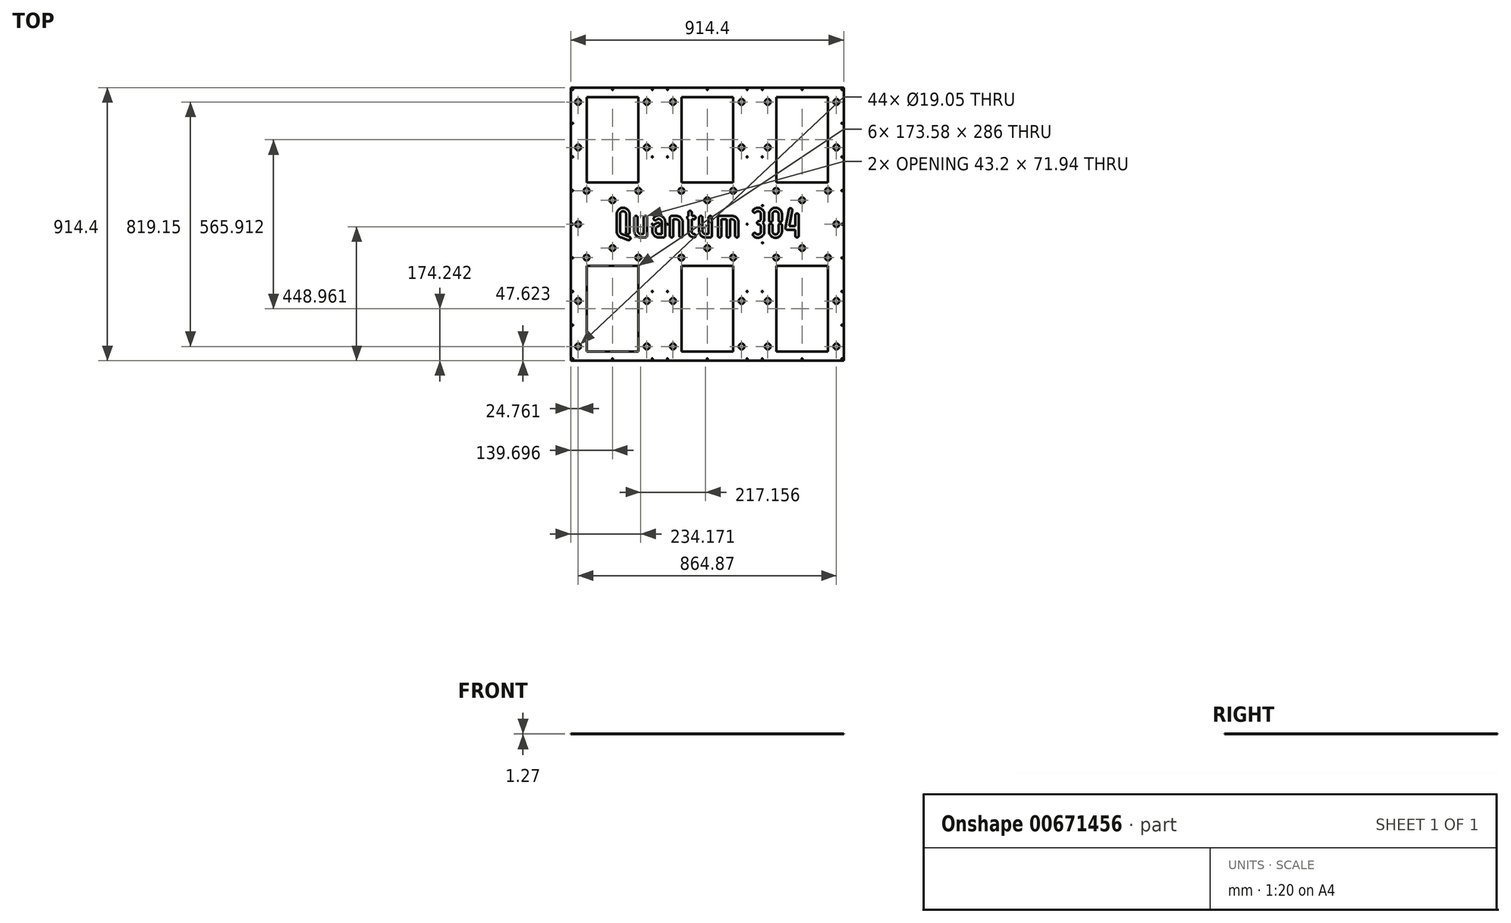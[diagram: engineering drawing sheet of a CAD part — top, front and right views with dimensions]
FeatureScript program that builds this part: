
annotation { "Feature Type Name" : "Feature", "Feature Type Description" : "" }
export const myFeature = defineFeature(function(context is Context, id is Id, definition is map)
    precondition{}
    {
        {
            var Q0;
            Q0=qCreatedBy(makeId("Top.planeOp"),FACE);
            var sketch = newSketch(context, id + "F0", { "sketchPlane" : qUnion([Q0])});
            skLineSegment(sketch, "E0.bottom", {"start": v(-471.91, 518.2) * mm, "end": v(442.49, 518.2) * mm});
            skLineSegment(sketch, "E0.top", {"start": v(-471.91, -396.2) * mm, "end": v(442.49, -396.2) * mm});
            skLineSegment(sketch, "E0.left", {"start": v(-471.91, 518.2) * mm, "end": v(-471.91, -396.2) * mm});
            skLineSegment(sketch, "E0.right", {"start": v(442.49, 518.2) * mm, "end": v(442.49, -396.2) * mm});
            skLineSegment(sketch, "E1", {"start": v(-14.71, 518.2) * mm, "end": v(-14.71, -396.2) * mm, "construction": true});
            skLineSegment(sketch, "E2", {"start": v(-471.91, 61) * mm, "end": v(442.49, 61) * mm, "construction": true});
            skLineSegment(sketch, "E3.0", {"start": v(-459.21, 505.5) * mm, "end": v(-459.21, -383.5) * mm, "construction": true});
            skLineSegment(sketch, "E4.0", {"start": v(-471.91, 505.5) * mm, "end": v(442.49, 505.5) * mm, "construction": true});
            skLineSegment(sketch, "E5.0", {"start": v(429.79, 505.5) * mm, "end": v(429.79, -383.5) * mm, "construction": true});
            skLineSegment(sketch, "E6.0", {"start": v(-471.91, -383.5) * mm, "end": v(442.49, -383.5) * mm, "construction": true});
            skLineSegment(sketch, "E7.0", {"start": v(-192.51, 505.5) * mm, "end": v(-192.51, -383.5) * mm, "construction": true});
            skLineSegment(sketch, "E8.0", {"start": v(-205.21, 505.5) * mm, "end": v(-205.21, -383.5) * mm, "construction": true});
            skLineSegment(sketch, "E9.0", {"start": v(-154.41, 505.5) * mm, "end": v(-154.41, -383.5) * mm, "construction": true});
            skLineSegment(sketch, "E10.0", {"start": v(124.99, 505.5) * mm, "end": v(124.99, -383.5) * mm, "construction": true});
            skLineSegment(sketch, "E11.0", {"start": v(163.09, 505.5) * mm, "end": v(163.09, -383.5) * mm, "construction": true});
            skLineSegment(sketch, "E12.0", {"start": v(175.79, 505.5) * mm, "end": v(175.79, -383.5) * mm, "construction": true});
            skLineSegment(sketch, "E13.0", {"start": v(-141.71, 505.5) * mm, "end": v(-141.71, -383.5) * mm, "construction": true});
            skLineSegment(sketch, "E14.0", {"start": v(112.29, 505.5) * mm, "end": v(112.29, -383.5) * mm, "construction": true});
            skLineSegment(sketch, "E15.0", {"start": v(-332.21, 505.5) * mm, "end": v(-332.21, -383.5) * mm, "construction": true});
            skLineSegment(sketch, "E16.0", {"start": v(302.79, 505.5) * mm, "end": v(302.79, -383.5) * mm, "construction": true});
            skPoint(sketch, "E17.middle", {"position": v(-332.21, 61) * mm});
            skCircle(sketch, "E18", {"center": v(-332.21, 61) * mm, "radius": 68 * mm, "construction": true});
            skCircle(sketch, "E19", {"center": v(-384.71, 113.5) * mm, "radius": 1.65 * mm, "construction": true});
            skCircle(sketch, "E20.MirrorC", {"center": v(-279.71, 113.5) * mm, "radius": 1.65 * mm, "construction": true});
            skCircle(sketch, "E21.MirrorC", {"center": v(-384.71, 8.5) * mm, "radius": 1.65 * mm, "construction": true});
            skCircle(sketch, "E22.MirrorC", {"center": v(-279.71, 8.5) * mm, "radius": 1.65 * mm, "construction": true});
            skCircle(sketch, "E23.MirrorC", {"center": v(250.29, 113.5) * mm, "radius": 1.65 * mm, "construction": true});
            skCircle(sketch, "E24.MirrorC", {"center": v(355.29, 113.5) * mm, "radius": 1.65 * mm, "construction": true});
            skCircle(sketch, "E25.MirrorC", {"center": v(355.29, 8.5) * mm, "radius": 1.65 * mm, "construction": true});
            skCircle(sketch, "E26.MirrorC", {"center": v(250.29, 8.5) * mm, "radius": 1.65 * mm, "construction": true});
            skCircle(sketch, "E27.MirrorC", {"center": v(302.79, 61) * mm, "radius": 68 * mm, "construction": true});
            skCircle(sketch, "E28.MirrorC", {"center": v(-14.71, 61) * mm, "radius": 68 * mm, "construction": true});
            skCircle(sketch, "E29.MirrorC", {"center": v(-67.21, 113.5) * mm, "radius": 1.65 * mm, "construction": true});
            skCircle(sketch, "E30.MirrorC", {"center": v(37.79, 113.5) * mm, "radius": 1.65 * mm, "construction": true});
            skCircle(sketch, "E31.MirrorC", {"center": v(37.79, 8.5) * mm, "radius": 1.65 * mm, "construction": true});
            skCircle(sketch, "E32.MirrorC", {"center": v(-67.21, 8.5) * mm, "radius": 1.65 * mm, "construction": true});
            skLineSegment(sketch, "E33.bottom", {"start": v(-435.08, 499.15) * mm, "end": v(-229.34, 499.15) * mm, "construction": true});
            skLineSegment(sketch, "E33.top", {"start": v(-435.08, 188.76) * mm, "end": v(-229.34, 188.76) * mm, "construction": true});
            skLineSegment(sketch, "E33.left", {"start": v(-435.08, 499.15) * mm, "end": v(-435.08, 188.76) * mm, "construction": true});
            skLineSegment(sketch, "E33.right", {"start": v(-229.34, 499.15) * mm, "end": v(-229.34, 188.76) * mm, "construction": true});
            skLineSegment(sketch, "E34.MirrorCS", {"start": v(-117.58, 499.15) * mm, "end": v(-117.58, 188.76) * mm, "construction": true});
            skLineSegment(sketch, "E35.MirrorCS", {"start": v(88.16, 499.15) * mm, "end": v(88.16, 188.76) * mm, "construction": true});
            skLineSegment(sketch, "E36.MirrorCS", {"start": v(88.16, 499.15) * mm, "end": v(-117.58, 499.15) * mm, "construction": true});
            skLineSegment(sketch, "E37.MirrorCS", {"start": v(88.16, 188.76) * mm, "end": v(-117.58, 188.76) * mm, "construction": true});
            skLineSegment(sketch, "E38.MirrorCS", {"start": v(199.92, 499.15) * mm, "end": v(199.92, 188.76) * mm, "construction": true});
            skLineSegment(sketch, "E39.MirrorCS", {"start": v(405.66, 499.15) * mm, "end": v(405.66, 188.76) * mm, "construction": true});
            skLineSegment(sketch, "E40.MirrorCS", {"start": v(405.66, 499.15) * mm, "end": v(199.92, 499.15) * mm, "construction": true});
            skLineSegment(sketch, "E41.MirrorCS", {"start": v(405.66, 188.76) * mm, "end": v(199.92, 188.76) * mm, "construction": true});
            skLineSegment(sketch, "E42.MirrorCS", {"start": v(-435.08, -66.76) * mm, "end": v(-229.34, -66.76) * mm, "construction": true});
            skLineSegment(sketch, "E43.MirrorCS", {"start": v(-435.08, -377.15) * mm, "end": v(-435.08, -66.76) * mm, "construction": true});
            skLineSegment(sketch, "E44.MirrorCS", {"start": v(-229.34, -377.15) * mm, "end": v(-229.34, -66.76) * mm, "construction": true});
            skLineSegment(sketch, "E45.MirrorCS", {"start": v(-117.58, -377.15) * mm, "end": v(-117.58, -66.76) * mm, "construction": true});
            skLineSegment(sketch, "E46.MirrorCS", {"start": v(88.16, -66.76) * mm, "end": v(-117.58, -66.76) * mm, "construction": true});
            skLineSegment(sketch, "E47.MirrorCS", {"start": v(88.16, -377.15) * mm, "end": v(88.16, -66.76) * mm, "construction": true});
            skLineSegment(sketch, "E48.MirrorCS", {"start": v(199.92, -377.15) * mm, "end": v(199.92, -66.76) * mm, "construction": true});
            skLineSegment(sketch, "E49.MirrorCS", {"start": v(405.66, -66.76) * mm, "end": v(199.92, -66.76) * mm, "construction": true});
            skLineSegment(sketch, "E50.MirrorCS", {"start": v(405.66, -377.15) * mm, "end": v(405.66, -66.76) * mm, "construction": true});
            skLineSegment(sketch, "E51.MirrorCS", {"start": v(405.66, -377.15) * mm, "end": v(199.92, -377.15) * mm, "construction": true});
            skLineSegment(sketch, "E52.MirrorCS", {"start": v(88.16, -377.15) * mm, "end": v(-117.58, -377.15) * mm, "construction": true});
            skLineSegment(sketch, "E53.MirrorCS", {"start": v(-435.08, -377.15) * mm, "end": v(-229.34, -377.15) * mm, "construction": true});
            skLineSegment(sketch, "E54.bottom", {"start": v(-419, 486.96) * mm, "end": v(-245.42, 486.96) * mm});
            skLineSegment(sketch, "E54.top", {"start": v(-419, 200.95) * mm, "end": v(-245.42, 200.95) * mm});
            skLineSegment(sketch, "E54.left", {"start": v(-419, 486.96) * mm, "end": v(-419, 200.95) * mm});
            skLineSegment(sketch, "E54.right", {"start": v(-245.42, 486.96) * mm, "end": v(-245.42, 200.95) * mm});
            skLineSegment(sketch, "E55.MirrorCS", {"start": v(-101.5, 486.96) * mm, "end": v(-101.5, 200.95) * mm});
            skLineSegment(sketch, "E56.MirrorCS", {"start": v(72.08, 486.96) * mm, "end": v(-101.5, 486.96) * mm});
            skLineSegment(sketch, "E57.MirrorCS", {"start": v(72.08, 486.96) * mm, "end": v(72.08, 200.95) * mm});
            skLineSegment(sketch, "E58.MirrorCS", {"start": v(72.08, 200.95) * mm, "end": v(-101.5, 200.95) * mm});
            skLineSegment(sketch, "E59.MirrorCS", {"start": v(216, 486.96) * mm, "end": v(216, 200.95) * mm});
            skLineSegment(sketch, "E60.MirrorCS", {"start": v(389.58, 486.96) * mm, "end": v(216, 486.96) * mm});
            skLineSegment(sketch, "E61.MirrorCS", {"start": v(389.58, 200.95) * mm, "end": v(216, 200.95) * mm});
            skLineSegment(sketch, "E62.MirrorCS", {"start": v(389.58, 486.96) * mm, "end": v(389.58, 200.95) * mm});
            skLineSegment(sketch, "E63.MirrorCS", {"start": v(-419, -78.96) * mm, "end": v(-245.42, -78.96) * mm});
            skLineSegment(sketch, "E64.MirrorCS", {"start": v(-245.42, -364.96) * mm, "end": v(-245.42, -78.96) * mm});
            skLineSegment(sketch, "E65.MirrorCS", {"start": v(-419, -364.96) * mm, "end": v(-419, -78.96) * mm});
            skLineSegment(sketch, "E66.MirrorCS", {"start": v(-419, -364.96) * mm, "end": v(-245.42, -364.96) * mm});
            skLineSegment(sketch, "E67.MirrorCS", {"start": v(72.08, -364.96) * mm, "end": v(-101.5, -364.96) * mm});
            skLineSegment(sketch, "E68.MirrorCS", {"start": v(-101.5, -364.96) * mm, "end": v(-101.5, -78.96) * mm});
            skLineSegment(sketch, "E69.MirrorCS", {"start": v(72.08, -78.96) * mm, "end": v(-101.5, -78.96) * mm});
            skLineSegment(sketch, "E70.MirrorCS", {"start": v(72.08, -364.96) * mm, "end": v(72.08, -78.96) * mm});
            skLineSegment(sketch, "E71.MirrorCS", {"start": v(216, -364.96) * mm, "end": v(216, -78.96) * mm});
            skLineSegment(sketch, "E72.MirrorCS", {"start": v(389.58, -364.96) * mm, "end": v(216, -364.96) * mm});
            skLineSegment(sketch, "E73.MirrorCS", {"start": v(389.58, -364.96) * mm, "end": v(389.58, -78.96) * mm});
            skLineSegment(sketch, "E74.MirrorCS", {"start": v(389.58, -78.96) * mm, "end": v(216, -78.96) * mm});
            skCircle(sketch, "E75", {"center": v(-332.21, 141.14) * mm, "radius": 9.53 * mm});
            skCircle(sketch, "E76", {"center": v(-245.42, 172.89) * mm, "radius": 9.53 * mm});
            skCircle(sketch, "E77", {"center": v(-419, 172.89) * mm, "radius": 9.53 * mm});
            skCircle(sketch, "E78.MirrorC", {"center": v(216, 172.89) * mm, "radius": 9.53 * mm});
            skCircle(sketch, "E79.MirrorC", {"center": v(302.79, 141.14) * mm, "radius": 9.53 * mm});
            skCircle(sketch, "E80.MirrorC", {"center": v(389.58, 172.89) * mm, "radius": 9.53 * mm});
            skCircle(sketch, "E81.MirrorC", {"center": v(-245.42, -50.89) * mm, "radius": 9.53 * mm});
            skCircle(sketch, "E82.MirrorC", {"center": v(-332.21, -19.14) * mm, "radius": 9.53 * mm});
            skCircle(sketch, "E83.MirrorC", {"center": v(-419, -50.89) * mm, "radius": 9.53 * mm});
            skCircle(sketch, "E84.MirrorC", {"center": v(216, -50.89) * mm, "radius": 9.53 * mm});
            skCircle(sketch, "E85.MirrorC", {"center": v(302.79, -19.14) * mm, "radius": 9.53 * mm});
            skCircle(sketch, "E86.MirrorC", {"center": v(389.58, -50.89) * mm, "radius": 9.53 * mm});
            skCircle(sketch, "E87", {"center": v(-447.15, -196.18) * mm, "radius": 9.53 * mm});
            skCircle(sketch, "E88", {"center": v(-447.15, -348.58) * mm, "radius": 9.53 * mm});
            skCircle(sketch, "E89.MirrorC", {"center": v(-217.28, -196.18) * mm, "radius": 9.53 * mm});
            skCircle(sketch, "E90.MirrorC", {"center": v(-217.28, -348.58) * mm, "radius": 9.53 * mm});
            skCircle(sketch, "E91.MirrorC", {"center": v(187.85, -196.18) * mm, "radius": 9.53 * mm});
            skCircle(sketch, "E92.MirrorC", {"center": v(187.85, -348.58) * mm, "radius": 9.53 * mm});
            skCircle(sketch, "E93.MirrorC", {"center": v(417.72, -196.18) * mm, "radius": 9.53 * mm});
            skCircle(sketch, "E94.MirrorC", {"center": v(417.72, -348.58) * mm, "radius": 9.53 * mm});
            skCircle(sketch, "E95.MirrorC", {"center": v(-447.15, 318.17) * mm, "radius": 9.53 * mm});
            skCircle(sketch, "E96.MirrorC", {"center": v(-447.15, 470.57) * mm, "radius": 9.53 * mm});
            skCircle(sketch, "E97.MirrorC", {"center": v(-217.28, 318.17) * mm, "radius": 9.53 * mm});
            skCircle(sketch, "E98.MirrorC", {"center": v(-217.28, 470.57) * mm, "radius": 9.53 * mm});
            skCircle(sketch, "E99.MirrorC", {"center": v(187.85, 470.57) * mm, "radius": 9.53 * mm});
            skCircle(sketch, "E100.MirrorC", {"center": v(187.85, 318.17) * mm, "radius": 9.53 * mm});
            skCircle(sketch, "E101.MirrorC", {"center": v(417.72, 318.17) * mm, "radius": 9.53 * mm});
            skCircle(sketch, "E102.MirrorC", {"center": v(417.72, 470.57) * mm, "radius": 9.53 * mm});
            skCircle(sketch, "E103.MirrorC", {"center": v(-129.65, 470.57) * mm, "radius": 9.53 * mm});
            skCircle(sketch, "E104.MirrorC", {"center": v(100.22, 470.57) * mm, "radius": 9.53 * mm});
            skCircle(sketch, "E105.MirrorC", {"center": v(100.22, 318.17) * mm, "radius": 9.53 * mm});
            skCircle(sketch, "E106.MirrorC", {"center": v(-129.65, 318.17) * mm, "radius": 9.53 * mm});
            skCircle(sketch, "E107.MirrorC", {"center": v(-101.5, 172.89) * mm, "radius": 9.53 * mm});
            skCircle(sketch, "E108.MirrorC", {"center": v(-14.71, 141.14) * mm, "radius": 9.53 * mm});
            skCircle(sketch, "E109.MirrorC", {"center": v(72.08, 172.89) * mm, "radius": 9.53 * mm});
            skCircle(sketch, "E110.MirrorC", {"center": v(72.08, -50.89) * mm, "radius": 9.53 * mm});
            skCircle(sketch, "E111.MirrorC", {"center": v(-14.71, -19.14) * mm, "radius": 9.53 * mm});
            skCircle(sketch, "E112.MirrorC", {"center": v(-101.5, -50.89) * mm, "radius": 9.53 * mm});
            skCircle(sketch, "E113.MirrorC", {"center": v(-129.65, -196.18) * mm, "radius": 9.53 * mm});
            skCircle(sketch, "E114.MirrorC", {"center": v(-129.65, -348.58) * mm, "radius": 9.53 * mm});
            skCircle(sketch, "E115.MirrorC", {"center": v(100.22, -348.58) * mm, "radius": 9.53 * mm});
            skCircle(sketch, "E116.MirrorC", {"center": v(100.22, -196.18) * mm, "radius": 9.53 * mm});
            skCircle(sketch, "E117", {"center": v(-447.15, 61) * mm, "radius": 9.53 * mm});
            skCircle(sketch, "E118", {"center": v(417.72, 61) * mm, "radius": 9.53 * mm});
            skCircle(sketch, "E119", {"center": v(436.14, 511.85) * mm, "radius": 1.59 * mm});
            skCircle(sketch, "E120", {"center": v(302.79, 511.85) * mm, "radius": 1.59 * mm});
            skLineSegment(sketch, "E121", {"start": v(169.44, 505.5) * mm, "end": v(169.44, 518.2) * mm, "construction": true});
            skCircle(sketch, "E122", {"center": v(169.44, 511.85) * mm, "radius": 1.59 * mm});
            skCircle(sketch, "E123", {"center": v(436.14, 61) * mm, "radius": 1.59 * mm});
            skCircle(sketch, "E124", {"center": v(436.14, 399.14) * mm, "radius": 1.59 * mm});
            skCircle(sketch, "E125", {"center": v(436.14, 286.42) * mm, "radius": 1.59 * mm});
            skCircle(sketch, "E126", {"center": v(436.14, 173.71) * mm, "radius": 1.59 * mm});
            skCircle(sketch, "E127.MirrorC", {"center": v(169.44, 286.42) * mm, "radius": 1.59 * mm});
            skCircle(sketch, "E128.MirrorC", {"center": v(169.44, -164.43) * mm, "radius": 1.59 * mm});
            skCircle(sketch, "E129.MirrorC", {"center": v(169.44, -389.85) * mm, "radius": 1.59 * mm});
            skCircle(sketch, "E130.MirrorC", {"center": v(302.79, -389.85) * mm, "radius": 1.59 * mm});
            skCircle(sketch, "E131.MirrorC", {"center": v(436.14, -389.85) * mm, "radius": 1.59 * mm});
            skCircle(sketch, "E132.MirrorC", {"center": v(436.14, -277.14) * mm, "radius": 1.59 * mm});
            skCircle(sketch, "E133.MirrorC", {"center": v(436.14, -164.43) * mm, "radius": 1.59 * mm});
            skCircle(sketch, "E134.MirrorC", {"center": v(436.14, -51.71) * mm, "radius": 1.59 * mm});
            skCircle(sketch, "E135.MirrorC", {"center": v(-198.86, 61) * mm, "radius": 1.59 * mm});
            skCircle(sketch, "E136.MirrorC", {"center": v(-198.86, 286.42) * mm, "radius": 1.59 * mm});
            skCircle(sketch, "E137.MirrorC", {"center": v(-198.86, 511.85) * mm, "radius": 1.59 * mm});
            skCircle(sketch, "E138.MirrorC", {"center": v(-332.21, 511.85) * mm, "radius": 1.59 * mm});
            skCircle(sketch, "E139.MirrorC", {"center": v(-465.56, 511.85) * mm, "radius": 1.59 * mm});
            skCircle(sketch, "E140.MirrorC", {"center": v(-465.56, 399.14) * mm, "radius": 1.59 * mm});
            skCircle(sketch, "E141.MirrorC", {"center": v(-465.56, 286.42) * mm, "radius": 1.59 * mm});
            skCircle(sketch, "E142.MirrorC", {"center": v(-465.56, 173.71) * mm, "radius": 1.59 * mm});
            skCircle(sketch, "E143.MirrorC", {"center": v(-465.56, 61) * mm, "radius": 1.59 * mm});
            skCircle(sketch, "E144.MirrorC", {"center": v(-465.56, -51.71) * mm, "radius": 1.59 * mm});
            skCircle(sketch, "E145.MirrorC", {"center": v(-465.56, -164.43) * mm, "radius": 1.59 * mm});
            skCircle(sketch, "E146.MirrorC", {"center": v(-465.56, -277.14) * mm, "radius": 1.59 * mm});
            skCircle(sketch, "E147.MirrorC", {"center": v(-465.56, -389.85) * mm, "radius": 1.59 * mm});
            skCircle(sketch, "E148.MirrorC", {"center": v(-332.21, -389.85) * mm, "radius": 1.59 * mm});
            skCircle(sketch, "E149.MirrorC", {"center": v(-198.86, -389.85) * mm, "radius": 1.59 * mm});
            skCircle(sketch, "E150.MirrorC", {"center": v(-198.86, -164.43) * mm, "radius": 1.59 * mm});
            skCircle(sketch, "E151.MirrorC", {"center": v(118.64, 61) * mm, "radius": 1.59 * mm});
            skCircle(sketch, "E152.MirrorC", {"center": v(118.64, 286.42) * mm, "radius": 1.59 * mm});
            skCircle(sketch, "E153.MirrorC", {"center": v(118.64, 511.85) * mm, "radius": 1.59 * mm});
            skCircle(sketch, "E154.MirrorC", {"center": v(-14.71, 511.85) * mm, "radius": 1.59 * mm});
            skCircle(sketch, "E155.MirrorC", {"center": v(-148.06, 511.85) * mm, "radius": 1.59 * mm});
            skCircle(sketch, "E156.MirrorC", {"center": v(-148.06, 286.42) * mm, "radius": 1.59 * mm});
            skCircle(sketch, "E157.MirrorC", {"center": v(-148.06, 61) * mm, "radius": 1.59 * mm});
            skCircle(sketch, "E158.MirrorC", {"center": v(-148.06, -164.43) * mm, "radius": 1.59 * mm});
            skCircle(sketch, "E159.MirrorC", {"center": v(-148.06, -389.85) * mm, "radius": 1.59 * mm});
            skCircle(sketch, "E160.MirrorC", {"center": v(-14.71, -389.85) * mm, "radius": 1.59 * mm});
            skCircle(sketch, "E161.MirrorC", {"center": v(118.64, -389.85) * mm, "radius": 1.59 * mm});
            skCircle(sketch, "E162.MirrorC", {"center": v(118.64, -164.43) * mm, "radius": 1.59 * mm});
            skCircle(sketch, "E163", {"center": v(169.44, 365.8) * mm, "radius": 3.15 * mm, "construction": true});
            skCircle(sketch, "E164.MirrorC", {"center": v(-198.86, 365.8) * mm, "radius": 3.15 * mm, "construction": true});
            skCircle(sketch, "E165.MirrorC", {"center": v(-198.86, -243.8) * mm, "radius": 3.15 * mm, "construction": true});
            skCircle(sketch, "E166.MirrorC", {"center": v(169.44, -243.8) * mm, "radius": 3.15 * mm, "construction": true});
            skLineSegment(sketch, "E167", {"start": v(-318.16, 96.62) * mm, "end": v(-317.86, 98.76) * mm});
            skLineSegment(sketch, "E168", {"start": v(-317.86, 98.76) * mm, "end": v(-317.35, 100.75) * mm});
            skLineSegment(sketch, "E169", {"start": v(-317.35, 100.75) * mm, "end": v(-316.69, 102.74) * mm});
            skLineSegment(sketch, "E170", {"start": v(-316.69, 102.74) * mm, "end": v(-315.73, 104.58) * mm});
            skLineSegment(sketch, "E171", {"start": v(-315.73, 104.58) * mm, "end": v(-314.7, 106.35) * mm});
            skLineSegment(sketch, "E172", {"start": v(-314.7, 106.35) * mm, "end": v(-313.37, 108.05) * mm});
            skLineSegment(sketch, "E173", {"start": v(-313.37, 108.05) * mm, "end": v(-311.9, 109.67) * mm});
            skLineSegment(sketch, "E174", {"start": v(-311.9, 109.67) * mm, "end": v(-310.27, 111.14) * mm});
            skLineSegment(sketch, "E175", {"start": v(-310.27, 111.14) * mm, "end": v(-308.58, 112.47) * mm});
            skLineSegment(sketch, "E176", {"start": v(-308.58, 112.47) * mm, "end": v(-306.8, 113.5) * mm});
            skLineSegment(sketch, "E177", {"start": v(-306.8, 113.5) * mm, "end": v(-304.97, 114.46) * mm});
            skLineSegment(sketch, "E178", {"start": v(-304.97, 114.46) * mm, "end": v(-302.97, 115.12) * mm});
            skLineSegment(sketch, "E179", {"start": v(-302.97, 115.12) * mm, "end": v(-300.98, 115.64) * mm});
            skLineSegment(sketch, "E180", {"start": v(-300.98, 115.64) * mm, "end": v(-298.85, 115.93) * mm});
            skLineSegment(sketch, "E181", {"start": v(-298.85, 115.93) * mm, "end": v(-296.64, 116) * mm});
            skLineSegment(sketch, "E182", {"start": v(-296.64, 116) * mm, "end": v(-294.5, 115.93) * mm});
            skLineSegment(sketch, "E183", {"start": v(-294.5, 115.93) * mm, "end": v(-292.36, 115.64) * mm});
            skLineSegment(sketch, "E184", {"start": v(-292.36, 115.64) * mm, "end": v(-290.37, 115.12) * mm});
            skLineSegment(sketch, "E185", {"start": v(-290.37, 115.12) * mm, "end": v(-288.38, 114.46) * mm});
            skLineSegment(sketch, "E186", {"start": v(-288.38, 114.46) * mm, "end": v(-286.54, 113.5) * mm});
            skLineSegment(sketch, "E187", {"start": v(-286.54, 113.5) * mm, "end": v(-284.77, 112.47) * mm});
            skLineSegment(sketch, "E188", {"start": v(-284.77, 112.47) * mm, "end": v(-283.07, 111.14) * mm});
            skLineSegment(sketch, "E189", {"start": v(-283.07, 111.14) * mm, "end": v(-281.45, 109.67) * mm});
            skLineSegment(sketch, "E190", {"start": v(-281.45, 109.67) * mm, "end": v(-279.98, 108.05) * mm});
            skLineSegment(sketch, "E191", {"start": v(-279.98, 108.05) * mm, "end": v(-278.65, 106.35) * mm});
            skLineSegment(sketch, "E192", {"start": v(-278.65, 106.35) * mm, "end": v(-277.62, 104.58) * mm});
            skLineSegment(sketch, "E193", {"start": v(-277.62, 104.58) * mm, "end": v(-276.66, 102.74) * mm});
            skLineSegment(sketch, "E194", {"start": v(-276.66, 102.74) * mm, "end": v(-276, 100.75) * mm});
            skLineSegment(sketch, "E195", {"start": v(-276, 100.75) * mm, "end": v(-275.48, 98.76) * mm});
            skLineSegment(sketch, "E196", {"start": v(-275.48, 98.76) * mm, "end": v(-275.19, 96.62) * mm});
            skLineSegment(sketch, "E197", {"start": v(-275.19, 96.62) * mm, "end": v(-275.11, 94.48) * mm});
            skLineSegment(sketch, "E198", {"start": v(-275.11, 94.48) * mm, "end": v(-275.11, 36.99) * mm});
            skLineSegment(sketch, "E199", {"start": v(-275.11, 36.99) * mm, "end": v(-275.11, 36.32) * mm});
            skLineSegment(sketch, "E200", {"start": v(-275.11, 36.32) * mm, "end": v(-275.11, 35.66) * mm});
            skLineSegment(sketch, "E201", {"start": v(-275.11, 35.66) * mm, "end": v(-275.19, 35) * mm});
            skLineSegment(sketch, "E202", {"start": v(-275.19, 35) * mm, "end": v(-275.26, 34.33) * mm});
            skLineSegment(sketch, "E203", {"start": v(-275.26, 34.33) * mm, "end": v(-275.33, 33.74) * mm});
            skLineSegment(sketch, "E204", {"start": v(-275.33, 33.74) * mm, "end": v(-275.4, 33.08) * mm});
            skLineSegment(sketch, "E205", {"start": v(-275.4, 33.08) * mm, "end": v(-275.48, 32.5) * mm});
            skLineSegment(sketch, "E206", {"start": v(-275.48, 32.5) * mm, "end": v(-275.63, 31.83) * mm});
            skLineSegment(sketch, "E207", {"start": v(-275.63, 31.83) * mm, "end": v(-275.7, 31.46) * mm});
            skLineSegment(sketch, "E208", {"start": v(-275.7, 31.46) * mm, "end": v(-275.85, 31.02) * mm});
            skLineSegment(sketch, "E209", {"start": v(-275.85, 31.02) * mm, "end": v(-276, 30.65) * mm});
            skLineSegment(sketch, "E210", {"start": v(-276, 30.65) * mm, "end": v(-276.14, 30.28) * mm});
            skLineSegment(sketch, "E211", {"start": v(-276.14, 30.28) * mm, "end": v(-276.36, 29.98) * mm});
            skLineSegment(sketch, "E212", {"start": v(-276.36, 29.98) * mm, "end": v(-276.59, 29.62) * mm});
            skLineSegment(sketch, "E213", {"start": v(-276.59, 29.62) * mm, "end": v(-276.88, 29.32) * mm});
            skLineSegment(sketch, "E214", {"start": v(-276.88, 29.32) * mm, "end": v(-277.18, 28.95) * mm});
            skLineSegment(sketch, "E215", {"start": v(-277.18, 28.95) * mm, "end": v(-277.62, 28.58) * mm});
            skLineSegment(sketch, "E216", {"start": v(-277.62, 28.58) * mm, "end": v(-278.13, 28.21) * mm});
            skLineSegment(sketch, "E217", {"start": v(-278.13, 28.21) * mm, "end": v(-278.58, 27.92) * mm});
            skLineSegment(sketch, "E218", {"start": v(-278.58, 27.92) * mm, "end": v(-279.1, 27.7) * mm});
            skLineSegment(sketch, "E219", {"start": v(-279.1, 27.7) * mm, "end": v(-279.6, 27.48) * mm});
            skLineSegment(sketch, "E220", {"start": v(-279.6, 27.48) * mm, "end": v(-280.12, 27.33) * mm});
            skLineSegment(sketch, "E221", {"start": v(-280.12, 27.33) * mm, "end": v(-280.71, 27.26) * mm});
            skLineSegment(sketch, "E222", {"start": v(-280.71, 27.26) * mm, "end": v(-281.3, 27.26) * mm});
            skLineSegment(sketch, "E223", {"start": v(-281.3, 27.26) * mm, "end": v(-281.9, 27.26) * mm});
            skLineSegment(sketch, "E224", {"start": v(-281.9, 27.26) * mm, "end": v(-282.4, 27.33) * mm});
            skLineSegment(sketch, "E225", {"start": v(-282.4, 27.33) * mm, "end": v(-283, 27.48) * mm});
            skLineSegment(sketch, "E226", {"start": v(-283, 27.48) * mm, "end": v(-283.51, 27.7) * mm});
            skLineSegment(sketch, "E227", {"start": v(-283.51, 27.7) * mm, "end": v(-283.96, 27.92) * mm});
            skLineSegment(sketch, "E228", {"start": v(-283.96, 27.92) * mm, "end": v(-284.47, 28.21) * mm});
            skLineSegment(sketch, "E229", {"start": v(-284.47, 28.21) * mm, "end": v(-284.92, 28.5) * mm});
            skLineSegment(sketch, "E230", {"start": v(-284.92, 28.5) * mm, "end": v(-285.36, 28.95) * mm});
            skLineSegment(sketch, "E231", {"start": v(-285.36, 28.95) * mm, "end": v(-285.73, 29.4) * mm});
            skLineSegment(sketch, "E232", {"start": v(-285.73, 29.4) * mm, "end": v(-286.1, 29.84) * mm});
            skLineSegment(sketch, "E233", {"start": v(-286.1, 29.84) * mm, "end": v(-286.39, 30.28) * mm});
            skLineSegment(sketch, "E234", {"start": v(-286.39, 30.28) * mm, "end": v(-286.61, 30.8) * mm});
            skLineSegment(sketch, "E235", {"start": v(-286.61, 30.8) * mm, "end": v(-286.83, 31.31) * mm});
            skLineSegment(sketch, "E236", {"start": v(-286.83, 31.31) * mm, "end": v(-286.9, 31.83) * mm});
            skLineSegment(sketch, "E237", {"start": v(-286.9, 31.83) * mm, "end": v(-286.98, 32.42) * mm});
            skLineSegment(sketch, "E238", {"start": v(-286.98, 32.42) * mm, "end": v(-287.05, 33) * mm});
            skLineSegment(sketch, "E239", {"start": v(-287.05, 33) * mm, "end": v(-287.05, 33.15) * mm});
            skLineSegment(sketch, "E240", {"start": v(-287.05, 33.15) * mm, "end": v(-287.05, 33.3) * mm});
            skLineSegment(sketch, "E241", {"start": v(-287.05, 33.3) * mm, "end": v(-287.05, 33.45) * mm});
            skLineSegment(sketch, "E242", {"start": v(-287.05, 33.45) * mm, "end": v(-287.05, 33.6) * mm});
            skLineSegment(sketch, "E243", {"start": v(-287.05, 33.6) * mm, "end": v(-286.98, 33.74) * mm});
            skLineSegment(sketch, "E244", {"start": v(-286.98, 33.74) * mm, "end": v(-286.98, 33.96) * mm});
            skLineSegment(sketch, "E245", {"start": v(-286.98, 33.96) * mm, "end": v(-286.98, 34.11) * mm});
            skLineSegment(sketch, "E246", {"start": v(-286.98, 34.11) * mm, "end": v(-286.98, 34.26) * mm});
            skLineSegment(sketch, "E247", {"start": v(-286.98, 34.26) * mm, "end": v(-286.9, 34.63) * mm});
            skLineSegment(sketch, "E248", {"start": v(-286.9, 34.63) * mm, "end": v(-286.83, 34.92) * mm});
            skLineSegment(sketch, "E249", {"start": v(-286.83, 34.92) * mm, "end": v(-286.76, 35.3) * mm});
            skLineSegment(sketch, "E250", {"start": v(-286.76, 35.3) * mm, "end": v(-286.68, 35.59) * mm});
            skLineSegment(sketch, "E251", {"start": v(-286.68, 35.59) * mm, "end": v(-286.68, 35.95) * mm});
            skLineSegment(sketch, "E252", {"start": v(-286.68, 35.95) * mm, "end": v(-286.61, 36.25) * mm});
            skLineSegment(sketch, "E253", {"start": v(-286.61, 36.25) * mm, "end": v(-286.61, 36.62) * mm});
            skLineSegment(sketch, "E254", {"start": v(-286.61, 36.62) * mm, "end": v(-286.61, 36.99) * mm});
            skLineSegment(sketch, "E255", {"start": v(-286.61, 36.99) * mm, "end": v(-286.61, 94.48) * mm});
            skLineSegment(sketch, "E256", {"start": v(-286.61, 94.48) * mm, "end": v(-286.68, 95.44) * mm});
            skLineSegment(sketch, "E257", {"start": v(-286.68, 95.44) * mm, "end": v(-286.76, 96.47) * mm});
            skLineSegment(sketch, "E258", {"start": v(-286.76, 96.47) * mm, "end": v(-287.05, 97.43) * mm});
            skLineSegment(sketch, "E259", {"start": v(-287.05, 97.43) * mm, "end": v(-287.35, 98.32) * mm});
            skLineSegment(sketch, "E260", {"start": v(-287.35, 98.32) * mm, "end": v(-287.8, 99.2) * mm});
            skLineSegment(sketch, "E261", {"start": v(-287.8, 99.2) * mm, "end": v(-288.23, 100.01) * mm});
            skLineSegment(sketch, "E262", {"start": v(-288.23, 100.01) * mm, "end": v(-288.9, 100.82) * mm});
            skLineSegment(sketch, "E263", {"start": v(-288.9, 100.82) * mm, "end": v(-289.56, 101.56) * mm});
            skLineSegment(sketch, "E264", {"start": v(-289.56, 101.56) * mm, "end": v(-290.3, 102.22) * mm});
            skLineSegment(sketch, "E265", {"start": v(-290.3, 102.22) * mm, "end": v(-291.1, 102.89) * mm});
            skLineSegment(sketch, "E266", {"start": v(-291.1, 102.89) * mm, "end": v(-291.92, 103.33) * mm});
            skLineSegment(sketch, "E267", {"start": v(-291.92, 103.33) * mm, "end": v(-292.8, 103.77) * mm});
            skLineSegment(sketch, "E268", {"start": v(-292.8, 103.77) * mm, "end": v(-293.69, 104.06) * mm});
            skLineSegment(sketch, "E269", {"start": v(-293.69, 104.06) * mm, "end": v(-294.65, 104.36) * mm});
            skLineSegment(sketch, "E270", {"start": v(-294.65, 104.36) * mm, "end": v(-295.68, 104.43) * mm});
            skLineSegment(sketch, "E271", {"start": v(-295.68, 104.43) * mm, "end": v(-296.64, 104.5) * mm});
            skLineSegment(sketch, "E272", {"start": v(-296.64, 104.5) * mm, "end": v(-297.67, 104.43) * mm});
            skLineSegment(sketch, "E273", {"start": v(-297.67, 104.43) * mm, "end": v(-298.7, 104.36) * mm});
            skLineSegment(sketch, "E274", {"start": v(-298.7, 104.36) * mm, "end": v(-299.66, 104.06) * mm});
            skLineSegment(sketch, "E275", {"start": v(-299.66, 104.06) * mm, "end": v(-300.54, 103.77) * mm});
            skLineSegment(sketch, "E276", {"start": v(-300.54, 103.77) * mm, "end": v(-301.43, 103.33) * mm});
            skLineSegment(sketch, "E277", {"start": v(-301.43, 103.33) * mm, "end": v(-302.24, 102.89) * mm});
            skLineSegment(sketch, "E278", {"start": v(-302.24, 102.89) * mm, "end": v(-303.05, 102.22) * mm});
            skLineSegment(sketch, "E279", {"start": v(-303.05, 102.22) * mm, "end": v(-303.79, 101.56) * mm});
            skLineSegment(sketch, "E280", {"start": v(-303.79, 101.56) * mm, "end": v(-304.45, 100.82) * mm});
            skLineSegment(sketch, "E281", {"start": v(-304.45, 100.82) * mm, "end": v(-305.11, 100.01) * mm});
            skLineSegment(sketch, "E282", {"start": v(-305.11, 100.01) * mm, "end": v(-305.55, 99.2) * mm});
            skLineSegment(sketch, "E283", {"start": v(-305.55, 99.2) * mm, "end": v(-306, 98.32) * mm});
            skLineSegment(sketch, "E284", {"start": v(-306, 98.32) * mm, "end": v(-306.3, 97.43) * mm});
            skLineSegment(sketch, "E285", {"start": v(-306.3, 97.43) * mm, "end": v(-306.59, 96.47) * mm});
            skLineSegment(sketch, "E286", {"start": v(-306.59, 96.47) * mm, "end": v(-306.66, 95.44) * mm});
            skLineSegment(sketch, "E287", {"start": v(-306.66, 95.44) * mm, "end": v(-306.73, 94.48) * mm});
            skLineSegment(sketch, "E288", {"start": v(-306.73, 94.48) * mm, "end": v(-306.73, 36.99) * mm});
            skLineSegment(sketch, "E289", {"start": v(-306.73, 36.99) * mm, "end": v(-306.66, 35.95) * mm});
            skLineSegment(sketch, "E290", {"start": v(-306.66, 35.95) * mm, "end": v(-306.59, 35) * mm});
            skLineSegment(sketch, "E291", {"start": v(-306.59, 35) * mm, "end": v(-306.37, 34.11) * mm});
            skLineSegment(sketch, "E292", {"start": v(-306.37, 34.11) * mm, "end": v(-306.07, 33.23) * mm});
            skLineSegment(sketch, "E293", {"start": v(-306.07, 33.23) * mm, "end": v(-305.63, 32.42) * mm});
            skLineSegment(sketch, "E294", {"start": v(-305.63, 32.42) * mm, "end": v(-305.19, 31.68) * mm});
            skLineSegment(sketch, "E295", {"start": v(-305.19, 31.68) * mm, "end": v(-304.6, 30.94) * mm});
            skLineSegment(sketch, "E296", {"start": v(-304.6, 30.94) * mm, "end": v(-303.93, 30.28) * mm});
            skLineSegment(sketch, "E297", {"start": v(-303.93, 30.28) * mm, "end": v(-303.27, 29.69) * mm});
            skLineSegment(sketch, "E298", {"start": v(-303.27, 29.69) * mm, "end": v(-302.53, 29.1) * mm});
            skLineSegment(sketch, "E299", {"start": v(-302.53, 29.1) * mm, "end": v(-301.8, 28.58) * mm});
            skLineSegment(sketch, "E300", {"start": v(-301.8, 28.58) * mm, "end": v(-300.98, 28.14) * mm});
            skLineSegment(sketch, "E301", {"start": v(-300.98, 28.14) * mm, "end": v(-300.25, 27.77) * mm});
            skLineSegment(sketch, "E302", {"start": v(-300.25, 27.77) * mm, "end": v(-299.36, 27.4) * mm});
            skLineSegment(sketch, "E303", {"start": v(-299.36, 27.4) * mm, "end": v(-298.55, 27.1) * mm});
            skLineSegment(sketch, "E304", {"start": v(-298.55, 27.1) * mm, "end": v(-297.67, 26.81) * mm});
            skLineSegment(sketch, "E305", {"start": v(-297.67, 26.81) * mm, "end": v(-275.63, 19.15) * mm});
            skLineSegment(sketch, "E306", {"start": v(-275.63, 19.15) * mm, "end": v(-275.04, 18.93) * mm});
            skLineSegment(sketch, "E307", {"start": v(-275.04, 18.93) * mm, "end": v(-274.52, 18.63) * mm});
            skLineSegment(sketch, "E308", {"start": v(-274.52, 18.63) * mm, "end": v(-274.08, 18.34) * mm});
            skLineSegment(sketch, "E309", {"start": v(-274.08, 18.34) * mm, "end": v(-273.64, 17.97) * mm});
            skLineSegment(sketch, "E310", {"start": v(-273.64, 17.97) * mm, "end": v(-273.2, 17.6) * mm});
            skLineSegment(sketch, "E311", {"start": v(-273.2, 17.6) * mm, "end": v(-272.83, 17.16) * mm});
            skLineSegment(sketch, "E312", {"start": v(-272.83, 17.16) * mm, "end": v(-272.53, 16.72) * mm});
            skLineSegment(sketch, "E313", {"start": v(-272.53, 16.72) * mm, "end": v(-272.24, 16.2) * mm});
            skLineSegment(sketch, "E314", {"start": v(-272.24, 16.2) * mm, "end": v(-272.09, 15.83) * mm});
            skLineSegment(sketch, "E315", {"start": v(-272.09, 15.83) * mm, "end": v(-272.02, 15.54) * mm});
            skLineSegment(sketch, "E316", {"start": v(-272.02, 15.54) * mm, "end": v(-271.87, 15.24) * mm});
            skLineSegment(sketch, "E317", {"start": v(-271.87, 15.24) * mm, "end": v(-271.8, 14.87) * mm});
            skLineSegment(sketch, "E318", {"start": v(-271.8, 14.87) * mm, "end": v(-271.72, 14.58) * mm});
            skLineSegment(sketch, "E319", {"start": v(-271.72, 14.58) * mm, "end": v(-271.72, 14.28) * mm});
            skLineSegment(sketch, "E320", {"start": v(-271.72, 14.28) * mm, "end": v(-271.65, 13.99) * mm});
            skLineSegment(sketch, "E321", {"start": v(-271.65, 13.99) * mm, "end": v(-271.65, 13.7) * mm});
            skLineSegment(sketch, "E322", {"start": v(-271.65, 13.7) * mm, "end": v(-271.65, 13.47) * mm});
            skLineSegment(sketch, "E323", {"start": v(-271.65, 13.47) * mm, "end": v(-271.65, 13.25) * mm});
            skLineSegment(sketch, "E324", {"start": v(-271.65, 13.25) * mm, "end": v(-271.72, 13.03) * mm});
            skLineSegment(sketch, "E325", {"start": v(-271.72, 13.03) * mm, "end": v(-271.72, 12.8) * mm});
            skLineSegment(sketch, "E326", {"start": v(-271.72, 12.8) * mm, "end": v(-271.8, 12.59) * mm});
            skLineSegment(sketch, "E327", {"start": v(-271.8, 12.59) * mm, "end": v(-271.8, 12.37) * mm});
            skLineSegment(sketch, "E328", {"start": v(-271.8, 12.37) * mm, "end": v(-271.87, 12.07) * mm});
            skLineSegment(sketch, "E329", {"start": v(-271.87, 12.07) * mm, "end": v(-271.94, 11.85) * mm});
            skLineSegment(sketch, "E330", {"start": v(-271.94, 11.85) * mm, "end": v(-272.16, 11.33) * mm});
            skLineSegment(sketch, "E331", {"start": v(-272.16, 11.33) * mm, "end": v(-272.46, 10.82) * mm});
            skLineSegment(sketch, "E332", {"start": v(-272.46, 10.82) * mm, "end": v(-272.75, 10.3) * mm});
            skLineSegment(sketch, "E333", {"start": v(-272.75, 10.3) * mm, "end": v(-273.05, 9.86) * mm});
            skLineSegment(sketch, "E334", {"start": v(-273.05, 9.86) * mm, "end": v(-273.49, 9.5) * mm});
            skLineSegment(sketch, "E335", {"start": v(-273.49, 9.5) * mm, "end": v(-273.93, 9.12) * mm});
            skLineSegment(sketch, "E336", {"start": v(-273.93, 9.12) * mm, "end": v(-274.37, 8.75) * mm});
            skLineSegment(sketch, "E337", {"start": v(-274.37, 8.75) * mm, "end": v(-274.9, 8.46) * mm});
            skLineSegment(sketch, "E338", {"start": v(-274.9, 8.46) * mm, "end": v(-275.19, 8.39) * mm});
            skLineSegment(sketch, "E339", {"start": v(-275.19, 8.39) * mm, "end": v(-275.55, 8.24) * mm});
            skLineSegment(sketch, "E340", {"start": v(-275.55, 8.24) * mm, "end": v(-275.85, 8.17) * mm});
            skLineSegment(sketch, "E341", {"start": v(-275.85, 8.17) * mm, "end": v(-276.14, 8.1) * mm});
            skLineSegment(sketch, "E342", {"start": v(-276.14, 8.1) * mm, "end": v(-276.51, 8.02) * mm});
            skLineSegment(sketch, "E343", {"start": v(-276.51, 8.02) * mm, "end": v(-276.8, 7.94) * mm});
            skLineSegment(sketch, "E344", {"start": v(-276.8, 7.94) * mm, "end": v(-277.1, 7.94) * mm});
            skLineSegment(sketch, "E345", {"start": v(-277.1, 7.94) * mm, "end": v(-277.4, 7.94) * mm});
            skLineSegment(sketch, "E346", {"start": v(-277.4, 7.94) * mm, "end": v(-277.62, 7.94) * mm});
            skLineSegment(sketch, "E347", {"start": v(-277.62, 7.94) * mm, "end": v(-277.91, 7.94) * mm});
            skLineSegment(sketch, "E348", {"start": v(-277.91, 7.94) * mm, "end": v(-278.13, 7.94) * mm});
            skLineSegment(sketch, "E349", {"start": v(-278.13, 7.94) * mm, "end": v(-278.35, 8.02) * mm});
            skLineSegment(sketch, "E350", {"start": v(-278.35, 8.02) * mm, "end": v(-278.58, 8.02) * mm});
            skLineSegment(sketch, "E351", {"start": v(-278.58, 8.02) * mm, "end": v(-278.8, 8.1) * mm});
            skLineSegment(sketch, "E352", {"start": v(-278.8, 8.1) * mm, "end": v(-279.02, 8.17) * mm});
            skLineSegment(sketch, "E353", {"start": v(-279.02, 8.17) * mm, "end": v(-279.31, 8.24) * mm});
            skLineSegment(sketch, "E354", {"start": v(-279.31, 8.24) * mm, "end": v(-302.39, 16.13) * mm});
            skLineSegment(sketch, "E355", {"start": v(-302.39, 16.13) * mm, "end": v(-303.86, 16.64) * mm});
            skLineSegment(sketch, "E356", {"start": v(-303.86, 16.64) * mm, "end": v(-305.19, 17.23) * mm});
            skLineSegment(sketch, "E357", {"start": v(-305.19, 17.23) * mm, "end": v(-306.51, 17.9) * mm});
            skLineSegment(sketch, "E358", {"start": v(-306.51, 17.9) * mm, "end": v(-307.7, 18.56) * mm});
            skLineSegment(sketch, "E359", {"start": v(-307.7, 18.56) * mm, "end": v(-308.87, 19.3) * mm});
            skLineSegment(sketch, "E360", {"start": v(-308.87, 19.3) * mm, "end": v(-309.98, 20.03) * mm});
            skLineSegment(sketch, "E361", {"start": v(-309.98, 20.03) * mm, "end": v(-310.94, 20.84) * mm});
            skLineSegment(sketch, "E362", {"start": v(-310.94, 20.84) * mm, "end": v(-311.9, 21.73) * mm});
            skLineSegment(sketch, "E363", {"start": v(-311.9, 21.73) * mm, "end": v(-313.37, 23.35) * mm});
            skLineSegment(sketch, "E364", {"start": v(-313.37, 23.35) * mm, "end": v(-314.7, 25.05) * mm});
            skLineSegment(sketch, "E365", {"start": v(-314.7, 25.05) * mm, "end": v(-315.73, 26.81) * mm});
            skLineSegment(sketch, "E366", {"start": v(-315.73, 26.81) * mm, "end": v(-316.69, 28.66) * mm});
            skLineSegment(sketch, "E367", {"start": v(-316.69, 28.66) * mm, "end": v(-317.35, 30.65) * mm});
            skLineSegment(sketch, "E368", {"start": v(-317.35, 30.65) * mm, "end": v(-317.86, 32.64) * mm});
            skLineSegment(sketch, "E369", {"start": v(-317.86, 32.64) * mm, "end": v(-318.16, 34.78) * mm});
            skLineSegment(sketch, "E370", {"start": v(-318.16, 34.78) * mm, "end": v(-318.23, 36.99) * mm});
            skLineSegment(sketch, "E371", {"start": v(-318.23, 36.99) * mm, "end": v(-318.23, 94.48) * mm});
            skLineSegment(sketch, "E372", {"start": v(-318.23, 94.48) * mm, "end": v(-318.16, 96.62) * mm});
            skLineSegment(sketch, "E373", {"start": v(-259.19, 36.18) * mm, "end": v(-259.34, 38.39) * mm});
            skLineSegment(sketch, "E374", {"start": v(-259.34, 38.39) * mm, "end": v(-259.34, 82.98) * mm});
            skLineSegment(sketch, "E375", {"start": v(-259.34, 82.98) * mm, "end": v(-259.26, 83.5) * mm});
            skLineSegment(sketch, "E376", {"start": v(-259.26, 83.5) * mm, "end": v(-259.19, 84.09) * mm});
            skLineSegment(sketch, "E377", {"start": v(-259.19, 84.09) * mm, "end": v(-259.04, 84.6) * mm});
            skLineSegment(sketch, "E378", {"start": v(-259.04, 84.6) * mm, "end": v(-258.9, 85.12) * mm});
            skLineSegment(sketch, "E379", {"start": v(-258.9, 85.12) * mm, "end": v(-258.67, 85.64) * mm});
            skLineSegment(sketch, "E380", {"start": v(-258.67, 85.64) * mm, "end": v(-258.38, 86.15) * mm});
            skLineSegment(sketch, "E381", {"start": v(-258.38, 86.15) * mm, "end": v(-258.01, 86.6) * mm});
            skLineSegment(sketch, "E382", {"start": v(-258.01, 86.6) * mm, "end": v(-257.64, 87.04) * mm});
            skLineSegment(sketch, "E383", {"start": v(-257.64, 87.04) * mm, "end": v(-257.2, 87.4) * mm});
            skLineSegment(sketch, "E384", {"start": v(-257.2, 87.4) * mm, "end": v(-256.76, 87.77) * mm});
            skLineSegment(sketch, "E385", {"start": v(-256.76, 87.77) * mm, "end": v(-256.24, 88.07) * mm});
            skLineSegment(sketch, "E386", {"start": v(-256.24, 88.07) * mm, "end": v(-255.73, 88.3) * mm});
            skLineSegment(sketch, "E387", {"start": v(-255.73, 88.3) * mm, "end": v(-255.2, 88.44) * mm});
            skLineSegment(sketch, "E388", {"start": v(-255.2, 88.44) * mm, "end": v(-254.7, 88.59) * mm});
            skLineSegment(sketch, "E389", {"start": v(-254.7, 88.59) * mm, "end": v(-254.1, 88.66) * mm});
            skLineSegment(sketch, "E390", {"start": v(-254.1, 88.66) * mm, "end": v(-253.59, 88.73) * mm});
            skLineSegment(sketch, "E391", {"start": v(-253.59, 88.73) * mm, "end": v(-253, 88.66) * mm});
            skLineSegment(sketch, "E392", {"start": v(-253, 88.66) * mm, "end": v(-252.4, 88.59) * mm});
            skLineSegment(sketch, "E393", {"start": v(-252.4, 88.59) * mm, "end": v(-251.9, 88.44) * mm});
            skLineSegment(sketch, "E394", {"start": v(-251.9, 88.44) * mm, "end": v(-251.38, 88.3) * mm});
            skLineSegment(sketch, "E395", {"start": v(-251.38, 88.3) * mm, "end": v(-250.86, 88.07) * mm});
            skLineSegment(sketch, "E396", {"start": v(-250.86, 88.07) * mm, "end": v(-250.34, 87.77) * mm});
            skLineSegment(sketch, "E397", {"start": v(-250.34, 87.77) * mm, "end": v(-249.9, 87.4) * mm});
            skLineSegment(sketch, "E398", {"start": v(-249.9, 87.4) * mm, "end": v(-249.46, 87.04) * mm});
            skLineSegment(sketch, "E399", {"start": v(-249.46, 87.04) * mm, "end": v(-249.1, 86.6) * mm});
            skLineSegment(sketch, "E400", {"start": v(-249.1, 86.6) * mm, "end": v(-248.72, 86.15) * mm});
            skLineSegment(sketch, "E401", {"start": v(-248.72, 86.15) * mm, "end": v(-248.43, 85.64) * mm});
            skLineSegment(sketch, "E402", {"start": v(-248.43, 85.64) * mm, "end": v(-248.2, 85.12) * mm});
            skLineSegment(sketch, "E403", {"start": v(-248.2, 85.12) * mm, "end": v(-248.06, 84.6) * mm});
            skLineSegment(sketch, "E404", {"start": v(-248.06, 84.6) * mm, "end": v(-247.91, 84.09) * mm});
            skLineSegment(sketch, "E405", {"start": v(-247.91, 84.09) * mm, "end": v(-247.84, 83.5) * mm});
            skLineSegment(sketch, "E406", {"start": v(-247.84, 83.5) * mm, "end": v(-247.84, 82.98) * mm});
            skLineSegment(sketch, "E407", {"start": v(-247.84, 82.98) * mm, "end": v(-247.84, 38.39) * mm});
            skLineSegment(sketch, "E408", {"start": v(-247.84, 38.39) * mm, "end": v(-247.76, 37.36) * mm});
            skLineSegment(sketch, "E409", {"start": v(-247.76, 37.36) * mm, "end": v(-247.62, 36.4) * mm});
            skLineSegment(sketch, "E410", {"start": v(-247.62, 36.4) * mm, "end": v(-247.4, 35.44) * mm});
            skLineSegment(sketch, "E411", {"start": v(-247.4, 35.44) * mm, "end": v(-247.1, 34.55) * mm});
            skLineSegment(sketch, "E412", {"start": v(-247.1, 34.55) * mm, "end": v(-246.66, 33.67) * mm});
            skLineSegment(sketch, "E413", {"start": v(-246.66, 33.67) * mm, "end": v(-246.14, 32.86) * mm});
            skLineSegment(sketch, "E414", {"start": v(-246.14, 32.86) * mm, "end": v(-245.55, 32.05) * mm});
            skLineSegment(sketch, "E415", {"start": v(-245.55, 32.05) * mm, "end": v(-244.89, 31.24) * mm});
            skLineSegment(sketch, "E416", {"start": v(-244.89, 31.24) * mm, "end": v(-244.08, 30.57) * mm});
            skLineSegment(sketch, "E417", {"start": v(-244.08, 30.57) * mm, "end": v(-243.27, 29.98) * mm});
            skLineSegment(sketch, "E418", {"start": v(-243.27, 29.98) * mm, "end": v(-242.46, 29.47) * mm});
            skLineSegment(sketch, "E419", {"start": v(-242.46, 29.47) * mm, "end": v(-241.57, 29.03) * mm});
            skLineSegment(sketch, "E420", {"start": v(-241.57, 29.03) * mm, "end": v(-240.69, 28.73) * mm});
            skLineSegment(sketch, "E421", {"start": v(-240.69, 28.73) * mm, "end": v(-239.73, 28.5) * mm});
            skLineSegment(sketch, "E422", {"start": v(-239.73, 28.5) * mm, "end": v(-238.77, 28.36) * mm});
            skLineSegment(sketch, "E423", {"start": v(-238.77, 28.36) * mm, "end": v(-237.74, 28.29) * mm});
            skLineSegment(sketch, "E424", {"start": v(-237.74, 28.29) * mm, "end": v(-227.64, 28.29) * mm});
            skLineSegment(sketch, "E425", {"start": v(-227.64, 28.29) * mm, "end": v(-227.64, 82.98) * mm});
            skLineSegment(sketch, "E426", {"start": v(-227.64, 82.98) * mm, "end": v(-227.64, 83.5) * mm});
            skLineSegment(sketch, "E427", {"start": v(-227.64, 83.5) * mm, "end": v(-227.57, 84.09) * mm});
            skLineSegment(sketch, "E428", {"start": v(-227.57, 84.09) * mm, "end": v(-227.42, 84.6) * mm});
            skLineSegment(sketch, "E429", {"start": v(-227.42, 84.6) * mm, "end": v(-227.27, 85.12) * mm});
            skLineSegment(sketch, "E430", {"start": v(-227.27, 85.12) * mm, "end": v(-227.05, 85.64) * mm});
            skLineSegment(sketch, "E431", {"start": v(-227.05, 85.64) * mm, "end": v(-226.76, 86.15) * mm});
            skLineSegment(sketch, "E432", {"start": v(-226.76, 86.15) * mm, "end": v(-226.39, 86.6) * mm});
            skLineSegment(sketch, "E433", {"start": v(-226.39, 86.6) * mm, "end": v(-226.02, 87.04) * mm});
            skLineSegment(sketch, "E434", {"start": v(-226.02, 87.04) * mm, "end": v(-225.58, 87.4) * mm});
            skLineSegment(sketch, "E435", {"start": v(-225.58, 87.4) * mm, "end": v(-225.13, 87.77) * mm});
            skLineSegment(sketch, "E436", {"start": v(-225.13, 87.77) * mm, "end": v(-224.62, 88.07) * mm});
            skLineSegment(sketch, "E437", {"start": v(-224.62, 88.07) * mm, "end": v(-224.1, 88.3) * mm});
            skLineSegment(sketch, "E438", {"start": v(-224.1, 88.3) * mm, "end": v(-223.59, 88.44) * mm});
            skLineSegment(sketch, "E439", {"start": v(-223.59, 88.44) * mm, "end": v(-223.07, 88.59) * mm});
            skLineSegment(sketch, "E440", {"start": v(-223.07, 88.59) * mm, "end": v(-222.48, 88.66) * mm});
            skLineSegment(sketch, "E441", {"start": v(-222.48, 88.66) * mm, "end": v(-221.9, 88.73) * mm});
            skLineSegment(sketch, "E442", {"start": v(-221.9, 88.73) * mm, "end": v(-221.38, 88.66) * mm});
            skLineSegment(sketch, "E443", {"start": v(-221.38, 88.66) * mm, "end": v(-220.79, 88.59) * mm});
            skLineSegment(sketch, "E444", {"start": v(-220.79, 88.59) * mm, "end": v(-220.27, 88.44) * mm});
            skLineSegment(sketch, "E445", {"start": v(-220.27, 88.44) * mm, "end": v(-219.75, 88.3) * mm});
            skLineSegment(sketch, "E446", {"start": v(-219.75, 88.3) * mm, "end": v(-219.24, 88.07) * mm});
            skLineSegment(sketch, "E447", {"start": v(-219.24, 88.07) * mm, "end": v(-218.72, 87.77) * mm});
            skLineSegment(sketch, "E448", {"start": v(-218.72, 87.77) * mm, "end": v(-218.28, 87.4) * mm});
            skLineSegment(sketch, "E449", {"start": v(-218.28, 87.4) * mm, "end": v(-217.84, 87.04) * mm});
            skLineSegment(sketch, "E450", {"start": v(-217.84, 87.04) * mm, "end": v(-217.47, 86.6) * mm});
            skLineSegment(sketch, "E451", {"start": v(-217.47, 86.6) * mm, "end": v(-217.1, 86.15) * mm});
            skLineSegment(sketch, "E452", {"start": v(-217.1, 86.15) * mm, "end": v(-216.8, 85.64) * mm});
            skLineSegment(sketch, "E453", {"start": v(-216.8, 85.64) * mm, "end": v(-216.58, 85.12) * mm});
            skLineSegment(sketch, "E454", {"start": v(-216.58, 85.12) * mm, "end": v(-216.44, 84.6) * mm});
            skLineSegment(sketch, "E455", {"start": v(-216.44, 84.6) * mm, "end": v(-216.29, 84.09) * mm});
            skLineSegment(sketch, "E456", {"start": v(-216.29, 84.09) * mm, "end": v(-216.22, 83.5) * mm});
            skLineSegment(sketch, "E457", {"start": v(-216.22, 83.5) * mm, "end": v(-216.14, 82.98) * mm});
            skLineSegment(sketch, "E458", {"start": v(-216.14, 82.98) * mm, "end": v(-216.14, 22.54) * mm});
            skLineSegment(sketch, "E459", {"start": v(-216.14, 22.54) * mm, "end": v(-216.22, 22.02) * mm});
            skLineSegment(sketch, "E460", {"start": v(-216.22, 22.02) * mm, "end": v(-216.29, 21.43) * mm});
            skLineSegment(sketch, "E461", {"start": v(-216.29, 21.43) * mm, "end": v(-216.44, 20.92) * mm});
            skLineSegment(sketch, "E462", {"start": v(-216.44, 20.92) * mm, "end": v(-216.58, 20.4) * mm});
            skLineSegment(sketch, "E463", {"start": v(-216.58, 20.4) * mm, "end": v(-216.8, 19.89) * mm});
            skLineSegment(sketch, "E464", {"start": v(-216.8, 19.89) * mm, "end": v(-217.1, 19.37) * mm});
            skLineSegment(sketch, "E465", {"start": v(-217.1, 19.37) * mm, "end": v(-217.47, 18.93) * mm});
            skLineSegment(sketch, "E466", {"start": v(-217.47, 18.93) * mm, "end": v(-217.84, 18.48) * mm});
            skLineSegment(sketch, "E467", {"start": v(-217.84, 18.48) * mm, "end": v(-218.28, 18.12) * mm});
            skLineSegment(sketch, "E468", {"start": v(-218.28, 18.12) * mm, "end": v(-218.72, 17.75) * mm});
            skLineSegment(sketch, "E469", {"start": v(-218.72, 17.75) * mm, "end": v(-219.24, 17.45) * mm});
            skLineSegment(sketch, "E470", {"start": v(-219.24, 17.45) * mm, "end": v(-219.75, 17.23) * mm});
            skLineSegment(sketch, "E471", {"start": v(-219.75, 17.23) * mm, "end": v(-220.27, 17.08) * mm});
            skLineSegment(sketch, "E472", {"start": v(-220.27, 17.08) * mm, "end": v(-220.79, 16.94) * mm});
            skLineSegment(sketch, "E473", {"start": v(-220.79, 16.94) * mm, "end": v(-221.38, 16.86) * mm});
            skLineSegment(sketch, "E474", {"start": v(-221.38, 16.86) * mm, "end": v(-221.9, 16.79) * mm});
            skLineSegment(sketch, "E475", {"start": v(-221.9, 16.79) * mm, "end": v(-237.74, 16.79) * mm});
            skLineSegment(sketch, "E476", {"start": v(-237.74, 16.79) * mm, "end": v(-239.95, 16.94) * mm});
            skLineSegment(sketch, "E477", {"start": v(-239.95, 16.94) * mm, "end": v(-242.01, 17.23) * mm});
            skLineSegment(sketch, "E478", {"start": v(-242.01, 17.23) * mm, "end": v(-244.08, 17.75) * mm});
            skLineSegment(sketch, "E479", {"start": v(-244.08, 17.75) * mm, "end": v(-246, 18.41) * mm});
            skLineSegment(sketch, "E480", {"start": v(-246, 18.41) * mm, "end": v(-247.84, 19.3) * mm});
            skLineSegment(sketch, "E481", {"start": v(-247.84, 19.3) * mm, "end": v(-249.68, 20.4) * mm});
            skLineSegment(sketch, "E482", {"start": v(-249.68, 20.4) * mm, "end": v(-251.38, 21.65) * mm});
            skLineSegment(sketch, "E483", {"start": v(-251.38, 21.65) * mm, "end": v(-253, 23.13) * mm});
            skLineSegment(sketch, "E484", {"start": v(-253, 23.13) * mm, "end": v(-254.47, 24.75) * mm});
            skLineSegment(sketch, "E485", {"start": v(-254.47, 24.75) * mm, "end": v(-255.73, 26.45) * mm});
            skLineSegment(sketch, "E486", {"start": v(-255.73, 26.45) * mm, "end": v(-256.83, 28.29) * mm});
            skLineSegment(sketch, "E487", {"start": v(-256.83, 28.29) * mm, "end": v(-257.72, 30.13) * mm});
            skLineSegment(sketch, "E488", {"start": v(-257.72, 30.13) * mm, "end": v(-258.38, 32.05) * mm});
            skLineSegment(sketch, "E489", {"start": v(-258.38, 32.05) * mm, "end": v(-258.9, 34.11) * mm});
            skLineSegment(sketch, "E490", {"start": v(-258.9, 34.11) * mm, "end": v(-259.19, 36.18) * mm});
            skLineSegment(sketch, "E491", {"start": v(-198.82, 46.42) * mm, "end": v(-198.52, 48.49) * mm});
            skLineSegment(sketch, "E492", {"start": v(-198.52, 48.49) * mm, "end": v(-198, 50.55) * mm});
            skLineSegment(sketch, "E493", {"start": v(-198, 50.55) * mm, "end": v(-197.35, 52.47) * mm});
            skLineSegment(sketch, "E494", {"start": v(-197.35, 52.47) * mm, "end": v(-196.39, 54.3) * mm});
            skLineSegment(sketch, "E495", {"start": v(-196.39, 54.3) * mm, "end": v(-195.35, 56.15) * mm});
            skLineSegment(sketch, "E496", {"start": v(-195.35, 56.15) * mm, "end": v(-194.03, 57.85) * mm});
            skLineSegment(sketch, "E497", {"start": v(-194.03, 57.85) * mm, "end": v(-192.55, 59.47) * mm});
            skLineSegment(sketch, "E498", {"start": v(-192.55, 59.47) * mm, "end": v(-191.15, 60.8) * mm});
            skLineSegment(sketch, "E499", {"start": v(-191.15, 60.8) * mm, "end": v(-189.6, 61.9) * mm});
            skLineSegment(sketch, "E500", {"start": v(-189.6, 61.9) * mm, "end": v(-188.06, 62.93) * mm});
            skLineSegment(sketch, "E501", {"start": v(-188.06, 62.93) * mm, "end": v(-186.44, 63.82) * mm});
            skLineSegment(sketch, "E502", {"start": v(-186.44, 63.82) * mm, "end": v(-184.74, 64.48) * mm});
            skLineSegment(sketch, "E503", {"start": v(-184.74, 64.48) * mm, "end": v(-182.97, 65.07) * mm});
            skLineSegment(sketch, "E504", {"start": v(-182.97, 65.07) * mm, "end": v(-181.13, 65.44) * mm});
            skLineSegment(sketch, "E505", {"start": v(-181.13, 65.44) * mm, "end": v(-179.29, 65.73) * mm});
            skLineSegment(sketch, "E506", {"start": v(-179.29, 65.73) * mm, "end": v(-178.55, 65.66) * mm});
            skLineSegment(sketch, "E507", {"start": v(-178.55, 65.66) * mm, "end": v(-177.89, 65.59) * mm});
            skLineSegment(sketch, "E508", {"start": v(-177.89, 65.59) * mm, "end": v(-177.3, 65.44) * mm});
            skLineSegment(sketch, "E509", {"start": v(-177.3, 65.44) * mm, "end": v(-176.7, 65.3) * mm});
            skLineSegment(sketch, "E510", {"start": v(-176.7, 65.3) * mm, "end": v(-176.12, 65) * mm});
            skLineSegment(sketch, "E511", {"start": v(-176.12, 65) * mm, "end": v(-175.6, 64.7) * mm});
            skLineSegment(sketch, "E512", {"start": v(-175.6, 64.7) * mm, "end": v(-175.16, 64.4) * mm});
            skLineSegment(sketch, "E513", {"start": v(-175.16, 64.4) * mm, "end": v(-174.72, 63.97) * mm});
            skLineSegment(sketch, "E514", {"start": v(-174.72, 63.97) * mm, "end": v(-174.35, 63.52) * mm});
            skLineSegment(sketch, "E515", {"start": v(-174.35, 63.52) * mm, "end": v(-173.98, 63.08) * mm});
            skLineSegment(sketch, "E516", {"start": v(-173.98, 63.08) * mm, "end": v(-173.68, 62.56) * mm});
            skLineSegment(sketch, "E517", {"start": v(-173.68, 62.56) * mm, "end": v(-173.46, 62.12) * mm});
            skLineSegment(sketch, "E518", {"start": v(-173.46, 62.12) * mm, "end": v(-173.24, 61.6) * mm});
            skLineSegment(sketch, "E519", {"start": v(-173.24, 61.6) * mm, "end": v(-173.1, 61.1) * mm});
            skLineSegment(sketch, "E520", {"start": v(-173.1, 61.1) * mm, "end": v(-173.02, 60.5) * mm});
            skLineSegment(sketch, "E521", {"start": v(-173.02, 60.5) * mm, "end": v(-173.02, 59.98) * mm});
            skLineSegment(sketch, "E522", {"start": v(-173.02, 59.98) * mm, "end": v(-173.02, 59.4) * mm});
            skLineSegment(sketch, "E523", {"start": v(-173.02, 59.4) * mm, "end": v(-173.1, 58.8) * mm});
            skLineSegment(sketch, "E524", {"start": v(-173.1, 58.8) * mm, "end": v(-173.24, 58.29) * mm});
            skLineSegment(sketch, "E525", {"start": v(-173.24, 58.29) * mm, "end": v(-173.46, 57.77) * mm});
            skLineSegment(sketch, "E526", {"start": v(-173.46, 57.77) * mm, "end": v(-173.68, 57.26) * mm});
            skLineSegment(sketch, "E527", {"start": v(-173.68, 57.26) * mm, "end": v(-173.98, 56.82) * mm});
            skLineSegment(sketch, "E528", {"start": v(-173.98, 56.82) * mm, "end": v(-174.27, 56.37) * mm});
            skLineSegment(sketch, "E529", {"start": v(-174.27, 56.37) * mm, "end": v(-174.64, 55.93) * mm});
            skLineSegment(sketch, "E530", {"start": v(-174.64, 55.93) * mm, "end": v(-175.08, 55.56) * mm});
            skLineSegment(sketch, "E531", {"start": v(-175.08, 55.56) * mm, "end": v(-175.45, 55.27) * mm});
            skLineSegment(sketch, "E532", {"start": v(-175.45, 55.27) * mm, "end": v(-175.9, 54.97) * mm});
            skLineSegment(sketch, "E533", {"start": v(-175.9, 54.97) * mm, "end": v(-176.34, 54.75) * mm});
            skLineSegment(sketch, "E534", {"start": v(-176.34, 54.75) * mm, "end": v(-176.78, 54.53) * mm});
            skLineSegment(sketch, "E535", {"start": v(-176.78, 54.53) * mm, "end": v(-177.22, 54.38) * mm});
            skLineSegment(sketch, "E536", {"start": v(-177.22, 54.38) * mm, "end": v(-177.66, 54.3) * mm});
            skLineSegment(sketch, "E537", {"start": v(-177.66, 54.3) * mm, "end": v(-178.18, 54.24) * mm});
            skLineSegment(sketch, "E538", {"start": v(-178.18, 54.24) * mm, "end": v(-179.06, 54.09) * mm});
            skLineSegment(sketch, "E539", {"start": v(-179.06, 54.09) * mm, "end": v(-179.95, 53.94) * mm});
            skLineSegment(sketch, "E540", {"start": v(-179.95, 53.94) * mm, "end": v(-180.76, 53.72) * mm});
            skLineSegment(sketch, "E541", {"start": v(-180.76, 53.72) * mm, "end": v(-181.57, 53.35) * mm});
            skLineSegment(sketch, "E542", {"start": v(-181.57, 53.35) * mm, "end": v(-182.3, 52.98) * mm});
            skLineSegment(sketch, "E543", {"start": v(-182.3, 52.98) * mm, "end": v(-183.05, 52.47) * mm});
            skLineSegment(sketch, "E544", {"start": v(-183.05, 52.47) * mm, "end": v(-183.78, 51.95) * mm});
            skLineSegment(sketch, "E545", {"start": v(-183.78, 51.95) * mm, "end": v(-184.45, 51.29) * mm});
            skLineSegment(sketch, "E546", {"start": v(-184.45, 51.29) * mm, "end": v(-185.1, 50.55) * mm});
            skLineSegment(sketch, "E547", {"start": v(-185.1, 50.55) * mm, "end": v(-185.77, 49.74) * mm});
            skLineSegment(sketch, "E548", {"start": v(-185.77, 49.74) * mm, "end": v(-186.21, 48.93) * mm});
            skLineSegment(sketch, "E549", {"start": v(-186.21, 48.93) * mm, "end": v(-186.66, 48.04) * mm});
            skLineSegment(sketch, "E550", {"start": v(-186.66, 48.04) * mm, "end": v(-186.95, 47.16) * mm});
            skLineSegment(sketch, "E551", {"start": v(-186.95, 47.16) * mm, "end": v(-187.25, 46.2) * mm});
            skLineSegment(sketch, "E552", {"start": v(-187.25, 46.2) * mm, "end": v(-187.32, 45.24) * mm});
            skLineSegment(sketch, "E553", {"start": v(-187.32, 45.24) * mm, "end": v(-187.4, 44.21) * mm});
            skLineSegment(sketch, "E554", {"start": v(-187.4, 44.21) * mm, "end": v(-187.4, 38.39) * mm});
            skLineSegment(sketch, "E555", {"start": v(-187.4, 38.39) * mm, "end": v(-187.32, 37.36) * mm});
            skLineSegment(sketch, "E556", {"start": v(-187.32, 37.36) * mm, "end": v(-187.25, 36.4) * mm});
            skLineSegment(sketch, "E557", {"start": v(-187.25, 36.4) * mm, "end": v(-186.95, 35.44) * mm});
            skLineSegment(sketch, "E558", {"start": v(-186.95, 35.44) * mm, "end": v(-186.66, 34.55) * mm});
            skLineSegment(sketch, "E559", {"start": v(-186.66, 34.55) * mm, "end": v(-186.21, 33.67) * mm});
            skLineSegment(sketch, "E560", {"start": v(-186.21, 33.67) * mm, "end": v(-185.77, 32.86) * mm});
            skLineSegment(sketch, "E561", {"start": v(-185.77, 32.86) * mm, "end": v(-185.1, 32.05) * mm});
            skLineSegment(sketch, "E562", {"start": v(-185.1, 32.05) * mm, "end": v(-184.45, 31.24) * mm});
            skLineSegment(sketch, "E563", {"start": v(-184.45, 31.24) * mm, "end": v(-183.7, 30.57) * mm});
            skLineSegment(sketch, "E564", {"start": v(-183.7, 30.57) * mm, "end": v(-182.9, 29.98) * mm});
            skLineSegment(sketch, "E565", {"start": v(-182.9, 29.98) * mm, "end": v(-182.09, 29.47) * mm});
            skLineSegment(sketch, "E566", {"start": v(-182.09, 29.47) * mm, "end": v(-181.2, 29.03) * mm});
            skLineSegment(sketch, "E567", {"start": v(-181.2, 29.03) * mm, "end": v(-180.32, 28.73) * mm});
            skLineSegment(sketch, "E568", {"start": v(-180.32, 28.73) * mm, "end": v(-179.36, 28.5) * mm});
            skLineSegment(sketch, "E569", {"start": v(-179.36, 28.5) * mm, "end": v(-178.33, 28.36) * mm});
            skLineSegment(sketch, "E570", {"start": v(-178.33, 28.36) * mm, "end": v(-177.3, 28.29) * mm});
            skLineSegment(sketch, "E571", {"start": v(-177.3, 28.29) * mm, "end": v(-167.27, 28.29) * mm});
            skLineSegment(sketch, "E572", {"start": v(-167.27, 28.29) * mm, "end": v(-167.27, 68.54) * mm});
            skLineSegment(sketch, "E573", {"start": v(-167.27, 68.54) * mm, "end": v(-167.34, 69.5) * mm});
            skLineSegment(sketch, "E574", {"start": v(-167.34, 69.5) * mm, "end": v(-167.5, 70.53) * mm});
            skLineSegment(sketch, "E575", {"start": v(-167.5, 70.53) * mm, "end": v(-167.71, 71.48) * mm});
            skLineSegment(sketch, "E576", {"start": v(-167.71, 71.48) * mm, "end": v(-168.08, 72.37) * mm});
            skLineSegment(sketch, "E577", {"start": v(-168.08, 72.37) * mm, "end": v(-168.45, 73.25) * mm});
            skLineSegment(sketch, "E578", {"start": v(-168.45, 73.25) * mm, "end": v(-168.97, 74.06) * mm});
            skLineSegment(sketch, "E579", {"start": v(-168.97, 74.06) * mm, "end": v(-169.56, 74.87) * mm});
            skLineSegment(sketch, "E580", {"start": v(-169.56, 74.87) * mm, "end": v(-170.22, 75.61) * mm});
            skLineSegment(sketch, "E581", {"start": v(-170.22, 75.61) * mm, "end": v(-171.03, 76.28) * mm});
            skLineSegment(sketch, "E582", {"start": v(-171.03, 76.28) * mm, "end": v(-171.77, 76.94) * mm});
            skLineSegment(sketch, "E583", {"start": v(-171.77, 76.94) * mm, "end": v(-172.65, 77.38) * mm});
            skLineSegment(sketch, "E584", {"start": v(-172.65, 77.38) * mm, "end": v(-173.46, 77.82) * mm});
            skLineSegment(sketch, "E585", {"start": v(-173.46, 77.82) * mm, "end": v(-174.42, 78.12) * mm});
            skLineSegment(sketch, "E586", {"start": v(-174.42, 78.12) * mm, "end": v(-175.38, 78.41) * mm});
            skLineSegment(sketch, "E587", {"start": v(-175.38, 78.41) * mm, "end": v(-176.34, 78.49) * mm});
            skLineSegment(sketch, "E588", {"start": v(-176.34, 78.49) * mm, "end": v(-177.37, 78.56) * mm});
            skLineSegment(sketch, "E589", {"start": v(-177.37, 78.56) * mm, "end": v(-178.4, 78.49) * mm});
            skLineSegment(sketch, "E590", {"start": v(-178.4, 78.49) * mm, "end": v(-179.43, 78.34) * mm});
            skLineSegment(sketch, "E591", {"start": v(-179.43, 78.34) * mm, "end": v(-180.4, 78.12) * mm});
            skLineSegment(sketch, "E592", {"start": v(-180.4, 78.12) * mm, "end": v(-181.28, 77.82) * mm});
            skLineSegment(sketch, "E593", {"start": v(-181.28, 77.82) * mm, "end": v(-182.16, 77.38) * mm});
            skLineSegment(sketch, "E594", {"start": v(-182.16, 77.38) * mm, "end": v(-183.05, 76.86) * mm});
            skLineSegment(sketch, "E595", {"start": v(-183.05, 76.86) * mm, "end": v(-183.86, 76.28) * mm});
            skLineSegment(sketch, "E596", {"start": v(-183.86, 76.28) * mm, "end": v(-184.67, 75.54) * mm});
            skLineSegment(sketch, "E597", {"start": v(-184.67, 75.54) * mm, "end": v(-185.04, 75.17) * mm});
            skLineSegment(sketch, "E598", {"start": v(-185.04, 75.17) * mm, "end": v(-185.48, 74.8) * mm});
            skLineSegment(sketch, "E599", {"start": v(-185.48, 74.8) * mm, "end": v(-186, 74.5) * mm});
            skLineSegment(sketch, "E600", {"start": v(-186, 74.5) * mm, "end": v(-186.44, 74.28) * mm});
            skLineSegment(sketch, "E601", {"start": v(-186.44, 74.28) * mm, "end": v(-186.95, 74.06) * mm});
            skLineSegment(sketch, "E602", {"start": v(-186.95, 74.06) * mm, "end": v(-187.54, 73.92) * mm});
            skLineSegment(sketch, "E603", {"start": v(-187.54, 73.92) * mm, "end": v(-188.06, 73.84) * mm});
            skLineSegment(sketch, "E604", {"start": v(-188.06, 73.84) * mm, "end": v(-188.72, 73.84) * mm});
            skLineSegment(sketch, "E605", {"start": v(-188.72, 73.84) * mm, "end": v(-189.24, 73.84) * mm});
            skLineSegment(sketch, "E606", {"start": v(-189.24, 73.84) * mm, "end": v(-189.83, 73.92) * mm});
            skLineSegment(sketch, "E607", {"start": v(-189.83, 73.92) * mm, "end": v(-190.34, 74.06) * mm});
            skLineSegment(sketch, "E608", {"start": v(-190.34, 74.06) * mm, "end": v(-190.86, 74.21) * mm});
            skLineSegment(sketch, "E609", {"start": v(-190.86, 74.21) * mm, "end": v(-191.37, 74.5) * mm});
            skLineSegment(sketch, "E610", {"start": v(-191.37, 74.5) * mm, "end": v(-191.9, 74.8) * mm});
            skLineSegment(sketch, "E611", {"start": v(-191.9, 74.8) * mm, "end": v(-192.33, 75.1) * mm});
            skLineSegment(sketch, "E612", {"start": v(-192.33, 75.1) * mm, "end": v(-192.78, 75.54) * mm});
            skLineSegment(sketch, "E613", {"start": v(-192.78, 75.54) * mm, "end": v(-193.14, 75.9) * mm});
            skLineSegment(sketch, "E614", {"start": v(-193.14, 75.9) * mm, "end": v(-193.51, 76.42) * mm});
            skLineSegment(sketch, "E615", {"start": v(-193.51, 76.42) * mm, "end": v(-193.8, 76.86) * mm});
            skLineSegment(sketch, "E616", {"start": v(-193.8, 76.86) * mm, "end": v(-194.03, 77.38) * mm});
            skLineSegment(sketch, "E617", {"start": v(-194.03, 77.38) * mm, "end": v(-194.18, 77.9) * mm});
            skLineSegment(sketch, "E618", {"start": v(-194.18, 77.9) * mm, "end": v(-194.32, 78.41) * mm});
            skLineSegment(sketch, "E619", {"start": v(-194.32, 78.41) * mm, "end": v(-194.4, 79) * mm});
            skLineSegment(sketch, "E620", {"start": v(-194.4, 79) * mm, "end": v(-194.47, 79.6) * mm});
            skLineSegment(sketch, "E621", {"start": v(-194.47, 79.6) * mm, "end": v(-194.4, 80.1) * mm});
            skLineSegment(sketch, "E622", {"start": v(-194.4, 80.1) * mm, "end": v(-194.32, 80.7) * mm});
            skLineSegment(sketch, "E623", {"start": v(-194.32, 80.7) * mm, "end": v(-194.18, 81.21) * mm});
            skLineSegment(sketch, "E624", {"start": v(-194.18, 81.21) * mm, "end": v(-194.03, 81.73) * mm});
            skLineSegment(sketch, "E625", {"start": v(-194.03, 81.73) * mm, "end": v(-193.8, 82.25) * mm});
            skLineSegment(sketch, "E626", {"start": v(-193.8, 82.25) * mm, "end": v(-193.51, 82.69) * mm});
            skLineSegment(sketch, "E627", {"start": v(-193.51, 82.69) * mm, "end": v(-193.14, 83.13) * mm});
            skLineSegment(sketch, "E628", {"start": v(-193.14, 83.13) * mm, "end": v(-192.78, 83.57) * mm});
            skLineSegment(sketch, "E629", {"start": v(-192.78, 83.57) * mm, "end": v(-191.15, 85.12) * mm});
            skLineSegment(sketch, "E630", {"start": v(-191.15, 85.12) * mm, "end": v(-189.38, 86.45) * mm});
            skLineSegment(sketch, "E631", {"start": v(-189.38, 86.45) * mm, "end": v(-187.62, 87.55) * mm});
            skLineSegment(sketch, "E632", {"start": v(-187.62, 87.55) * mm, "end": v(-185.7, 88.51) * mm});
            skLineSegment(sketch, "E633", {"start": v(-185.7, 88.51) * mm, "end": v(-183.7, 89.25) * mm});
            skLineSegment(sketch, "E634", {"start": v(-183.7, 89.25) * mm, "end": v(-181.72, 89.7) * mm});
            skLineSegment(sketch, "E635", {"start": v(-181.72, 89.7) * mm, "end": v(-179.58, 90.06) * mm});
            skLineSegment(sketch, "E636", {"start": v(-179.58, 90.06) * mm, "end": v(-177.37, 90.13) * mm});
            skLineSegment(sketch, "E637", {"start": v(-177.37, 90.13) * mm, "end": v(-175.23, 90.06) * mm});
            skLineSegment(sketch, "E638", {"start": v(-175.23, 90.06) * mm, "end": v(-173.1, 89.76) * mm});
            skLineSegment(sketch, "E639", {"start": v(-173.1, 89.76) * mm, "end": v(-171.1, 89.25) * mm});
            skLineSegment(sketch, "E640", {"start": v(-171.1, 89.25) * mm, "end": v(-169.11, 88.59) * mm});
            skLineSegment(sketch, "E641", {"start": v(-169.11, 88.59) * mm, "end": v(-167.27, 87.63) * mm});
            skLineSegment(sketch, "E642", {"start": v(-167.27, 87.63) * mm, "end": v(-165.5, 86.6) * mm});
            skLineSegment(sketch, "E643", {"start": v(-165.5, 86.6) * mm, "end": v(-163.8, 85.27) * mm});
            skLineSegment(sketch, "E644", {"start": v(-163.8, 85.27) * mm, "end": v(-162.18, 83.8) * mm});
            skLineSegment(sketch, "E645", {"start": v(-162.18, 83.8) * mm, "end": v(-160.71, 82.17) * mm});
            skLineSegment(sketch, "E646", {"start": v(-160.71, 82.17) * mm, "end": v(-159.38, 80.48) * mm});
            skLineSegment(sketch, "E647", {"start": v(-159.38, 80.48) * mm, "end": v(-158.28, 78.7) * mm});
            skLineSegment(sketch, "E648", {"start": v(-158.28, 78.7) * mm, "end": v(-157.4, 76.8) * mm});
            skLineSegment(sketch, "E649", {"start": v(-157.4, 76.8) * mm, "end": v(-156.73, 74.87) * mm});
            skLineSegment(sketch, "E650", {"start": v(-156.73, 74.87) * mm, "end": v(-156.21, 72.81) * mm});
            skLineSegment(sketch, "E651", {"start": v(-156.21, 72.81) * mm, "end": v(-155.92, 70.67) * mm});
            skLineSegment(sketch, "E652", {"start": v(-155.92, 70.67) * mm, "end": v(-155.77, 68.54) * mm});
            skLineSegment(sketch, "E653", {"start": v(-155.77, 68.54) * mm, "end": v(-155.77, 22.54) * mm});
            skLineSegment(sketch, "E654", {"start": v(-155.77, 22.54) * mm, "end": v(-155.77, 22.02) * mm});
            skLineSegment(sketch, "E655", {"start": v(-155.77, 22.02) * mm, "end": v(-155.85, 21.43) * mm});
            skLineSegment(sketch, "E656", {"start": v(-155.85, 21.43) * mm, "end": v(-156, 20.92) * mm});
            skLineSegment(sketch, "E657", {"start": v(-156, 20.92) * mm, "end": v(-156.21, 20.4) * mm});
            skLineSegment(sketch, "E658", {"start": v(-156.21, 20.4) * mm, "end": v(-156.43, 19.89) * mm});
            skLineSegment(sketch, "E659", {"start": v(-156.43, 19.89) * mm, "end": v(-156.73, 19.37) * mm});
            skLineSegment(sketch, "E660", {"start": v(-156.73, 19.37) * mm, "end": v(-157.1, 18.93) * mm});
            skLineSegment(sketch, "E661", {"start": v(-157.1, 18.93) * mm, "end": v(-157.47, 18.48) * mm});
            skLineSegment(sketch, "E662", {"start": v(-157.47, 18.48) * mm, "end": v(-157.9, 18.12) * mm});
            skLineSegment(sketch, "E663", {"start": v(-157.9, 18.12) * mm, "end": v(-158.35, 17.75) * mm});
            skLineSegment(sketch, "E664", {"start": v(-158.35, 17.75) * mm, "end": v(-158.8, 17.45) * mm});
            skLineSegment(sketch, "E665", {"start": v(-158.8, 17.45) * mm, "end": v(-159.3, 17.23) * mm});
            skLineSegment(sketch, "E666", {"start": v(-159.3, 17.23) * mm, "end": v(-159.83, 17.08) * mm});
            skLineSegment(sketch, "E667", {"start": v(-159.83, 17.08) * mm, "end": v(-160.34, 16.94) * mm});
            skLineSegment(sketch, "E668", {"start": v(-160.34, 16.94) * mm, "end": v(-160.93, 16.86) * mm});
            skLineSegment(sketch, "E669", {"start": v(-160.93, 16.86) * mm, "end": v(-161.52, 16.79) * mm});
            skLineSegment(sketch, "E670", {"start": v(-161.52, 16.79) * mm, "end": v(-177.3, 16.79) * mm});
            skLineSegment(sketch, "E671", {"start": v(-177.3, 16.79) * mm, "end": v(-179.5, 16.94) * mm});
            skLineSegment(sketch, "E672", {"start": v(-179.5, 16.94) * mm, "end": v(-181.64, 17.23) * mm});
            skLineSegment(sketch, "E673", {"start": v(-181.64, 17.23) * mm, "end": v(-183.63, 17.75) * mm});
            skLineSegment(sketch, "E674", {"start": v(-183.63, 17.75) * mm, "end": v(-185.62, 18.41) * mm});
            skLineSegment(sketch, "E675", {"start": v(-185.62, 18.41) * mm, "end": v(-187.47, 19.3) * mm});
            skLineSegment(sketch, "E676", {"start": v(-187.47, 19.3) * mm, "end": v(-189.24, 20.4) * mm});
            skLineSegment(sketch, "E677", {"start": v(-189.24, 20.4) * mm, "end": v(-190.93, 21.65) * mm});
            skLineSegment(sketch, "E678", {"start": v(-190.93, 21.65) * mm, "end": v(-192.55, 23.13) * mm});
            skLineSegment(sketch, "E679", {"start": v(-192.55, 23.13) * mm, "end": v(-194.03, 24.75) * mm});
            skLineSegment(sketch, "E680", {"start": v(-194.03, 24.75) * mm, "end": v(-195.35, 26.45) * mm});
            skLineSegment(sketch, "E681", {"start": v(-195.35, 26.45) * mm, "end": v(-196.39, 28.29) * mm});
            skLineSegment(sketch, "E682", {"start": v(-196.39, 28.29) * mm, "end": v(-197.35, 30.13) * mm});
            skLineSegment(sketch, "E683", {"start": v(-197.35, 30.13) * mm, "end": v(-198, 32.05) * mm});
            skLineSegment(sketch, "E684", {"start": v(-198, 32.05) * mm, "end": v(-198.52, 34.11) * mm});
            skLineSegment(sketch, "E685", {"start": v(-198.52, 34.11) * mm, "end": v(-198.82, 36.18) * mm});
            skLineSegment(sketch, "E686", {"start": v(-198.82, 36.18) * mm, "end": v(-198.9, 38.39) * mm});
            skLineSegment(sketch, "E687", {"start": v(-198.9, 38.39) * mm, "end": v(-198.9, 44.21) * mm});
            skLineSegment(sketch, "E688", {"start": v(-198.9, 44.21) * mm, "end": v(-198.82, 46.42) * mm});
            skLineSegment(sketch, "E689", {"start": v(-139.85, 21.43) * mm, "end": v(-139.92, 22.02) * mm});
            skLineSegment(sketch, "E690", {"start": v(-139.92, 22.02) * mm, "end": v(-139.92, 22.54) * mm});
            skLineSegment(sketch, "E691", {"start": v(-139.92, 22.54) * mm, "end": v(-139.92, 82.98) * mm});
            skLineSegment(sketch, "E692", {"start": v(-139.92, 82.98) * mm, "end": v(-139.92, 83.5) * mm});
            skLineSegment(sketch, "E693", {"start": v(-139.92, 83.5) * mm, "end": v(-139.85, 84.09) * mm});
            skLineSegment(sketch, "E694", {"start": v(-139.85, 84.09) * mm, "end": v(-139.7, 84.6) * mm});
            skLineSegment(sketch, "E695", {"start": v(-139.7, 84.6) * mm, "end": v(-139.48, 85.12) * mm});
            skLineSegment(sketch, "E696", {"start": v(-139.48, 85.12) * mm, "end": v(-139.26, 85.64) * mm});
            skLineSegment(sketch, "E697", {"start": v(-139.26, 85.64) * mm, "end": v(-138.97, 86.15) * mm});
            skLineSegment(sketch, "E698", {"start": v(-138.97, 86.15) * mm, "end": v(-138.6, 86.6) * mm});
            skLineSegment(sketch, "E699", {"start": v(-138.6, 86.6) * mm, "end": v(-138.23, 87.04) * mm});
            skLineSegment(sketch, "E700", {"start": v(-138.23, 87.04) * mm, "end": v(-137.79, 87.4) * mm});
            skLineSegment(sketch, "E701", {"start": v(-137.79, 87.4) * mm, "end": v(-137.34, 87.77) * mm});
            skLineSegment(sketch, "E702", {"start": v(-137.34, 87.77) * mm, "end": v(-136.9, 88.07) * mm});
            skLineSegment(sketch, "E703", {"start": v(-136.9, 88.07) * mm, "end": v(-136.39, 88.3) * mm});
            skLineSegment(sketch, "E704", {"start": v(-136.39, 88.3) * mm, "end": v(-135.87, 88.44) * mm});
            skLineSegment(sketch, "E705", {"start": v(-135.87, 88.44) * mm, "end": v(-135.35, 88.59) * mm});
            skLineSegment(sketch, "E706", {"start": v(-135.35, 88.59) * mm, "end": v(-134.76, 88.66) * mm});
            skLineSegment(sketch, "E707", {"start": v(-134.76, 88.66) * mm, "end": v(-134.17, 88.73) * mm});
            skLineSegment(sketch, "E708", {"start": v(-134.17, 88.73) * mm, "end": v(-118.4, 88.73) * mm});
            skLineSegment(sketch, "E709", {"start": v(-118.4, 88.73) * mm, "end": v(-116.19, 88.59) * mm});
            skLineSegment(sketch, "E710", {"start": v(-116.19, 88.59) * mm, "end": v(-114.05, 88.3) * mm});
            skLineSegment(sketch, "E711", {"start": v(-114.05, 88.3) * mm, "end": v(-112.06, 87.77) * mm});
            skLineSegment(sketch, "E712", {"start": v(-112.06, 87.77) * mm, "end": v(-110.07, 87.11) * mm});
            skLineSegment(sketch, "E713", {"start": v(-110.07, 87.11) * mm, "end": v(-108.23, 86.23) * mm});
            skLineSegment(sketch, "E714", {"start": v(-108.23, 86.23) * mm, "end": v(-106.46, 85.12) * mm});
            skLineSegment(sketch, "E715", {"start": v(-106.46, 85.12) * mm, "end": v(-104.76, 83.87) * mm});
            skLineSegment(sketch, "E716", {"start": v(-104.76, 83.87) * mm, "end": v(-103.14, 82.4) * mm});
            skLineSegment(sketch, "E717", {"start": v(-103.14, 82.4) * mm, "end": v(-101.67, 80.77) * mm});
            skLineSegment(sketch, "E718", {"start": v(-101.67, 80.77) * mm, "end": v(-100.34, 79.08) * mm});
            skLineSegment(sketch, "E719", {"start": v(-100.34, 79.08) * mm, "end": v(-99.3, 77.23) * mm});
            skLineSegment(sketch, "E720", {"start": v(-99.3, 77.23) * mm, "end": v(-98.35, 75.4) * mm});
            skLineSegment(sketch, "E721", {"start": v(-98.35, 75.4) * mm, "end": v(-97.69, 73.47) * mm});
            skLineSegment(sketch, "E722", {"start": v(-97.69, 73.47) * mm, "end": v(-97.17, 71.41) * mm});
            skLineSegment(sketch, "E723", {"start": v(-97.17, 71.41) * mm, "end": v(-96.88, 69.35) * mm});
            skLineSegment(sketch, "E724", {"start": v(-96.88, 69.35) * mm, "end": v(-96.8, 67.13) * mm});
            skLineSegment(sketch, "E725", {"start": v(-96.8, 67.13) * mm, "end": v(-96.8, 22.54) * mm});
            skLineSegment(sketch, "E726", {"start": v(-96.8, 22.54) * mm, "end": v(-96.8, 22.02) * mm});
            skLineSegment(sketch, "E727", {"start": v(-96.8, 22.02) * mm, "end": v(-96.88, 21.43) * mm});
            skLineSegment(sketch, "E728", {"start": v(-96.88, 21.43) * mm, "end": v(-97.02, 20.92) * mm});
            skLineSegment(sketch, "E729", {"start": v(-97.02, 20.92) * mm, "end": v(-97.24, 20.4) * mm});
            skLineSegment(sketch, "E730", {"start": v(-97.24, 20.4) * mm, "end": v(-97.47, 19.89) * mm});
            skLineSegment(sketch, "E731", {"start": v(-97.47, 19.89) * mm, "end": v(-97.76, 19.37) * mm});
            skLineSegment(sketch, "E732", {"start": v(-97.76, 19.37) * mm, "end": v(-98.13, 18.93) * mm});
            skLineSegment(sketch, "E733", {"start": v(-98.13, 18.93) * mm, "end": v(-98.5, 18.48) * mm});
            skLineSegment(sketch, "E734", {"start": v(-98.5, 18.48) * mm, "end": v(-98.94, 18.12) * mm});
            skLineSegment(sketch, "E735", {"start": v(-98.94, 18.12) * mm, "end": v(-99.38, 17.75) * mm});
            skLineSegment(sketch, "E736", {"start": v(-99.38, 17.75) * mm, "end": v(-99.82, 17.45) * mm});
            skLineSegment(sketch, "E737", {"start": v(-99.82, 17.45) * mm, "end": v(-100.34, 17.23) * mm});
            skLineSegment(sketch, "E738", {"start": v(-100.34, 17.23) * mm, "end": v(-100.86, 17.08) * mm});
            skLineSegment(sketch, "E739", {"start": v(-100.86, 17.08) * mm, "end": v(-101.37, 16.94) * mm});
            skLineSegment(sketch, "E740", {"start": v(-101.37, 16.94) * mm, "end": v(-101.96, 16.86) * mm});
            skLineSegment(sketch, "E741", {"start": v(-101.96, 16.86) * mm, "end": v(-102.55, 16.79) * mm});
            skLineSegment(sketch, "E742", {"start": v(-102.55, 16.79) * mm, "end": v(-103.14, 16.86) * mm});
            skLineSegment(sketch, "E743", {"start": v(-103.14, 16.86) * mm, "end": v(-103.73, 16.94) * mm});
            skLineSegment(sketch, "E744", {"start": v(-103.73, 16.94) * mm, "end": v(-104.25, 17.08) * mm});
            skLineSegment(sketch, "E745", {"start": v(-104.25, 17.08) * mm, "end": v(-104.76, 17.23) * mm});
            skLineSegment(sketch, "E746", {"start": v(-104.76, 17.23) * mm, "end": v(-105.28, 17.45) * mm});
            skLineSegment(sketch, "E747", {"start": v(-105.28, 17.45) * mm, "end": v(-105.72, 17.75) * mm});
            skLineSegment(sketch, "E748", {"start": v(-105.72, 17.75) * mm, "end": v(-106.16, 18.12) * mm});
            skLineSegment(sketch, "E749", {"start": v(-106.16, 18.12) * mm, "end": v(-106.6, 18.48) * mm});
            skLineSegment(sketch, "E750", {"start": v(-106.6, 18.48) * mm, "end": v(-106.97, 18.93) * mm});
            skLineSegment(sketch, "E751", {"start": v(-106.97, 18.93) * mm, "end": v(-107.34, 19.37) * mm});
            skLineSegment(sketch, "E752", {"start": v(-107.34, 19.37) * mm, "end": v(-107.64, 19.89) * mm});
            skLineSegment(sketch, "E753", {"start": v(-107.64, 19.89) * mm, "end": v(-107.86, 20.4) * mm});
            skLineSegment(sketch, "E754", {"start": v(-107.86, 20.4) * mm, "end": v(-108.08, 20.92) * mm});
            skLineSegment(sketch, "E755", {"start": v(-108.08, 20.92) * mm, "end": v(-108.23, 21.43) * mm});
            skLineSegment(sketch, "E756", {"start": v(-108.23, 21.43) * mm, "end": v(-108.3, 22.02) * mm});
            skLineSegment(sketch, "E757", {"start": v(-108.3, 22.02) * mm, "end": v(-108.3, 22.54) * mm});
            skLineSegment(sketch, "E758", {"start": v(-108.3, 22.54) * mm, "end": v(-108.3, 67.13) * mm});
            skLineSegment(sketch, "E759", {"start": v(-108.3, 67.13) * mm, "end": v(-108.37, 68.17) * mm});
            skLineSegment(sketch, "E760", {"start": v(-108.37, 68.17) * mm, "end": v(-108.45, 69.13) * mm});
            skLineSegment(sketch, "E761", {"start": v(-108.45, 69.13) * mm, "end": v(-108.74, 70.08) * mm});
            skLineSegment(sketch, "E762", {"start": v(-108.74, 70.08) * mm, "end": v(-109.04, 70.97) * mm});
            skLineSegment(sketch, "E763", {"start": v(-109.04, 70.97) * mm, "end": v(-109.48, 71.85) * mm});
            skLineSegment(sketch, "E764", {"start": v(-109.48, 71.85) * mm, "end": v(-109.92, 72.66) * mm});
            skLineSegment(sketch, "E765", {"start": v(-109.92, 72.66) * mm, "end": v(-110.59, 73.47) * mm});
            skLineSegment(sketch, "E766", {"start": v(-110.59, 73.47) * mm, "end": v(-111.25, 74.28) * mm});
            skLineSegment(sketch, "E767", {"start": v(-111.25, 74.28) * mm, "end": v(-111.99, 74.95) * mm});
            skLineSegment(sketch, "E768", {"start": v(-111.99, 74.95) * mm, "end": v(-112.8, 75.54) * mm});
            skLineSegment(sketch, "E769", {"start": v(-112.8, 75.54) * mm, "end": v(-113.6, 76.05) * mm});
            skLineSegment(sketch, "E770", {"start": v(-113.6, 76.05) * mm, "end": v(-114.5, 76.5) * mm});
            skLineSegment(sketch, "E771", {"start": v(-114.5, 76.5) * mm, "end": v(-115.38, 76.8) * mm});
            skLineSegment(sketch, "E772", {"start": v(-115.38, 76.8) * mm, "end": v(-116.34, 77.01) * mm});
            skLineSegment(sketch, "E773", {"start": v(-116.34, 77.01) * mm, "end": v(-117.37, 77.16) * mm});
            skLineSegment(sketch, "E774", {"start": v(-117.37, 77.16) * mm, "end": v(-118.4, 77.23) * mm});
            skLineSegment(sketch, "E775", {"start": v(-118.4, 77.23) * mm, "end": v(-128.42, 77.23) * mm});
            skLineSegment(sketch, "E776", {"start": v(-128.42, 77.23) * mm, "end": v(-128.42, 22.54) * mm});
            skLineSegment(sketch, "E777", {"start": v(-128.42, 22.54) * mm, "end": v(-128.42, 22.02) * mm});
            skLineSegment(sketch, "E778", {"start": v(-128.42, 22.02) * mm, "end": v(-128.5, 21.43) * mm});
            skLineSegment(sketch, "E779", {"start": v(-128.5, 21.43) * mm, "end": v(-128.65, 20.92) * mm});
            skLineSegment(sketch, "E780", {"start": v(-128.65, 20.92) * mm, "end": v(-128.87, 20.4) * mm});
            skLineSegment(sketch, "E781", {"start": v(-128.87, 20.4) * mm, "end": v(-129.09, 19.89) * mm});
            skLineSegment(sketch, "E782", {"start": v(-129.09, 19.89) * mm, "end": v(-129.38, 19.37) * mm});
            skLineSegment(sketch, "E783", {"start": v(-129.38, 19.37) * mm, "end": v(-129.75, 18.93) * mm});
            skLineSegment(sketch, "E784", {"start": v(-129.75, 18.93) * mm, "end": v(-130.12, 18.48) * mm});
            skLineSegment(sketch, "E785", {"start": v(-130.12, 18.48) * mm, "end": v(-130.56, 18.12) * mm});
            skLineSegment(sketch, "E786", {"start": v(-130.56, 18.12) * mm, "end": v(-131, 17.75) * mm});
            skLineSegment(sketch, "E787", {"start": v(-131, 17.75) * mm, "end": v(-131.45, 17.45) * mm});
            skLineSegment(sketch, "E788", {"start": v(-131.45, 17.45) * mm, "end": v(-131.96, 17.23) * mm});
            skLineSegment(sketch, "E789", {"start": v(-131.96, 17.23) * mm, "end": v(-132.48, 17.08) * mm});
            skLineSegment(sketch, "E790", {"start": v(-132.48, 17.08) * mm, "end": v(-133, 16.94) * mm});
            skLineSegment(sketch, "E791", {"start": v(-133, 16.94) * mm, "end": v(-133.58, 16.86) * mm});
            skLineSegment(sketch, "E792", {"start": v(-133.58, 16.86) * mm, "end": v(-134.17, 16.79) * mm});
            skLineSegment(sketch, "E793", {"start": v(-134.17, 16.79) * mm, "end": v(-134.76, 16.86) * mm});
            skLineSegment(sketch, "E794", {"start": v(-134.76, 16.86) * mm, "end": v(-135.35, 16.94) * mm});
            skLineSegment(sketch, "E795", {"start": v(-135.35, 16.94) * mm, "end": v(-135.87, 17.08) * mm});
            skLineSegment(sketch, "E796", {"start": v(-135.87, 17.08) * mm, "end": v(-136.39, 17.23) * mm});
            skLineSegment(sketch, "E797", {"start": v(-136.39, 17.23) * mm, "end": v(-136.9, 17.45) * mm});
            skLineSegment(sketch, "E798", {"start": v(-136.9, 17.45) * mm, "end": v(-137.34, 17.75) * mm});
            skLineSegment(sketch, "E799", {"start": v(-137.34, 17.75) * mm, "end": v(-137.79, 18.12) * mm});
            skLineSegment(sketch, "E800", {"start": v(-137.79, 18.12) * mm, "end": v(-138.23, 18.48) * mm});
            skLineSegment(sketch, "E801", {"start": v(-138.23, 18.48) * mm, "end": v(-138.6, 18.93) * mm});
            skLineSegment(sketch, "E802", {"start": v(-138.6, 18.93) * mm, "end": v(-138.97, 19.37) * mm});
            skLineSegment(sketch, "E803", {"start": v(-138.97, 19.37) * mm, "end": v(-139.26, 19.89) * mm});
            skLineSegment(sketch, "E804", {"start": v(-139.26, 19.89) * mm, "end": v(-139.48, 20.4) * mm});
            skLineSegment(sketch, "E805", {"start": v(-139.48, 20.4) * mm, "end": v(-139.7, 20.92) * mm});
            skLineSegment(sketch, "E806", {"start": v(-139.7, 20.92) * mm, "end": v(-139.85, 21.43) * mm});
            skLineSegment(sketch, "E807", {"start": v(-82.35, 81.8) * mm, "end": v(-82.43, 82.4) * mm});
            skLineSegment(sketch, "E808", {"start": v(-82.43, 82.4) * mm, "end": v(-82.43, 82.98) * mm});
            skLineSegment(sketch, "E809", {"start": v(-82.43, 82.98) * mm, "end": v(-82.43, 83.5) * mm});
            skLineSegment(sketch, "E810", {"start": v(-82.43, 83.5) * mm, "end": v(-82.35, 84.09) * mm});
            skLineSegment(sketch, "E811", {"start": v(-82.35, 84.09) * mm, "end": v(-82.2, 84.6) * mm});
            skLineSegment(sketch, "E812", {"start": v(-82.2, 84.6) * mm, "end": v(-82.06, 85.12) * mm});
            skLineSegment(sketch, "E813", {"start": v(-82.06, 85.12) * mm, "end": v(-81.76, 85.64) * mm});
            skLineSegment(sketch, "E814", {"start": v(-81.76, 85.64) * mm, "end": v(-81.47, 86.15) * mm});
            skLineSegment(sketch, "E815", {"start": v(-81.47, 86.15) * mm, "end": v(-81.17, 86.6) * mm});
            skLineSegment(sketch, "E816", {"start": v(-81.17, 86.6) * mm, "end": v(-80.73, 87.04) * mm});
            skLineSegment(sketch, "E817", {"start": v(-80.73, 87.04) * mm, "end": v(-80.44, 87.33) * mm});
            skLineSegment(sketch, "E818", {"start": v(-80.44, 87.33) * mm, "end": v(-80.14, 87.55) * mm});
            skLineSegment(sketch, "E819", {"start": v(-80.14, 87.55) * mm, "end": v(-79.85, 87.77) * mm});
            skLineSegment(sketch, "E820", {"start": v(-79.85, 87.77) * mm, "end": v(-79.48, 88) * mm});
            skLineSegment(sketch, "E821", {"start": v(-79.48, 88) * mm, "end": v(-79.18, 88.14) * mm});
            skLineSegment(sketch, "E822", {"start": v(-79.18, 88.14) * mm, "end": v(-78.82, 88.3) * mm});
            skLineSegment(sketch, "E823", {"start": v(-78.82, 88.3) * mm, "end": v(-78.45, 88.44) * mm});
            skLineSegment(sketch, "E824", {"start": v(-78.45, 88.44) * mm, "end": v(-78.08, 88.59) * mm});
            skLineSegment(sketch, "E825", {"start": v(-78.08, 88.59) * mm, "end": v(-78.08, 100.16) * mm});
            skLineSegment(sketch, "E826", {"start": v(-78.08, 100.16) * mm, "end": v(-78.08, 100.67) * mm});
            skLineSegment(sketch, "E827", {"start": v(-78.08, 100.67) * mm, "end": v(-78, 101.26) * mm});
            skLineSegment(sketch, "E828", {"start": v(-78, 101.26) * mm, "end": v(-77.86, 101.78) * mm});
            skLineSegment(sketch, "E829", {"start": v(-77.86, 101.78) * mm, "end": v(-77.64, 102.3) * mm});
            skLineSegment(sketch, "E830", {"start": v(-77.64, 102.3) * mm, "end": v(-77.42, 102.81) * mm});
            skLineSegment(sketch, "E831", {"start": v(-77.42, 102.81) * mm, "end": v(-77.12, 103.33) * mm});
            skLineSegment(sketch, "E832", {"start": v(-77.12, 103.33) * mm, "end": v(-76.75, 103.77) * mm});
            skLineSegment(sketch, "E833", {"start": v(-76.75, 103.77) * mm, "end": v(-76.38, 104.21) * mm});
            skLineSegment(sketch, "E834", {"start": v(-76.38, 104.21) * mm, "end": v(-75.94, 104.58) * mm});
            skLineSegment(sketch, "E835", {"start": v(-75.94, 104.58) * mm, "end": v(-75.43, 104.95) * mm});
            skLineSegment(sketch, "E836", {"start": v(-75.43, 104.95) * mm, "end": v(-74.98, 105.24) * mm});
            skLineSegment(sketch, "E837", {"start": v(-74.98, 105.24) * mm, "end": v(-74.47, 105.47) * mm});
            skLineSegment(sketch, "E838", {"start": v(-74.47, 105.47) * mm, "end": v(-73.95, 105.61) * mm});
            skLineSegment(sketch, "E839", {"start": v(-73.95, 105.61) * mm, "end": v(-73.44, 105.76) * mm});
            skLineSegment(sketch, "E840", {"start": v(-73.44, 105.76) * mm, "end": v(-72.92, 105.83) * mm});
            skLineSegment(sketch, "E841", {"start": v(-72.92, 105.83) * mm, "end": v(-72.33, 105.9) * mm});
            skLineSegment(sketch, "E842", {"start": v(-72.33, 105.9) * mm, "end": v(-71.74, 105.83) * mm});
            skLineSegment(sketch, "E843", {"start": v(-71.74, 105.83) * mm, "end": v(-71.15, 105.76) * mm});
            skLineSegment(sketch, "E844", {"start": v(-71.15, 105.76) * mm, "end": v(-70.63, 105.61) * mm});
            skLineSegment(sketch, "E845", {"start": v(-70.63, 105.61) * mm, "end": v(-70.12, 105.47) * mm});
            skLineSegment(sketch, "E846", {"start": v(-70.12, 105.47) * mm, "end": v(-69.6, 105.24) * mm});
            skLineSegment(sketch, "E847", {"start": v(-69.6, 105.24) * mm, "end": v(-69.16, 104.95) * mm});
            skLineSegment(sketch, "E848", {"start": v(-69.16, 104.95) * mm, "end": v(-68.72, 104.58) * mm});
            skLineSegment(sketch, "E849", {"start": v(-68.72, 104.58) * mm, "end": v(-68.28, 104.21) * mm});
            skLineSegment(sketch, "E850", {"start": v(-68.28, 104.21) * mm, "end": v(-67.9, 103.77) * mm});
            skLineSegment(sketch, "E851", {"start": v(-67.9, 103.77) * mm, "end": v(-67.54, 103.33) * mm});
            skLineSegment(sketch, "E852", {"start": v(-67.54, 103.33) * mm, "end": v(-67.24, 102.81) * mm});
            skLineSegment(sketch, "E853", {"start": v(-67.24, 102.81) * mm, "end": v(-67.02, 102.3) * mm});
            skLineSegment(sketch, "E854", {"start": v(-67.02, 102.3) * mm, "end": v(-66.8, 101.78) * mm});
            skLineSegment(sketch, "E855", {"start": v(-66.8, 101.78) * mm, "end": v(-66.65, 101.26) * mm});
            skLineSegment(sketch, "E856", {"start": v(-66.65, 101.26) * mm, "end": v(-66.58, 100.67) * mm});
            skLineSegment(sketch, "E857", {"start": v(-66.58, 100.67) * mm, "end": v(-66.58, 100.16) * mm});
            skLineSegment(sketch, "E858", {"start": v(-66.58, 100.16) * mm, "end": v(-66.58, 88.73) * mm});
            skLineSegment(sketch, "E859", {"start": v(-66.58, 88.73) * mm, "end": v(-59.36, 88.73) * mm});
            skLineSegment(sketch, "E860", {"start": v(-59.36, 88.73) * mm, "end": v(-58.84, 88.66) * mm});
            skLineSegment(sketch, "E861", {"start": v(-58.84, 88.66) * mm, "end": v(-58.25, 88.59) * mm});
            skLineSegment(sketch, "E862", {"start": v(-58.25, 88.59) * mm, "end": v(-57.73, 88.44) * mm});
            skLineSegment(sketch, "E863", {"start": v(-57.73, 88.44) * mm, "end": v(-57.22, 88.3) * mm});
            skLineSegment(sketch, "E864", {"start": v(-57.22, 88.3) * mm, "end": v(-56.7, 88.07) * mm});
            skLineSegment(sketch, "E865", {"start": v(-56.7, 88.07) * mm, "end": v(-56.19, 87.77) * mm});
            skLineSegment(sketch, "E866", {"start": v(-56.19, 87.77) * mm, "end": v(-55.74, 87.4) * mm});
            skLineSegment(sketch, "E867", {"start": v(-55.74, 87.4) * mm, "end": v(-55.3, 87.04) * mm});
            skLineSegment(sketch, "E868", {"start": v(-55.3, 87.04) * mm, "end": v(-54.93, 86.6) * mm});
            skLineSegment(sketch, "E869", {"start": v(-54.93, 86.6) * mm, "end": v(-54.56, 86.15) * mm});
            skLineSegment(sketch, "E870", {"start": v(-54.56, 86.15) * mm, "end": v(-54.27, 85.64) * mm});
            skLineSegment(sketch, "E871", {"start": v(-54.27, 85.64) * mm, "end": v(-54.05, 85.12) * mm});
            skLineSegment(sketch, "E872", {"start": v(-54.05, 85.12) * mm, "end": v(-53.9, 84.6) * mm});
            skLineSegment(sketch, "E873", {"start": v(-53.9, 84.6) * mm, "end": v(-53.75, 84.09) * mm});
            skLineSegment(sketch, "E874", {"start": v(-53.75, 84.09) * mm, "end": v(-53.68, 83.5) * mm});
            skLineSegment(sketch, "E875", {"start": v(-53.68, 83.5) * mm, "end": v(-53.6, 82.98) * mm});
            skLineSegment(sketch, "E876", {"start": v(-53.6, 82.98) * mm, "end": v(-53.68, 82.4) * mm});
            skLineSegment(sketch, "E877", {"start": v(-53.68, 82.4) * mm, "end": v(-53.75, 81.8) * mm});
            skLineSegment(sketch, "E878", {"start": v(-53.75, 81.8) * mm, "end": v(-53.9, 81.29) * mm});
            skLineSegment(sketch, "E879", {"start": v(-53.9, 81.29) * mm, "end": v(-54.05, 80.77) * mm});
            skLineSegment(sketch, "E880", {"start": v(-54.05, 80.77) * mm, "end": v(-54.27, 80.26) * mm});
            skLineSegment(sketch, "E881", {"start": v(-54.27, 80.26) * mm, "end": v(-54.56, 79.74) * mm});
            skLineSegment(sketch, "E882", {"start": v(-54.56, 79.74) * mm, "end": v(-54.93, 79.3) * mm});
            skLineSegment(sketch, "E883", {"start": v(-54.93, 79.3) * mm, "end": v(-55.3, 78.86) * mm});
            skLineSegment(sketch, "E884", {"start": v(-55.3, 78.86) * mm, "end": v(-55.74, 78.49) * mm});
            skLineSegment(sketch, "E885", {"start": v(-55.74, 78.49) * mm, "end": v(-56.19, 78.12) * mm});
            skLineSegment(sketch, "E886", {"start": v(-56.19, 78.12) * mm, "end": v(-56.7, 77.82) * mm});
            skLineSegment(sketch, "E887", {"start": v(-56.7, 77.82) * mm, "end": v(-57.22, 77.6) * mm});
            skLineSegment(sketch, "E888", {"start": v(-57.22, 77.6) * mm, "end": v(-57.73, 77.45) * mm});
            skLineSegment(sketch, "E889", {"start": v(-57.73, 77.45) * mm, "end": v(-58.25, 77.3) * mm});
            skLineSegment(sketch, "E890", {"start": v(-58.25, 77.3) * mm, "end": v(-58.84, 77.23) * mm});
            skLineSegment(sketch, "E891", {"start": v(-58.84, 77.23) * mm, "end": v(-59.36, 77.23) * mm});
            skLineSegment(sketch, "E892", {"start": v(-59.36, 77.23) * mm, "end": v(-66.58, 77.23) * mm});
            skLineSegment(sketch, "E893", {"start": v(-66.58, 77.23) * mm, "end": v(-66.58, 35.51) * mm});
            skLineSegment(sketch, "E894", {"start": v(-66.58, 35.51) * mm, "end": v(-66.58, 34.78) * mm});
            skLineSegment(sketch, "E895", {"start": v(-66.58, 34.78) * mm, "end": v(-66.43, 34.04) * mm});
            skLineSegment(sketch, "E896", {"start": v(-66.43, 34.04) * mm, "end": v(-66.28, 33.37) * mm});
            skLineSegment(sketch, "E897", {"start": v(-66.28, 33.37) * mm, "end": v(-66.06, 32.71) * mm});
            skLineSegment(sketch, "E898", {"start": v(-66.06, 32.71) * mm, "end": v(-65.77, 32.12) * mm});
            skLineSegment(sketch, "E899", {"start": v(-65.77, 32.12) * mm, "end": v(-65.4, 31.53) * mm});
            skLineSegment(sketch, "E900", {"start": v(-65.4, 31.53) * mm, "end": v(-64.96, 30.94) * mm});
            skLineSegment(sketch, "E901", {"start": v(-64.96, 30.94) * mm, "end": v(-64.52, 30.43) * mm});
            skLineSegment(sketch, "E902", {"start": v(-64.52, 30.43) * mm, "end": v(-63.93, 29.91) * mm});
            skLineSegment(sketch, "E903", {"start": v(-63.93, 29.91) * mm, "end": v(-63.41, 29.47) * mm});
            skLineSegment(sketch, "E904", {"start": v(-63.41, 29.47) * mm, "end": v(-62.82, 29.17) * mm});
            skLineSegment(sketch, "E905", {"start": v(-62.82, 29.17) * mm, "end": v(-62.16, 28.88) * mm});
            skLineSegment(sketch, "E906", {"start": v(-62.16, 28.88) * mm, "end": v(-61.5, 28.58) * mm});
            skLineSegment(sketch, "E907", {"start": v(-61.5, 28.58) * mm, "end": v(-60.83, 28.44) * mm});
            skLineSegment(sketch, "E908", {"start": v(-60.83, 28.44) * mm, "end": v(-60.17, 28.36) * mm});
            skLineSegment(sketch, "E909", {"start": v(-60.17, 28.36) * mm, "end": v(-59.36, 28.29) * mm});
            skLineSegment(sketch, "E910", {"start": v(-59.36, 28.29) * mm, "end": v(-58.77, 28.29) * mm});
            skLineSegment(sketch, "E911", {"start": v(-58.77, 28.29) * mm, "end": v(-58.25, 28.21) * mm});
            skLineSegment(sketch, "E912", {"start": v(-58.25, 28.21) * mm, "end": v(-57.66, 28.07) * mm});
            skLineSegment(sketch, "E913", {"start": v(-57.66, 28.07) * mm, "end": v(-57.14, 27.92) * mm});
            skLineSegment(sketch, "E914", {"start": v(-57.14, 27.92) * mm, "end": v(-56.63, 27.63) * mm});
            skLineSegment(sketch, "E915", {"start": v(-56.63, 27.63) * mm, "end": v(-56.19, 27.33) * mm});
            skLineSegment(sketch, "E916", {"start": v(-56.19, 27.33) * mm, "end": v(-55.67, 27.04) * mm});
            skLineSegment(sketch, "E917", {"start": v(-55.67, 27.04) * mm, "end": v(-55.23, 26.6) * mm});
            skLineSegment(sketch, "E918", {"start": v(-55.23, 26.6) * mm, "end": v(-54.86, 26.15) * mm});
            skLineSegment(sketch, "E919", {"start": v(-54.86, 26.15) * mm, "end": v(-54.5, 25.7) * mm});
            skLineSegment(sketch, "E920", {"start": v(-54.5, 25.7) * mm, "end": v(-54.2, 25.2) * mm});
            skLineSegment(sketch, "E921", {"start": v(-54.2, 25.2) * mm, "end": v(-53.97, 24.75) * mm});
            skLineSegment(sketch, "E922", {"start": v(-53.97, 24.75) * mm, "end": v(-53.83, 24.23) * mm});
            skLineSegment(sketch, "E923", {"start": v(-53.83, 24.23) * mm, "end": v(-53.68, 23.72) * mm});
            skLineSegment(sketch, "E924", {"start": v(-53.68, 23.72) * mm, "end": v(-53.6, 23.13) * mm});
            skLineSegment(sketch, "E925", {"start": v(-53.6, 23.13) * mm, "end": v(-53.6, 22.54) * mm});
            skLineSegment(sketch, "E926", {"start": v(-53.6, 22.54) * mm, "end": v(-53.6, 22.02) * mm});
            skLineSegment(sketch, "E927", {"start": v(-53.6, 22.02) * mm, "end": v(-53.68, 21.43) * mm});
            skLineSegment(sketch, "E928", {"start": v(-53.68, 21.43) * mm, "end": v(-53.83, 20.92) * mm});
            skLineSegment(sketch, "E929", {"start": v(-53.83, 20.92) * mm, "end": v(-53.97, 20.4) * mm});
            skLineSegment(sketch, "E930", {"start": v(-53.97, 20.4) * mm, "end": v(-54.2, 19.89) * mm});
            skLineSegment(sketch, "E931", {"start": v(-54.2, 19.89) * mm, "end": v(-54.5, 19.37) * mm});
            skLineSegment(sketch, "E932", {"start": v(-54.5, 19.37) * mm, "end": v(-54.86, 18.93) * mm});
            skLineSegment(sketch, "E933", {"start": v(-54.86, 18.93) * mm, "end": v(-55.23, 18.48) * mm});
            skLineSegment(sketch, "E934", {"start": v(-55.23, 18.48) * mm, "end": v(-55.67, 18.12) * mm});
            skLineSegment(sketch, "E935", {"start": v(-55.67, 18.12) * mm, "end": v(-56.19, 17.75) * mm});
            skLineSegment(sketch, "E936", {"start": v(-56.19, 17.75) * mm, "end": v(-56.63, 17.45) * mm});
            skLineSegment(sketch, "E937", {"start": v(-56.63, 17.45) * mm, "end": v(-57.14, 17.23) * mm});
            skLineSegment(sketch, "E938", {"start": v(-57.14, 17.23) * mm, "end": v(-57.66, 17.08) * mm});
            skLineSegment(sketch, "E939", {"start": v(-57.66, 17.08) * mm, "end": v(-58.25, 16.94) * mm});
            skLineSegment(sketch, "E940", {"start": v(-58.25, 16.94) * mm, "end": v(-58.77, 16.86) * mm});
            skLineSegment(sketch, "E941", {"start": v(-58.77, 16.86) * mm, "end": v(-59.36, 16.79) * mm});
            skLineSegment(sketch, "E942", {"start": v(-59.36, 16.79) * mm, "end": v(-61.27, 16.94) * mm});
            skLineSegment(sketch, "E943", {"start": v(-61.27, 16.94) * mm, "end": v(-63.12, 17.16) * mm});
            skLineSegment(sketch, "E944", {"start": v(-63.12, 17.16) * mm, "end": v(-64.88, 17.6) * mm});
            skLineSegment(sketch, "E945", {"start": v(-64.88, 17.6) * mm, "end": v(-66.5, 18.19) * mm});
            skLineSegment(sketch, "E946", {"start": v(-66.5, 18.19) * mm, "end": v(-68.13, 19) * mm});
            skLineSegment(sketch, "E947", {"start": v(-68.13, 19) * mm, "end": v(-69.68, 19.89) * mm});
            skLineSegment(sketch, "E948", {"start": v(-69.68, 19.89) * mm, "end": v(-71.15, 21.06) * mm});
            skLineSegment(sketch, "E949", {"start": v(-71.15, 21.06) * mm, "end": v(-72.55, 22.32) * mm});
            skLineSegment(sketch, "E950", {"start": v(-72.55, 22.32) * mm, "end": v(-73.88, 23.72) * mm});
            skLineSegment(sketch, "E951", {"start": v(-73.88, 23.72) * mm, "end": v(-74.98, 25.2) * mm});
            skLineSegment(sketch, "E952", {"start": v(-74.98, 25.2) * mm, "end": v(-75.94, 26.74) * mm});
            skLineSegment(sketch, "E953", {"start": v(-75.94, 26.74) * mm, "end": v(-76.68, 28.36) * mm});
            skLineSegment(sketch, "E954", {"start": v(-76.68, 28.36) * mm, "end": v(-77.34, 30.06) * mm});
            skLineSegment(sketch, "E955", {"start": v(-77.34, 30.06) * mm, "end": v(-77.71, 31.83) * mm});
            skLineSegment(sketch, "E956", {"start": v(-77.71, 31.83) * mm, "end": v(-78, 33.6) * mm});
            skLineSegment(sketch, "E957", {"start": v(-78, 33.6) * mm, "end": v(-78.08, 35.51) * mm});
            skLineSegment(sketch, "E958", {"start": v(-78.08, 35.51) * mm, "end": v(-78.08, 77.3) * mm});
            skLineSegment(sketch, "E959", {"start": v(-78.08, 77.3) * mm, "end": v(-78.45, 77.45) * mm});
            skLineSegment(sketch, "E960", {"start": v(-78.45, 77.45) * mm, "end": v(-78.82, 77.6) * mm});
            skLineSegment(sketch, "E961", {"start": v(-78.82, 77.6) * mm, "end": v(-79.18, 77.75) * mm});
            skLineSegment(sketch, "E962", {"start": v(-79.18, 77.75) * mm, "end": v(-79.48, 77.9) * mm});
            skLineSegment(sketch, "E963", {"start": v(-79.48, 77.9) * mm, "end": v(-79.85, 78.12) * mm});
            skLineSegment(sketch, "E964", {"start": v(-79.85, 78.12) * mm, "end": v(-80.14, 78.34) * mm});
            skLineSegment(sketch, "E965", {"start": v(-80.14, 78.34) * mm, "end": v(-80.44, 78.63) * mm});
            skLineSegment(sketch, "E966", {"start": v(-80.44, 78.63) * mm, "end": v(-80.73, 78.93) * mm});
            skLineSegment(sketch, "E967", {"start": v(-80.73, 78.93) * mm, "end": v(-81.17, 79.37) * mm});
            skLineSegment(sketch, "E968", {"start": v(-81.17, 79.37) * mm, "end": v(-81.47, 79.81) * mm});
            skLineSegment(sketch, "E969", {"start": v(-81.47, 79.81) * mm, "end": v(-81.76, 80.33) * mm});
            skLineSegment(sketch, "E970", {"start": v(-81.76, 80.33) * mm, "end": v(-82.06, 80.77) * mm});
            skLineSegment(sketch, "E971", {"start": v(-82.06, 80.77) * mm, "end": v(-82.2, 81.29) * mm});
            skLineSegment(sketch, "E972", {"start": v(-82.2, 81.29) * mm, "end": v(-82.35, 81.8) * mm});
            skLineSegment(sketch, "E973", {"start": v(-42.03, 36.18) * mm, "end": v(-42.18, 38.39) * mm});
            skLineSegment(sketch, "E974", {"start": v(-42.18, 38.39) * mm, "end": v(-42.18, 82.98) * mm});
            skLineSegment(sketch, "E975", {"start": v(-42.18, 82.98) * mm, "end": v(-42.1, 83.5) * mm});
            skLineSegment(sketch, "E976", {"start": v(-42.1, 83.5) * mm, "end": v(-42.03, 84.09) * mm});
            skLineSegment(sketch, "E977", {"start": v(-42.03, 84.09) * mm, "end": v(-41.89, 84.6) * mm});
            skLineSegment(sketch, "E978", {"start": v(-41.89, 84.6) * mm, "end": v(-41.74, 85.12) * mm});
            skLineSegment(sketch, "E979", {"start": v(-41.74, 85.12) * mm, "end": v(-41.52, 85.64) * mm});
            skLineSegment(sketch, "E980", {"start": v(-41.52, 85.64) * mm, "end": v(-41.22, 86.15) * mm});
            skLineSegment(sketch, "E981", {"start": v(-41.22, 86.15) * mm, "end": v(-40.85, 86.6) * mm});
            skLineSegment(sketch, "E982", {"start": v(-40.85, 86.6) * mm, "end": v(-40.49, 87.04) * mm});
            skLineSegment(sketch, "E983", {"start": v(-40.49, 87.04) * mm, "end": v(-40.04, 87.4) * mm});
            skLineSegment(sketch, "E984", {"start": v(-40.04, 87.4) * mm, "end": v(-39.6, 87.77) * mm});
            skLineSegment(sketch, "E985", {"start": v(-39.6, 87.77) * mm, "end": v(-39.09, 88.07) * mm});
            skLineSegment(sketch, "E986", {"start": v(-39.09, 88.07) * mm, "end": v(-38.57, 88.3) * mm});
            skLineSegment(sketch, "E987", {"start": v(-38.57, 88.3) * mm, "end": v(-38.05, 88.44) * mm});
            skLineSegment(sketch, "E988", {"start": v(-38.05, 88.44) * mm, "end": v(-37.54, 88.59) * mm});
            skLineSegment(sketch, "E989", {"start": v(-37.54, 88.59) * mm, "end": v(-36.95, 88.66) * mm});
            skLineSegment(sketch, "E990", {"start": v(-36.95, 88.66) * mm, "end": v(-36.43, 88.73) * mm});
            skLineSegment(sketch, "E991", {"start": v(-36.43, 88.73) * mm, "end": v(-35.84, 88.66) * mm});
            skLineSegment(sketch, "E992", {"start": v(-35.84, 88.66) * mm, "end": v(-35.25, 88.59) * mm});
            skLineSegment(sketch, "E993", {"start": v(-35.25, 88.59) * mm, "end": v(-34.74, 88.44) * mm});
            skLineSegment(sketch, "E994", {"start": v(-34.74, 88.44) * mm, "end": v(-34.22, 88.3) * mm});
            skLineSegment(sketch, "E995", {"start": v(-34.22, 88.3) * mm, "end": v(-33.7, 88.07) * mm});
            skLineSegment(sketch, "E996", {"start": v(-33.7, 88.07) * mm, "end": v(-33.19, 87.77) * mm});
            skLineSegment(sketch, "E997", {"start": v(-33.19, 87.77) * mm, "end": v(-32.75, 87.4) * mm});
            skLineSegment(sketch, "E998", {"start": v(-32.75, 87.4) * mm, "end": v(-32.3, 87.04) * mm});
            skLineSegment(sketch, "E999", {"start": v(-32.3, 87.04) * mm, "end": v(-31.94, 86.6) * mm});
            skLineSegment(sketch, "E1000", {"start": v(-31.94, 86.6) * mm, "end": v(-31.57, 86.15) * mm});
            skLineSegment(sketch, "E1001", {"start": v(-31.57, 86.15) * mm, "end": v(-31.27, 85.64) * mm});
            skLineSegment(sketch, "E1002", {"start": v(-31.27, 85.64) * mm, "end": v(-31.05, 85.12) * mm});
            skLineSegment(sketch, "E1003", {"start": v(-31.05, 85.12) * mm, "end": v(-30.9, 84.6) * mm});
            skLineSegment(sketch, "E1004", {"start": v(-30.9, 84.6) * mm, "end": v(-30.76, 84.09) * mm});
            skLineSegment(sketch, "E1005", {"start": v(-30.76, 84.09) * mm, "end": v(-30.68, 83.5) * mm});
            skLineSegment(sketch, "E1006", {"start": v(-30.68, 83.5) * mm, "end": v(-30.68, 82.98) * mm});
            skLineSegment(sketch, "E1007", {"start": v(-30.68, 82.98) * mm, "end": v(-30.68, 38.39) * mm});
            skLineSegment(sketch, "E1008", {"start": v(-30.68, 38.39) * mm, "end": v(-30.6, 37.36) * mm});
            skLineSegment(sketch, "E1009", {"start": v(-30.6, 37.36) * mm, "end": v(-30.46, 36.4) * mm});
            skLineSegment(sketch, "E1010", {"start": v(-30.46, 36.4) * mm, "end": v(-30.24, 35.44) * mm});
            skLineSegment(sketch, "E1011", {"start": v(-30.24, 35.44) * mm, "end": v(-29.94, 34.55) * mm});
            skLineSegment(sketch, "E1012", {"start": v(-29.94, 34.55) * mm, "end": v(-29.5, 33.67) * mm});
            skLineSegment(sketch, "E1013", {"start": v(-29.5, 33.67) * mm, "end": v(-28.99, 32.86) * mm});
            skLineSegment(sketch, "E1014", {"start": v(-28.99, 32.86) * mm, "end": v(-28.4, 32.05) * mm});
            skLineSegment(sketch, "E1015", {"start": v(-28.4, 32.05) * mm, "end": v(-27.73, 31.24) * mm});
            skLineSegment(sketch, "E1016", {"start": v(-27.73, 31.24) * mm, "end": v(-26.92, 30.57) * mm});
            skLineSegment(sketch, "E1017", {"start": v(-26.92, 30.57) * mm, "end": v(-26.11, 29.98) * mm});
            skLineSegment(sketch, "E1018", {"start": v(-26.11, 29.98) * mm, "end": v(-25.3, 29.47) * mm});
            skLineSegment(sketch, "E1019", {"start": v(-25.3, 29.47) * mm, "end": v(-24.42, 29.03) * mm});
            skLineSegment(sketch, "E1020", {"start": v(-24.42, 29.03) * mm, "end": v(-23.53, 28.73) * mm});
            skLineSegment(sketch, "E1021", {"start": v(-23.53, 28.73) * mm, "end": v(-22.57, 28.5) * mm});
            skLineSegment(sketch, "E1022", {"start": v(-22.57, 28.5) * mm, "end": v(-21.62, 28.36) * mm});
            skLineSegment(sketch, "E1023", {"start": v(-21.62, 28.36) * mm, "end": v(-20.58, 28.29) * mm});
            skLineSegment(sketch, "E1024", {"start": v(-20.58, 28.29) * mm, "end": v(-10.48, 28.29) * mm});
            skLineSegment(sketch, "E1025", {"start": v(-10.48, 28.29) * mm, "end": v(-10.48, 82.98) * mm});
            skLineSegment(sketch, "E1026", {"start": v(-10.48, 82.98) * mm, "end": v(-10.48, 83.5) * mm});
            skLineSegment(sketch, "E1027", {"start": v(-10.48, 83.5) * mm, "end": v(-10.41, 84.09) * mm});
            skLineSegment(sketch, "E1028", {"start": v(-10.41, 84.09) * mm, "end": v(-10.26, 84.6) * mm});
            skLineSegment(sketch, "E1029", {"start": v(-10.26, 84.6) * mm, "end": v(-10.12, 85.12) * mm});
            skLineSegment(sketch, "E1030", {"start": v(-10.12, 85.12) * mm, "end": v(-9.9, 85.64) * mm});
            skLineSegment(sketch, "E1031", {"start": v(-9.9, 85.64) * mm, "end": v(-9.6, 86.15) * mm});
            skLineSegment(sketch, "E1032", {"start": v(-9.6, 86.15) * mm, "end": v(-9.23, 86.6) * mm});
            skLineSegment(sketch, "E1033", {"start": v(-9.23, 86.6) * mm, "end": v(-8.86, 87.04) * mm});
            skLineSegment(sketch, "E1034", {"start": v(-8.86, 87.04) * mm, "end": v(-8.42, 87.4) * mm});
            skLineSegment(sketch, "E1035", {"start": v(-8.42, 87.4) * mm, "end": v(-7.98, 87.77) * mm});
            skLineSegment(sketch, "E1036", {"start": v(-7.98, 87.77) * mm, "end": v(-7.46, 88.07) * mm});
            skLineSegment(sketch, "E1037", {"start": v(-7.46, 88.07) * mm, "end": v(-6.95, 88.3) * mm});
            skLineSegment(sketch, "E1038", {"start": v(-6.95, 88.3) * mm, "end": v(-6.43, 88.44) * mm});
            skLineSegment(sketch, "E1039", {"start": v(-6.43, 88.44) * mm, "end": v(-5.91, 88.59) * mm});
            skLineSegment(sketch, "E1040", {"start": v(-5.91, 88.59) * mm, "end": v(-5.32, 88.66) * mm});
            skLineSegment(sketch, "E1041", {"start": v(-5.32, 88.66) * mm, "end": v(-4.74, 88.73) * mm});
            skLineSegment(sketch, "E1042", {"start": v(-4.74, 88.73) * mm, "end": v(-4.22, 88.66) * mm});
            skLineSegment(sketch, "E1043", {"start": v(-4.22, 88.66) * mm, "end": v(-3.63, 88.59) * mm});
            skLineSegment(sketch, "E1044", {"start": v(-3.63, 88.59) * mm, "end": v(-3.11, 88.44) * mm});
            skLineSegment(sketch, "E1045", {"start": v(-3.11, 88.44) * mm, "end": v(-2.6, 88.3) * mm});
            skLineSegment(sketch, "E1046", {"start": v(-2.6, 88.3) * mm, "end": v(-2.08, 88.07) * mm});
            skLineSegment(sketch, "E1047", {"start": v(-2.08, 88.07) * mm, "end": v(-1.57, 87.77) * mm});
            skLineSegment(sketch, "E1048", {"start": v(-1.57, 87.77) * mm, "end": v(-1.12, 87.4) * mm});
            skLineSegment(sketch, "E1049", {"start": v(-1.12, 87.4) * mm, "end": v(-0.68, 87.04) * mm});
            skLineSegment(sketch, "E1050", {"start": v(-0.68, 87.04) * mm, "end": v(-0.31, 86.6) * mm});
            skLineSegment(sketch, "E1051", {"start": v(-0.31, 86.6) * mm, "end": v(0.06, 86.15) * mm});
            skLineSegment(sketch, "E1052", {"start": v(0.06, 86.15) * mm, "end": v(0.35, 85.64) * mm});
            skLineSegment(sketch, "E1053", {"start": v(0.35, 85.64) * mm, "end": v(0.57, 85.12) * mm});
            skLineSegment(sketch, "E1054", {"start": v(0.57, 85.12) * mm, "end": v(0.72, 84.6) * mm});
            skLineSegment(sketch, "E1055", {"start": v(0.72, 84.6) * mm, "end": v(0.87, 84.09) * mm});
            skLineSegment(sketch, "E1056", {"start": v(0.87, 84.09) * mm, "end": v(0.94, 83.5) * mm});
            skLineSegment(sketch, "E1057", {"start": v(0.94, 83.5) * mm, "end": v(1.01, 82.98) * mm});
            skLineSegment(sketch, "E1058", {"start": v(1.01, 82.98) * mm, "end": v(1.01, 22.54) * mm});
            skLineSegment(sketch, "E1059", {"start": v(1.01, 22.54) * mm, "end": v(0.94, 22.02) * mm});
            skLineSegment(sketch, "E1060", {"start": v(0.94, 22.02) * mm, "end": v(0.87, 21.43) * mm});
            skLineSegment(sketch, "E1061", {"start": v(0.87, 21.43) * mm, "end": v(0.72, 20.92) * mm});
            skLineSegment(sketch, "E1062", {"start": v(0.72, 20.92) * mm, "end": v(0.57, 20.4) * mm});
            skLineSegment(sketch, "E1063", {"start": v(0.57, 20.4) * mm, "end": v(0.35, 19.89) * mm});
            skLineSegment(sketch, "E1064", {"start": v(0.35, 19.89) * mm, "end": v(0.06, 19.37) * mm});
            skLineSegment(sketch, "E1065", {"start": v(0.06, 19.37) * mm, "end": v(-0.31, 18.93) * mm});
            skLineSegment(sketch, "E1066", {"start": v(-0.31, 18.93) * mm, "end": v(-0.68, 18.48) * mm});
            skLineSegment(sketch, "E1067", {"start": v(-0.68, 18.48) * mm, "end": v(-1.12, 18.12) * mm});
            skLineSegment(sketch, "E1068", {"start": v(-1.12, 18.12) * mm, "end": v(-1.57, 17.75) * mm});
            skLineSegment(sketch, "E1069", {"start": v(-1.57, 17.75) * mm, "end": v(-2.08, 17.45) * mm});
            skLineSegment(sketch, "E1070", {"start": v(-2.08, 17.45) * mm, "end": v(-2.6, 17.23) * mm});
            skLineSegment(sketch, "E1071", {"start": v(-2.6, 17.23) * mm, "end": v(-3.11, 17.08) * mm});
            skLineSegment(sketch, "E1072", {"start": v(-3.11, 17.08) * mm, "end": v(-3.63, 16.94) * mm});
            skLineSegment(sketch, "E1073", {"start": v(-3.63, 16.94) * mm, "end": v(-4.22, 16.86) * mm});
            skLineSegment(sketch, "E1074", {"start": v(-4.22, 16.86) * mm, "end": v(-4.74, 16.79) * mm});
            skLineSegment(sketch, "E1075", {"start": v(-4.74, 16.79) * mm, "end": v(-20.58, 16.79) * mm});
            skLineSegment(sketch, "E1076", {"start": v(-20.58, 16.79) * mm, "end": v(-22.8, 16.94) * mm});
            skLineSegment(sketch, "E1077", {"start": v(-22.8, 16.94) * mm, "end": v(-24.86, 17.23) * mm});
            skLineSegment(sketch, "E1078", {"start": v(-24.86, 17.23) * mm, "end": v(-26.92, 17.75) * mm});
            skLineSegment(sketch, "E1079", {"start": v(-26.92, 17.75) * mm, "end": v(-28.84, 18.41) * mm});
            skLineSegment(sketch, "E1080", {"start": v(-28.84, 18.41) * mm, "end": v(-30.68, 19.3) * mm});
            skLineSegment(sketch, "E1081", {"start": v(-30.68, 19.3) * mm, "end": v(-32.52, 20.4) * mm});
            skLineSegment(sketch, "E1082", {"start": v(-32.52, 20.4) * mm, "end": v(-34.22, 21.65) * mm});
            skLineSegment(sketch, "E1083", {"start": v(-34.22, 21.65) * mm, "end": v(-35.84, 23.13) * mm});
            skLineSegment(sketch, "E1084", {"start": v(-35.84, 23.13) * mm, "end": v(-37.32, 24.75) * mm});
            skLineSegment(sketch, "E1085", {"start": v(-37.32, 24.75) * mm, "end": v(-38.57, 26.45) * mm});
            skLineSegment(sketch, "E1086", {"start": v(-38.57, 26.45) * mm, "end": v(-39.67, 28.29) * mm});
            skLineSegment(sketch, "E1087", {"start": v(-39.67, 28.29) * mm, "end": v(-40.56, 30.13) * mm});
            skLineSegment(sketch, "E1088", {"start": v(-40.56, 30.13) * mm, "end": v(-41.22, 32.05) * mm});
            skLineSegment(sketch, "E1089", {"start": v(-41.22, 32.05) * mm, "end": v(-41.74, 34.11) * mm});
            skLineSegment(sketch, "E1090", {"start": v(-41.74, 34.11) * mm, "end": v(-42.03, 36.18) * mm});
            skLineSegment(sketch, "E1091", {"start": v(21.21, 21.43) * mm, "end": v(21.14, 22.02) * mm});
            skLineSegment(sketch, "E1092", {"start": v(21.14, 22.02) * mm, "end": v(21.14, 22.54) * mm});
            skLineSegment(sketch, "E1093", {"start": v(21.14, 22.54) * mm, "end": v(21.14, 82.98) * mm});
            skLineSegment(sketch, "E1094", {"start": v(21.14, 82.98) * mm, "end": v(21.14, 83.5) * mm});
            skLineSegment(sketch, "E1095", {"start": v(21.14, 83.5) * mm, "end": v(21.21, 84.09) * mm});
            skLineSegment(sketch, "E1096", {"start": v(21.21, 84.09) * mm, "end": v(21.36, 84.6) * mm});
            skLineSegment(sketch, "E1097", {"start": v(21.36, 84.6) * mm, "end": v(21.58, 85.12) * mm});
            skLineSegment(sketch, "E1098", {"start": v(21.58, 85.12) * mm, "end": v(21.8, 85.64) * mm});
            skLineSegment(sketch, "E1099", {"start": v(21.8, 85.64) * mm, "end": v(22.1, 86.15) * mm});
            skLineSegment(sketch, "E1100", {"start": v(22.1, 86.15) * mm, "end": v(22.46, 86.6) * mm});
            skLineSegment(sketch, "E1101", {"start": v(22.46, 86.6) * mm, "end": v(22.83, 87.04) * mm});
            skLineSegment(sketch, "E1102", {"start": v(22.83, 87.04) * mm, "end": v(23.28, 87.4) * mm});
            skLineSegment(sketch, "E1103", {"start": v(23.28, 87.4) * mm, "end": v(23.72, 87.77) * mm});
            skLineSegment(sketch, "E1104", {"start": v(23.72, 87.77) * mm, "end": v(24.16, 88.07) * mm});
            skLineSegment(sketch, "E1105", {"start": v(24.16, 88.07) * mm, "end": v(24.68, 88.3) * mm});
            skLineSegment(sketch, "E1106", {"start": v(24.68, 88.3) * mm, "end": v(25.2, 88.44) * mm});
            skLineSegment(sketch, "E1107", {"start": v(25.2, 88.44) * mm, "end": v(25.7, 88.59) * mm});
            skLineSegment(sketch, "E1108", {"start": v(25.7, 88.59) * mm, "end": v(26.3, 88.66) * mm});
            skLineSegment(sketch, "E1109", {"start": v(26.3, 88.66) * mm, "end": v(26.89, 88.73) * mm});
            skLineSegment(sketch, "E1110", {"start": v(26.89, 88.73) * mm, "end": v(68.6, 88.73) * mm});
            skLineSegment(sketch, "E1111", {"start": v(68.6, 88.73) * mm, "end": v(70.75, 88.59) * mm});
            skLineSegment(sketch, "E1112", {"start": v(70.75, 88.59) * mm, "end": v(72.88, 88.3) * mm});
            skLineSegment(sketch, "E1113", {"start": v(72.88, 88.3) * mm, "end": v(74.87, 87.77) * mm});
            skLineSegment(sketch, "E1114", {"start": v(74.87, 87.77) * mm, "end": v(76.86, 87.11) * mm});
            skLineSegment(sketch, "E1115", {"start": v(76.86, 87.11) * mm, "end": v(78.7, 86.23) * mm});
            skLineSegment(sketch, "E1116", {"start": v(78.7, 86.23) * mm, "end": v(80.48, 85.12) * mm});
            skLineSegment(sketch, "E1117", {"start": v(80.48, 85.12) * mm, "end": v(82.17, 83.87) * mm});
            skLineSegment(sketch, "E1118", {"start": v(82.17, 83.87) * mm, "end": v(83.8, 82.4) * mm});
            skLineSegment(sketch, "E1119", {"start": v(83.8, 82.4) * mm, "end": v(85.27, 80.77) * mm});
            skLineSegment(sketch, "E1120", {"start": v(85.27, 80.77) * mm, "end": v(86.6, 79.08) * mm});
            skLineSegment(sketch, "E1121", {"start": v(86.6, 79.08) * mm, "end": v(87.63, 77.23) * mm});
            skLineSegment(sketch, "E1122", {"start": v(87.63, 77.23) * mm, "end": v(88.58, 75.4) * mm});
            skLineSegment(sketch, "E1123", {"start": v(88.58, 75.4) * mm, "end": v(89.25, 73.47) * mm});
            skLineSegment(sketch, "E1124", {"start": v(89.25, 73.47) * mm, "end": v(89.76, 71.41) * mm});
            skLineSegment(sketch, "E1125", {"start": v(89.76, 71.41) * mm, "end": v(90.06, 69.35) * mm});
            skLineSegment(sketch, "E1126", {"start": v(90.06, 69.35) * mm, "end": v(90.13, 67.13) * mm});
            skLineSegment(sketch, "E1127", {"start": v(90.13, 67.13) * mm, "end": v(90.13, 22.54) * mm});
            skLineSegment(sketch, "E1128", {"start": v(90.13, 22.54) * mm, "end": v(90.13, 22.02) * mm});
            skLineSegment(sketch, "E1129", {"start": v(90.13, 22.02) * mm, "end": v(90.06, 21.43) * mm});
            skLineSegment(sketch, "E1130", {"start": v(90.06, 21.43) * mm, "end": v(89.91, 20.92) * mm});
            skLineSegment(sketch, "E1131", {"start": v(89.91, 20.92) * mm, "end": v(89.7, 20.4) * mm});
            skLineSegment(sketch, "E1132", {"start": v(89.7, 20.4) * mm, "end": v(89.47, 19.89) * mm});
            skLineSegment(sketch, "E1133", {"start": v(89.47, 19.89) * mm, "end": v(89.17, 19.37) * mm});
            skLineSegment(sketch, "E1134", {"start": v(89.17, 19.37) * mm, "end": v(88.8, 18.93) * mm});
            skLineSegment(sketch, "E1135", {"start": v(88.8, 18.93) * mm, "end": v(88.44, 18.48) * mm});
            skLineSegment(sketch, "E1136", {"start": v(88.44, 18.48) * mm, "end": v(88, 18.12) * mm});
            skLineSegment(sketch, "E1137", {"start": v(88, 18.12) * mm, "end": v(87.55, 17.75) * mm});
            skLineSegment(sketch, "E1138", {"start": v(87.55, 17.75) * mm, "end": v(87.11, 17.45) * mm});
            skLineSegment(sketch, "E1139", {"start": v(87.11, 17.45) * mm, "end": v(86.6, 17.23) * mm});
            skLineSegment(sketch, "E1140", {"start": v(86.6, 17.23) * mm, "end": v(86.08, 17.08) * mm});
            skLineSegment(sketch, "E1141", {"start": v(86.08, 17.08) * mm, "end": v(85.56, 16.94) * mm});
            skLineSegment(sketch, "E1142", {"start": v(85.56, 16.94) * mm, "end": v(84.97, 16.86) * mm});
            skLineSegment(sketch, "E1143", {"start": v(84.97, 16.86) * mm, "end": v(84.38, 16.79) * mm});
            skLineSegment(sketch, "E1144", {"start": v(84.38, 16.79) * mm, "end": v(83.8, 16.86) * mm});
            skLineSegment(sketch, "E1145", {"start": v(83.8, 16.86) * mm, "end": v(83.2, 16.94) * mm});
            skLineSegment(sketch, "E1146", {"start": v(83.2, 16.94) * mm, "end": v(82.69, 17.08) * mm});
            skLineSegment(sketch, "E1147", {"start": v(82.69, 17.08) * mm, "end": v(82.17, 17.23) * mm});
            skLineSegment(sketch, "E1148", {"start": v(82.17, 17.23) * mm, "end": v(81.66, 17.45) * mm});
            skLineSegment(sketch, "E1149", {"start": v(81.66, 17.45) * mm, "end": v(81.21, 17.75) * mm});
            skLineSegment(sketch, "E1150", {"start": v(81.21, 17.75) * mm, "end": v(80.77, 18.12) * mm});
            skLineSegment(sketch, "E1151", {"start": v(80.77, 18.12) * mm, "end": v(80.33, 18.48) * mm});
            skLineSegment(sketch, "E1152", {"start": v(80.33, 18.48) * mm, "end": v(79.96, 18.93) * mm});
            skLineSegment(sketch, "E1153", {"start": v(79.96, 18.93) * mm, "end": v(79.6, 19.37) * mm});
            skLineSegment(sketch, "E1154", {"start": v(79.6, 19.37) * mm, "end": v(79.3, 19.89) * mm});
            skLineSegment(sketch, "E1155", {"start": v(79.3, 19.89) * mm, "end": v(79.08, 20.4) * mm});
            skLineSegment(sketch, "E1156", {"start": v(79.08, 20.4) * mm, "end": v(78.85, 20.92) * mm});
            skLineSegment(sketch, "E1157", {"start": v(78.85, 20.92) * mm, "end": v(78.7, 21.43) * mm});
            skLineSegment(sketch, "E1158", {"start": v(78.7, 21.43) * mm, "end": v(78.63, 22.02) * mm});
            skLineSegment(sketch, "E1159", {"start": v(78.63, 22.02) * mm, "end": v(78.63, 22.54) * mm});
            skLineSegment(sketch, "E1160", {"start": v(78.63, 22.54) * mm, "end": v(78.63, 67.13) * mm});
            skLineSegment(sketch, "E1161", {"start": v(78.63, 67.13) * mm, "end": v(78.56, 68.17) * mm});
            skLineSegment(sketch, "E1162", {"start": v(78.56, 68.17) * mm, "end": v(78.49, 69.13) * mm});
            skLineSegment(sketch, "E1163", {"start": v(78.49, 69.13) * mm, "end": v(78.2, 70.08) * mm});
            skLineSegment(sketch, "E1164", {"start": v(78.2, 70.08) * mm, "end": v(77.9, 70.97) * mm});
            skLineSegment(sketch, "E1165", {"start": v(77.9, 70.97) * mm, "end": v(77.45, 71.85) * mm});
            skLineSegment(sketch, "E1166", {"start": v(77.45, 71.85) * mm, "end": v(77.01, 72.66) * mm});
            skLineSegment(sketch, "E1167", {"start": v(77.01, 72.66) * mm, "end": v(76.35, 73.47) * mm});
            skLineSegment(sketch, "E1168", {"start": v(76.35, 73.47) * mm, "end": v(75.68, 74.28) * mm});
            skLineSegment(sketch, "E1169", {"start": v(75.68, 74.28) * mm, "end": v(74.95, 74.95) * mm});
            skLineSegment(sketch, "E1170", {"start": v(74.95, 74.95) * mm, "end": v(74.14, 75.54) * mm});
            skLineSegment(sketch, "E1171", {"start": v(74.14, 75.54) * mm, "end": v(73.33, 76.05) * mm});
            skLineSegment(sketch, "E1172", {"start": v(73.33, 76.05) * mm, "end": v(72.44, 76.5) * mm});
            skLineSegment(sketch, "E1173", {"start": v(72.44, 76.5) * mm, "end": v(71.56, 76.8) * mm});
            skLineSegment(sketch, "E1174", {"start": v(71.56, 76.8) * mm, "end": v(70.6, 77.01) * mm});
            skLineSegment(sketch, "E1175", {"start": v(70.6, 77.01) * mm, "end": v(69.57, 77.16) * mm});
            skLineSegment(sketch, "E1176", {"start": v(69.57, 77.16) * mm, "end": v(68.6, 77.23) * mm});
            skLineSegment(sketch, "E1177", {"start": v(68.6, 77.23) * mm, "end": v(61.38, 77.23) * mm});
            skLineSegment(sketch, "E1178", {"start": v(61.38, 77.23) * mm, "end": v(61.38, 22.54) * mm});
            skLineSegment(sketch, "E1179", {"start": v(61.38, 22.54) * mm, "end": v(61.38, 22.02) * mm});
            skLineSegment(sketch, "E1180", {"start": v(61.38, 22.02) * mm, "end": v(61.31, 21.43) * mm});
            skLineSegment(sketch, "E1181", {"start": v(61.31, 21.43) * mm, "end": v(61.16, 20.92) * mm});
            skLineSegment(sketch, "E1182", {"start": v(61.16, 20.92) * mm, "end": v(60.94, 20.4) * mm});
            skLineSegment(sketch, "E1183", {"start": v(60.94, 20.4) * mm, "end": v(60.72, 19.89) * mm});
            skLineSegment(sketch, "E1184", {"start": v(60.72, 19.89) * mm, "end": v(60.43, 19.37) * mm});
            skLineSegment(sketch, "E1185", {"start": v(60.43, 19.37) * mm, "end": v(60.06, 18.93) * mm});
            skLineSegment(sketch, "E1186", {"start": v(60.06, 18.93) * mm, "end": v(59.69, 18.48) * mm});
            skLineSegment(sketch, "E1187", {"start": v(59.69, 18.48) * mm, "end": v(59.25, 18.12) * mm});
            skLineSegment(sketch, "E1188", {"start": v(59.25, 18.12) * mm, "end": v(58.8, 17.75) * mm});
            skLineSegment(sketch, "E1189", {"start": v(58.8, 17.75) * mm, "end": v(58.36, 17.45) * mm});
            skLineSegment(sketch, "E1190", {"start": v(58.36, 17.45) * mm, "end": v(57.85, 17.23) * mm});
            skLineSegment(sketch, "E1191", {"start": v(57.85, 17.23) * mm, "end": v(57.33, 17.08) * mm});
            skLineSegment(sketch, "E1192", {"start": v(57.33, 17.08) * mm, "end": v(56.81, 16.94) * mm});
            skLineSegment(sketch, "E1193", {"start": v(56.81, 16.94) * mm, "end": v(56.22, 16.86) * mm});
            skLineSegment(sketch, "E1194", {"start": v(56.22, 16.86) * mm, "end": v(55.64, 16.79) * mm});
            skLineSegment(sketch, "E1195", {"start": v(55.64, 16.79) * mm, "end": v(55.05, 16.86) * mm});
            skLineSegment(sketch, "E1196", {"start": v(55.05, 16.86) * mm, "end": v(54.46, 16.94) * mm});
            skLineSegment(sketch, "E1197", {"start": v(54.46, 16.94) * mm, "end": v(53.94, 17.08) * mm});
            skLineSegment(sketch, "E1198", {"start": v(53.94, 17.08) * mm, "end": v(53.42, 17.23) * mm});
            skLineSegment(sketch, "E1199", {"start": v(53.42, 17.23) * mm, "end": v(52.9, 17.45) * mm});
            skLineSegment(sketch, "E1200", {"start": v(52.9, 17.45) * mm, "end": v(52.47, 17.75) * mm});
            skLineSegment(sketch, "E1201", {"start": v(52.47, 17.75) * mm, "end": v(52.02, 18.12) * mm});
            skLineSegment(sketch, "E1202", {"start": v(52.02, 18.12) * mm, "end": v(51.58, 18.48) * mm});
            skLineSegment(sketch, "E1203", {"start": v(51.58, 18.48) * mm, "end": v(51.21, 18.93) * mm});
            skLineSegment(sketch, "E1204", {"start": v(51.21, 18.93) * mm, "end": v(50.84, 19.37) * mm});
            skLineSegment(sketch, "E1205", {"start": v(50.84, 19.37) * mm, "end": v(50.55, 19.89) * mm});
            skLineSegment(sketch, "E1206", {"start": v(50.55, 19.89) * mm, "end": v(50.33, 20.4) * mm});
            skLineSegment(sketch, "E1207", {"start": v(50.33, 20.4) * mm, "end": v(50.1, 20.92) * mm});
            skLineSegment(sketch, "E1208", {"start": v(50.1, 20.92) * mm, "end": v(49.96, 21.43) * mm});
            skLineSegment(sketch, "E1209", {"start": v(49.96, 21.43) * mm, "end": v(49.89, 22.02) * mm});
            skLineSegment(sketch, "E1210", {"start": v(49.89, 22.02) * mm, "end": v(49.89, 22.54) * mm});
            skLineSegment(sketch, "E1211", {"start": v(49.89, 22.54) * mm, "end": v(49.89, 77.23) * mm});
            skLineSegment(sketch, "E1212", {"start": v(49.89, 77.23) * mm, "end": v(32.64, 77.23) * mm});
            skLineSegment(sketch, "E1213", {"start": v(32.64, 77.23) * mm, "end": v(32.64, 22.54) * mm});
            skLineSegment(sketch, "E1214", {"start": v(32.64, 22.54) * mm, "end": v(32.64, 22.02) * mm});
            skLineSegment(sketch, "E1215", {"start": v(32.64, 22.02) * mm, "end": v(32.56, 21.43) * mm});
            skLineSegment(sketch, "E1216", {"start": v(32.56, 21.43) * mm, "end": v(32.42, 20.92) * mm});
            skLineSegment(sketch, "E1217", {"start": v(32.42, 20.92) * mm, "end": v(32.2, 20.4) * mm});
            skLineSegment(sketch, "E1218", {"start": v(32.2, 20.4) * mm, "end": v(31.97, 19.89) * mm});
            skLineSegment(sketch, "E1219", {"start": v(31.97, 19.89) * mm, "end": v(31.68, 19.37) * mm});
            skLineSegment(sketch, "E1220", {"start": v(31.68, 19.37) * mm, "end": v(31.31, 18.93) * mm});
            skLineSegment(sketch, "E1221", {"start": v(31.31, 18.93) * mm, "end": v(30.94, 18.48) * mm});
            skLineSegment(sketch, "E1222", {"start": v(30.94, 18.48) * mm, "end": v(30.5, 18.12) * mm});
            skLineSegment(sketch, "E1223", {"start": v(30.5, 18.12) * mm, "end": v(30.06, 17.75) * mm});
            skLineSegment(sketch, "E1224", {"start": v(30.06, 17.75) * mm, "end": v(29.61, 17.45) * mm});
            skLineSegment(sketch, "E1225", {"start": v(29.61, 17.45) * mm, "end": v(29.1, 17.23) * mm});
            skLineSegment(sketch, "E1226", {"start": v(29.1, 17.23) * mm, "end": v(28.58, 17.08) * mm});
            skLineSegment(sketch, "E1227", {"start": v(28.58, 17.08) * mm, "end": v(28.07, 16.94) * mm});
            skLineSegment(sketch, "E1228", {"start": v(28.07, 16.94) * mm, "end": v(27.48, 16.86) * mm});
            skLineSegment(sketch, "E1229", {"start": v(27.48, 16.86) * mm, "end": v(26.89, 16.79) * mm});
            skLineSegment(sketch, "E1230", {"start": v(26.89, 16.79) * mm, "end": v(26.3, 16.86) * mm});
            skLineSegment(sketch, "E1231", {"start": v(26.3, 16.86) * mm, "end": v(25.7, 16.94) * mm});
            skLineSegment(sketch, "E1232", {"start": v(25.7, 16.94) * mm, "end": v(25.2, 17.08) * mm});
            skLineSegment(sketch, "E1233", {"start": v(25.2, 17.08) * mm, "end": v(24.68, 17.23) * mm});
            skLineSegment(sketch, "E1234", {"start": v(24.68, 17.23) * mm, "end": v(24.16, 17.45) * mm});
            skLineSegment(sketch, "E1235", {"start": v(24.16, 17.45) * mm, "end": v(23.72, 17.75) * mm});
            skLineSegment(sketch, "E1236", {"start": v(23.72, 17.75) * mm, "end": v(23.28, 18.12) * mm});
            skLineSegment(sketch, "E1237", {"start": v(23.28, 18.12) * mm, "end": v(22.83, 18.48) * mm});
            skLineSegment(sketch, "E1238", {"start": v(22.83, 18.48) * mm, "end": v(22.46, 18.93) * mm});
            skLineSegment(sketch, "E1239", {"start": v(22.46, 18.93) * mm, "end": v(22.1, 19.37) * mm});
            skLineSegment(sketch, "E1240", {"start": v(22.1, 19.37) * mm, "end": v(21.8, 19.89) * mm});
            skLineSegment(sketch, "E1241", {"start": v(21.8, 19.89) * mm, "end": v(21.58, 20.4) * mm});
            skLineSegment(sketch, "E1242", {"start": v(21.58, 20.4) * mm, "end": v(21.36, 20.92) * mm});
            skLineSegment(sketch, "E1243", {"start": v(21.36, 20.92) * mm, "end": v(21.21, 21.43) * mm});
            skLineSegment(sketch, "E1244", {"start": v(137.75, 25.49) * mm, "end": v(137.68, 26) * mm});
            skLineSegment(sketch, "E1245", {"start": v(137.68, 26) * mm, "end": v(137.75, 26.6) * mm});
            skLineSegment(sketch, "E1246", {"start": v(137.75, 26.6) * mm, "end": v(137.82, 27.18) * mm});
            skLineSegment(sketch, "E1247", {"start": v(137.82, 27.18) * mm, "end": v(137.97, 27.7) * mm});
            skLineSegment(sketch, "E1248", {"start": v(137.97, 27.7) * mm, "end": v(138.12, 28.21) * mm});
            skLineSegment(sketch, "E1249", {"start": v(138.12, 28.21) * mm, "end": v(138.34, 28.73) * mm});
            skLineSegment(sketch, "E1250", {"start": v(138.34, 28.73) * mm, "end": v(138.64, 29.17) * mm});
            skLineSegment(sketch, "E1251", {"start": v(138.64, 29.17) * mm, "end": v(139, 29.69) * mm});
            skLineSegment(sketch, "E1252", {"start": v(139, 29.69) * mm, "end": v(139.37, 30.06) * mm});
            skLineSegment(sketch, "E1253", {"start": v(139.37, 30.06) * mm, "end": v(139.81, 30.5) * mm});
            skLineSegment(sketch, "E1254", {"start": v(139.81, 30.5) * mm, "end": v(140.26, 30.8) * mm});
            skLineSegment(sketch, "E1255", {"start": v(140.26, 30.8) * mm, "end": v(140.77, 31.09) * mm});
            skLineSegment(sketch, "E1256", {"start": v(140.77, 31.09) * mm, "end": v(141.29, 31.38) * mm});
            skLineSegment(sketch, "E1257", {"start": v(141.29, 31.38) * mm, "end": v(141.8, 31.53) * mm});
            skLineSegment(sketch, "E1258", {"start": v(141.8, 31.53) * mm, "end": v(142.32, 31.68) * mm});
            skLineSegment(sketch, "E1259", {"start": v(142.32, 31.68) * mm, "end": v(142.91, 31.75) * mm});
            skLineSegment(sketch, "E1260", {"start": v(142.91, 31.75) * mm, "end": v(143.43, 31.75) * mm});
            skLineSegment(sketch, "E1261", {"start": v(143.43, 31.75) * mm, "end": v(144.02, 31.75) * mm});
            skLineSegment(sketch, "E1262", {"start": v(144.02, 31.75) * mm, "end": v(144.6, 31.68) * mm});
            skLineSegment(sketch, "E1263", {"start": v(144.6, 31.68) * mm, "end": v(145.12, 31.53) * mm});
            skLineSegment(sketch, "E1264", {"start": v(145.12, 31.53) * mm, "end": v(145.64, 31.38) * mm});
            skLineSegment(sketch, "E1265", {"start": v(145.64, 31.38) * mm, "end": v(146.15, 31.16) * mm});
            skLineSegment(sketch, "E1266", {"start": v(146.15, 31.16) * mm, "end": v(146.67, 30.87) * mm});
            skLineSegment(sketch, "E1267", {"start": v(146.67, 30.87) * mm, "end": v(147.11, 30.5) * mm});
            skLineSegment(sketch, "E1268", {"start": v(147.11, 30.5) * mm, "end": v(147.55, 30.13) * mm});
            skLineSegment(sketch, "E1269", {"start": v(147.55, 30.13) * mm, "end": v(148.37, 29.4) * mm});
            skLineSegment(sketch, "E1270", {"start": v(148.37, 29.4) * mm, "end": v(149.18, 28.73) * mm});
            skLineSegment(sketch, "E1271", {"start": v(149.18, 28.73) * mm, "end": v(150.06, 28.21) * mm});
            skLineSegment(sketch, "E1272", {"start": v(150.06, 28.21) * mm, "end": v(150.94, 27.77) * mm});
            skLineSegment(sketch, "E1273", {"start": v(150.94, 27.77) * mm, "end": v(151.9, 27.4) * mm});
            skLineSegment(sketch, "E1274", {"start": v(151.9, 27.4) * mm, "end": v(152.86, 27.18) * mm});
            skLineSegment(sketch, "E1275", {"start": v(152.86, 27.18) * mm, "end": v(153.9, 27.04) * mm});
            skLineSegment(sketch, "E1276", {"start": v(153.9, 27.04) * mm, "end": v(154.85, 26.96) * mm});
            skLineSegment(sketch, "E1277", {"start": v(154.85, 26.96) * mm, "end": v(155.96, 27.04) * mm});
            skLineSegment(sketch, "E1278", {"start": v(155.96, 27.04) * mm, "end": v(156.92, 27.1) * mm});
            skLineSegment(sketch, "E1279", {"start": v(156.92, 27.1) * mm, "end": v(157.87, 27.4) * mm});
            skLineSegment(sketch, "E1280", {"start": v(157.87, 27.4) * mm, "end": v(158.76, 27.7) * mm});
            skLineSegment(sketch, "E1281", {"start": v(158.76, 27.7) * mm, "end": v(159.64, 28.14) * mm});
            skLineSegment(sketch, "E1282", {"start": v(159.64, 28.14) * mm, "end": v(160.53, 28.58) * mm});
            skLineSegment(sketch, "E1283", {"start": v(160.53, 28.58) * mm, "end": v(161.26, 29.25) * mm});
            skLineSegment(sketch, "E1284", {"start": v(161.26, 29.25) * mm, "end": v(162, 29.91) * mm});
            skLineSegment(sketch, "E1285", {"start": v(162, 29.91) * mm, "end": v(162.74, 30.65) * mm});
            skLineSegment(sketch, "E1286", {"start": v(162.74, 30.65) * mm, "end": v(163.33, 31.46) * mm});
            skLineSegment(sketch, "E1287", {"start": v(163.33, 31.46) * mm, "end": v(163.84, 32.27) * mm});
            skLineSegment(sketch, "E1288", {"start": v(163.84, 32.27) * mm, "end": v(164.21, 33.15) * mm});
            skLineSegment(sketch, "E1289", {"start": v(164.21, 33.15) * mm, "end": v(164.5, 34.04) * mm});
            skLineSegment(sketch, "E1290", {"start": v(164.5, 34.04) * mm, "end": v(164.8, 35) * mm});
            skLineSegment(sketch, "E1291", {"start": v(164.8, 35) * mm, "end": v(164.88, 35.95) * mm});
            skLineSegment(sketch, "E1292", {"start": v(164.88, 35.95) * mm, "end": v(164.95, 36.99) * mm});
            skLineSegment(sketch, "E1293", {"start": v(164.95, 36.99) * mm, "end": v(164.95, 52.83) * mm});
            skLineSegment(sketch, "E1294", {"start": v(164.95, 52.83) * mm, "end": v(164.95, 53.57) * mm});
            skLineSegment(sketch, "E1295", {"start": v(164.95, 53.57) * mm, "end": v(164.8, 54.3) * mm});
            skLineSegment(sketch, "E1296", {"start": v(164.8, 54.3) * mm, "end": v(164.66, 54.97) * mm});
            skLineSegment(sketch, "E1297", {"start": v(164.66, 54.97) * mm, "end": v(164.43, 55.64) * mm});
            skLineSegment(sketch, "E1298", {"start": v(164.43, 55.64) * mm, "end": v(164.14, 56.23) * mm});
            skLineSegment(sketch, "E1299", {"start": v(164.14, 56.23) * mm, "end": v(163.77, 56.82) * mm});
            skLineSegment(sketch, "E1300", {"start": v(163.77, 56.82) * mm, "end": v(163.4, 57.4) * mm});
            skLineSegment(sketch, "E1301", {"start": v(163.4, 57.4) * mm, "end": v(162.89, 57.92) * mm});
            skLineSegment(sketch, "E1302", {"start": v(162.89, 57.92) * mm, "end": v(162.37, 58.44) * mm});
            skLineSegment(sketch, "E1303", {"start": v(162.37, 58.44) * mm, "end": v(161.78, 58.88) * mm});
            skLineSegment(sketch, "E1304", {"start": v(161.78, 58.88) * mm, "end": v(161.2, 59.17) * mm});
            skLineSegment(sketch, "E1305", {"start": v(161.2, 59.17) * mm, "end": v(160.6, 59.47) * mm});
            skLineSegment(sketch, "E1306", {"start": v(160.6, 59.47) * mm, "end": v(159.94, 59.69) * mm});
            skLineSegment(sketch, "E1307", {"start": v(159.94, 59.69) * mm, "end": v(159.27, 59.91) * mm});
            skLineSegment(sketch, "E1308", {"start": v(159.27, 59.91) * mm, "end": v(158.54, 59.98) * mm});
            skLineSegment(sketch, "E1309", {"start": v(158.54, 59.98) * mm, "end": v(157.8, 59.98) * mm});
            skLineSegment(sketch, "E1310", {"start": v(157.8, 59.98) * mm, "end": v(157.73, 59.98) * mm});
            skLineSegment(sketch, "E1311", {"start": v(157.73, 59.98) * mm, "end": v(157.21, 60.06) * mm});
            skLineSegment(sketch, "E1312", {"start": v(157.21, 60.06) * mm, "end": v(156.62, 60.13) * mm});
            skLineSegment(sketch, "E1313", {"start": v(156.62, 60.13) * mm, "end": v(156.1, 60.28) * mm});
            skLineSegment(sketch, "E1314", {"start": v(156.1, 60.28) * mm, "end": v(155.59, 60.43) * mm});
            skLineSegment(sketch, "E1315", {"start": v(155.59, 60.43) * mm, "end": v(155.07, 60.72) * mm});
            skLineSegment(sketch, "E1316", {"start": v(155.07, 60.72) * mm, "end": v(154.56, 61.02) * mm});
            skLineSegment(sketch, "E1317", {"start": v(154.56, 61.02) * mm, "end": v(154.11, 61.31) * mm});
            skLineSegment(sketch, "E1318", {"start": v(154.11, 61.31) * mm, "end": v(153.67, 61.75) * mm});
            skLineSegment(sketch, "E1319", {"start": v(153.67, 61.75) * mm, "end": v(153.3, 62.2) * mm});
            skLineSegment(sketch, "E1320", {"start": v(153.3, 62.2) * mm, "end": v(152.94, 62.64) * mm});
            skLineSegment(sketch, "E1321", {"start": v(152.94, 62.64) * mm, "end": v(152.64, 63.15) * mm});
            skLineSegment(sketch, "E1322", {"start": v(152.64, 63.15) * mm, "end": v(152.42, 63.6) * mm});
            skLineSegment(sketch, "E1323", {"start": v(152.42, 63.6) * mm, "end": v(152.27, 64.11) * mm});
            skLineSegment(sketch, "E1324", {"start": v(152.27, 64.11) * mm, "end": v(152.12, 64.63) * mm});
            skLineSegment(sketch, "E1325", {"start": v(152.12, 64.63) * mm, "end": v(152.05, 65.22) * mm});
            skLineSegment(sketch, "E1326", {"start": v(152.05, 65.22) * mm, "end": v(151.98, 65.73) * mm});
            skLineSegment(sketch, "E1327", {"start": v(151.98, 65.73) * mm, "end": v(152.05, 66.32) * mm});
            skLineSegment(sketch, "E1328", {"start": v(152.05, 66.32) * mm, "end": v(152.12, 66.91) * mm});
            skLineSegment(sketch, "E1329", {"start": v(152.12, 66.91) * mm, "end": v(152.27, 67.43) * mm});
            skLineSegment(sketch, "E1330", {"start": v(152.27, 67.43) * mm, "end": v(152.42, 67.95) * mm});
            skLineSegment(sketch, "E1331", {"start": v(152.42, 67.95) * mm, "end": v(152.64, 68.46) * mm});
            skLineSegment(sketch, "E1332", {"start": v(152.64, 68.46) * mm, "end": v(152.94, 68.98) * mm});
            skLineSegment(sketch, "E1333", {"start": v(152.94, 68.98) * mm, "end": v(153.3, 69.42) * mm});
            skLineSegment(sketch, "E1334", {"start": v(153.3, 69.42) * mm, "end": v(153.67, 69.86) * mm});
            skLineSegment(sketch, "E1335", {"start": v(153.67, 69.86) * mm, "end": v(154.11, 70.23) * mm});
            skLineSegment(sketch, "E1336", {"start": v(154.11, 70.23) * mm, "end": v(154.56, 70.6) * mm});
            skLineSegment(sketch, "E1337", {"start": v(154.56, 70.6) * mm, "end": v(155.07, 70.9) * mm});
            skLineSegment(sketch, "E1338", {"start": v(155.07, 70.9) * mm, "end": v(155.59, 71.12) * mm});
            skLineSegment(sketch, "E1339", {"start": v(155.59, 71.12) * mm, "end": v(156.1, 71.26) * mm});
            skLineSegment(sketch, "E1340", {"start": v(156.1, 71.26) * mm, "end": v(156.62, 71.41) * mm});
            skLineSegment(sketch, "E1341", {"start": v(156.62, 71.41) * mm, "end": v(157.21, 71.48) * mm});
            skLineSegment(sketch, "E1342", {"start": v(157.21, 71.48) * mm, "end": v(157.73, 71.48) * mm});
            skLineSegment(sketch, "E1343", {"start": v(157.73, 71.48) * mm, "end": v(157.8, 71.48) * mm});
            skLineSegment(sketch, "E1344", {"start": v(157.8, 71.48) * mm, "end": v(158.54, 71.56) * mm});
            skLineSegment(sketch, "E1345", {"start": v(158.54, 71.56) * mm, "end": v(159.27, 71.63) * mm});
            skLineSegment(sketch, "E1346", {"start": v(159.27, 71.63) * mm, "end": v(159.94, 71.78) * mm});
            skLineSegment(sketch, "E1347", {"start": v(159.94, 71.78) * mm, "end": v(160.6, 72.07) * mm});
            skLineSegment(sketch, "E1348", {"start": v(160.6, 72.07) * mm, "end": v(161.2, 72.37) * mm});
            skLineSegment(sketch, "E1349", {"start": v(161.2, 72.37) * mm, "end": v(161.78, 72.66) * mm});
            skLineSegment(sketch, "E1350", {"start": v(161.78, 72.66) * mm, "end": v(162.37, 73.1) * mm});
            skLineSegment(sketch, "E1351", {"start": v(162.37, 73.1) * mm, "end": v(162.89, 73.62) * mm});
            skLineSegment(sketch, "E1352", {"start": v(162.89, 73.62) * mm, "end": v(163.4, 74.14) * mm});
            skLineSegment(sketch, "E1353", {"start": v(163.4, 74.14) * mm, "end": v(163.77, 74.73) * mm});
            skLineSegment(sketch, "E1354", {"start": v(163.77, 74.73) * mm, "end": v(164.14, 75.32) * mm});
            skLineSegment(sketch, "E1355", {"start": v(164.14, 75.32) * mm, "end": v(164.43, 75.9) * mm});
            skLineSegment(sketch, "E1356", {"start": v(164.43, 75.9) * mm, "end": v(164.66, 76.57) * mm});
            skLineSegment(sketch, "E1357", {"start": v(164.66, 76.57) * mm, "end": v(164.8, 77.23) * mm});
            skLineSegment(sketch, "E1358", {"start": v(164.8, 77.23) * mm, "end": v(164.95, 77.97) * mm});
            skLineSegment(sketch, "E1359", {"start": v(164.95, 77.97) * mm, "end": v(164.95, 78.7) * mm});
            skLineSegment(sketch, "E1360", {"start": v(164.95, 78.7) * mm, "end": v(164.95, 94.48) * mm});
            skLineSegment(sketch, "E1361", {"start": v(164.95, 94.48) * mm, "end": v(164.88, 95.51) * mm});
            skLineSegment(sketch, "E1362", {"start": v(164.88, 95.51) * mm, "end": v(164.8, 96.47) * mm});
            skLineSegment(sketch, "E1363", {"start": v(164.8, 96.47) * mm, "end": v(164.5, 97.43) * mm});
            skLineSegment(sketch, "E1364", {"start": v(164.5, 97.43) * mm, "end": v(164.21, 98.32) * mm});
            skLineSegment(sketch, "E1365", {"start": v(164.21, 98.32) * mm, "end": v(163.84, 99.2) * mm});
            skLineSegment(sketch, "E1366", {"start": v(163.84, 99.2) * mm, "end": v(163.33, 100.01) * mm});
            skLineSegment(sketch, "E1367", {"start": v(163.33, 100.01) * mm, "end": v(162.74, 100.82) * mm});
            skLineSegment(sketch, "E1368", {"start": v(162.74, 100.82) * mm, "end": v(162, 101.56) * mm});
            skLineSegment(sketch, "E1369", {"start": v(162, 101.56) * mm, "end": v(161.26, 102.22) * mm});
            skLineSegment(sketch, "E1370", {"start": v(161.26, 102.22) * mm, "end": v(160.53, 102.89) * mm});
            skLineSegment(sketch, "E1371", {"start": v(160.53, 102.89) * mm, "end": v(159.64, 103.33) * mm});
            skLineSegment(sketch, "E1372", {"start": v(159.64, 103.33) * mm, "end": v(158.76, 103.77) * mm});
            skLineSegment(sketch, "E1373", {"start": v(158.76, 103.77) * mm, "end": v(157.87, 104.06) * mm});
            skLineSegment(sketch, "E1374", {"start": v(157.87, 104.06) * mm, "end": v(156.92, 104.36) * mm});
            skLineSegment(sketch, "E1375", {"start": v(156.92, 104.36) * mm, "end": v(155.96, 104.43) * mm});
            skLineSegment(sketch, "E1376", {"start": v(155.96, 104.43) * mm, "end": v(154.85, 104.5) * mm});
            skLineSegment(sketch, "E1377", {"start": v(154.85, 104.5) * mm, "end": v(153.9, 104.43) * mm});
            skLineSegment(sketch, "E1378", {"start": v(153.9, 104.43) * mm, "end": v(152.86, 104.29) * mm});
            skLineSegment(sketch, "E1379", {"start": v(152.86, 104.29) * mm, "end": v(151.9, 104.06) * mm});
            skLineSegment(sketch, "E1380", {"start": v(151.9, 104.06) * mm, "end": v(151.02, 103.77) * mm});
            skLineSegment(sketch, "E1381", {"start": v(151.02, 103.77) * mm, "end": v(150.13, 103.33) * mm});
            skLineSegment(sketch, "E1382", {"start": v(150.13, 103.33) * mm, "end": v(149.25, 102.74) * mm});
            skLineSegment(sketch, "E1383", {"start": v(149.25, 102.74) * mm, "end": v(148.37, 102.15) * mm});
            skLineSegment(sketch, "E1384", {"start": v(148.37, 102.15) * mm, "end": v(147.55, 101.41) * mm});
            skLineSegment(sketch, "E1385", {"start": v(147.11, 101.04) * mm, "end": v(146.67, 100.67) * mm});
            skLineSegment(sketch, "E1386", {"start": v(146.67, 100.67) * mm, "end": v(146.15, 100.38) * mm});
            skLineSegment(sketch, "E1387", {"start": v(146.15, 100.38) * mm, "end": v(145.64, 100.16) * mm});
            skLineSegment(sketch, "E1388", {"start": v(145.64, 100.16) * mm, "end": v(145.12, 99.94) * mm});
            skLineSegment(sketch, "E1389", {"start": v(145.12, 99.94) * mm, "end": v(144.6, 99.79) * mm});
            skLineSegment(sketch, "E1390", {"start": v(144.6, 99.79) * mm, "end": v(144.02, 99.72) * mm});
            skLineSegment(sketch, "E1391", {"start": v(144.02, 99.72) * mm, "end": v(143.43, 99.72) * mm});
            skLineSegment(sketch, "E1392", {"start": v(143.43, 99.72) * mm, "end": v(142.91, 99.72) * mm});
            skLineSegment(sketch, "E1393", {"start": v(142.91, 99.72) * mm, "end": v(142.32, 99.79) * mm});
            skLineSegment(sketch, "E1394", {"start": v(142.32, 99.79) * mm, "end": v(141.8, 99.94) * mm});
            skLineSegment(sketch, "E1395", {"start": v(141.8, 99.94) * mm, "end": v(141.29, 100.08) * mm});
            skLineSegment(sketch, "E1396", {"start": v(141.29, 100.08) * mm, "end": v(140.77, 100.38) * mm});
            skLineSegment(sketch, "E1397", {"start": v(140.77, 100.38) * mm, "end": v(140.26, 100.67) * mm});
            skLineSegment(sketch, "E1398", {"start": v(140.26, 100.67) * mm, "end": v(139.81, 100.97) * mm});
            skLineSegment(sketch, "E1399", {"start": v(139.81, 100.97) * mm, "end": v(139.37, 101.41) * mm});
            skLineSegment(sketch, "E1400", {"start": v(139.37, 101.41) * mm, "end": v(139, 101.78) * mm});
            skLineSegment(sketch, "E1401", {"start": v(139, 101.78) * mm, "end": v(138.64, 102.3) * mm});
            skLineSegment(sketch, "E1402", {"start": v(138.64, 102.3) * mm, "end": v(138.34, 102.74) * mm});
            skLineSegment(sketch, "E1403", {"start": v(138.34, 102.74) * mm, "end": v(138.12, 103.25) * mm});
            skLineSegment(sketch, "E1404", {"start": v(138.12, 103.25) * mm, "end": v(137.97, 103.77) * mm});
            skLineSegment(sketch, "E1405", {"start": v(137.97, 103.77) * mm, "end": v(137.82, 104.29) * mm});
            skLineSegment(sketch, "E1406", {"start": v(137.82, 104.29) * mm, "end": v(137.75, 104.88) * mm});
            skLineSegment(sketch, "E1407", {"start": v(137.75, 104.88) * mm, "end": v(137.68, 105.47) * mm});
            skLineSegment(sketch, "E1408", {"start": v(137.68, 105.47) * mm, "end": v(137.75, 105.98) * mm});
            skLineSegment(sketch, "E1409", {"start": v(137.75, 105.98) * mm, "end": v(137.82, 106.57) * mm});
            skLineSegment(sketch, "E1410", {"start": v(137.82, 106.57) * mm, "end": v(137.97, 107.09) * mm});
            skLineSegment(sketch, "E1411", {"start": v(137.97, 107.09) * mm, "end": v(138.12, 107.6) * mm});
            skLineSegment(sketch, "E1412", {"start": v(138.12, 107.6) * mm, "end": v(138.41, 108.12) * mm});
            skLineSegment(sketch, "E1413", {"start": v(138.41, 108.12) * mm, "end": v(138.7, 108.56) * mm});
            skLineSegment(sketch, "E1414", {"start": v(138.7, 108.56) * mm, "end": v(139, 109) * mm});
            skLineSegment(sketch, "E1415", {"start": v(139, 109) * mm, "end": v(139.45, 109.45) * mm});
            skLineSegment(sketch, "E1416", {"start": v(139.45, 109.45) * mm, "end": v(141.14, 111) * mm});
            skLineSegment(sketch, "E1417", {"start": v(141.14, 111) * mm, "end": v(142.84, 112.4) * mm});
            skLineSegment(sketch, "E1418", {"start": v(142.84, 112.4) * mm, "end": v(144.68, 113.5) * mm});
            skLineSegment(sketch, "E1419", {"start": v(144.68, 113.5) * mm, "end": v(146.6, 114.46) * mm});
            skLineSegment(sketch, "E1420", {"start": v(146.6, 114.46) * mm, "end": v(148.51, 115.12) * mm});
            skLineSegment(sketch, "E1421", {"start": v(148.51, 115.12) * mm, "end": v(150.58, 115.64) * mm});
            skLineSegment(sketch, "E1422", {"start": v(150.58, 115.64) * mm, "end": v(152.71, 116) * mm});
            skLineSegment(sketch, "E1423", {"start": v(152.71, 116) * mm, "end": v(154.85, 116.08) * mm});
            skLineSegment(sketch, "E1424", {"start": v(154.85, 116.08) * mm, "end": v(157.06, 116) * mm});
            skLineSegment(sketch, "E1425", {"start": v(157.06, 116) * mm, "end": v(159.2, 115.71) * mm});
            skLineSegment(sketch, "E1426", {"start": v(159.2, 115.71) * mm, "end": v(161.2, 115.2) * mm});
            skLineSegment(sketch, "E1427", {"start": v(161.2, 115.2) * mm, "end": v(163.18, 114.53) * mm});
            skLineSegment(sketch, "E1428", {"start": v(163.18, 114.53) * mm, "end": v(165.02, 113.57) * mm});
            skLineSegment(sketch, "E1429", {"start": v(165.02, 113.57) * mm, "end": v(166.8, 112.54) * mm});
            skLineSegment(sketch, "E1430", {"start": v(166.8, 112.54) * mm, "end": v(168.49, 111.21) * mm});
            skLineSegment(sketch, "E1431", {"start": v(168.49, 111.21) * mm, "end": v(170.11, 109.74) * mm});
            skLineSegment(sketch, "E1432", {"start": v(170.11, 109.74) * mm, "end": v(171.58, 108.12) * mm});
            skLineSegment(sketch, "E1433", {"start": v(171.58, 108.12) * mm, "end": v(172.91, 106.42) * mm});
            skLineSegment(sketch, "E1434", {"start": v(172.91, 106.42) * mm, "end": v(173.94, 104.65) * mm});
            skLineSegment(sketch, "E1435", {"start": v(173.94, 104.65) * mm, "end": v(174.9, 102.81) * mm});
            skLineSegment(sketch, "E1436", {"start": v(174.9, 102.81) * mm, "end": v(175.56, 100.82) * mm});
            skLineSegment(sketch, "E1437", {"start": v(175.56, 100.82) * mm, "end": v(176.08, 98.83) * mm});
            skLineSegment(sketch, "E1438", {"start": v(176.08, 98.83) * mm, "end": v(176.38, 96.7) * mm});
            skLineSegment(sketch, "E1439", {"start": v(176.38, 96.7) * mm, "end": v(176.45, 94.48) * mm});
            skLineSegment(sketch, "E1440", {"start": v(176.45, 94.48) * mm, "end": v(176.45, 78.7) * mm});
            skLineSegment(sketch, "E1441", {"start": v(176.45, 78.7) * mm, "end": v(176.38, 76.8) * mm});
            skLineSegment(sketch, "E1442", {"start": v(176.38, 76.8) * mm, "end": v(176.15, 75.02) * mm});
            skLineSegment(sketch, "E1443", {"start": v(176.15, 75.02) * mm, "end": v(175.71, 73.25) * mm});
            skLineSegment(sketch, "E1444", {"start": v(175.71, 73.25) * mm, "end": v(175.12, 71.63) * mm});
            skLineSegment(sketch, "E1445", {"start": v(175.12, 71.63) * mm, "end": v(174.39, 70.08) * mm});
            skLineSegment(sketch, "E1446", {"start": v(174.39, 70.08) * mm, "end": v(173.5, 68.54) * mm});
            skLineSegment(sketch, "E1447", {"start": v(173.5, 68.54) * mm, "end": v(172.4, 67.13) * mm});
            skLineSegment(sketch, "E1448", {"start": v(172.4, 67.13) * mm, "end": v(171.22, 65.73) * mm});
            skLineSegment(sketch, "E1449", {"start": v(171.22, 65.73) * mm, "end": v(172.4, 64.4) * mm});
            skLineSegment(sketch, "E1450", {"start": v(172.4, 64.4) * mm, "end": v(173.5, 63) * mm});
            skLineSegment(sketch, "E1451", {"start": v(173.5, 63) * mm, "end": v(174.39, 61.46) * mm});
            skLineSegment(sketch, "E1452", {"start": v(174.39, 61.46) * mm, "end": v(175.12, 59.91) * mm});
            skLineSegment(sketch, "E1453", {"start": v(175.12, 59.91) * mm, "end": v(175.71, 58.29) * mm});
            skLineSegment(sketch, "E1454", {"start": v(175.71, 58.29) * mm, "end": v(176.15, 56.52) * mm});
            skLineSegment(sketch, "E1455", {"start": v(176.15, 56.52) * mm, "end": v(176.38, 54.75) * mm});
            skLineSegment(sketch, "E1456", {"start": v(176.38, 54.75) * mm, "end": v(176.45, 52.83) * mm});
            skLineSegment(sketch, "E1457", {"start": v(176.45, 52.83) * mm, "end": v(176.45, 36.99) * mm});
            skLineSegment(sketch, "E1458", {"start": v(176.45, 36.99) * mm, "end": v(176.38, 34.78) * mm});
            skLineSegment(sketch, "E1459", {"start": v(176.38, 34.78) * mm, "end": v(176.08, 32.64) * mm});
            skLineSegment(sketch, "E1460", {"start": v(176.08, 32.64) * mm, "end": v(175.56, 30.65) * mm});
            skLineSegment(sketch, "E1461", {"start": v(175.56, 30.65) * mm, "end": v(174.9, 28.66) * mm});
            skLineSegment(sketch, "E1462", {"start": v(174.9, 28.66) * mm, "end": v(173.94, 26.81) * mm});
            skLineSegment(sketch, "E1463", {"start": v(173.94, 26.81) * mm, "end": v(172.91, 25.05) * mm});
            skLineSegment(sketch, "E1464", {"start": v(172.91, 25.05) * mm, "end": v(171.58, 23.35) * mm});
            skLineSegment(sketch, "E1465", {"start": v(171.58, 23.35) * mm, "end": v(170.11, 21.73) * mm});
            skLineSegment(sketch, "E1466", {"start": v(170.11, 21.73) * mm, "end": v(168.49, 20.25) * mm});
            skLineSegment(sketch, "E1467", {"start": v(168.49, 20.25) * mm, "end": v(166.8, 18.93) * mm});
            skLineSegment(sketch, "E1468", {"start": v(166.8, 18.93) * mm, "end": v(165.02, 17.9) * mm});
            skLineSegment(sketch, "E1469", {"start": v(165.02, 17.9) * mm, "end": v(163.18, 16.94) * mm});
            skLineSegment(sketch, "E1470", {"start": v(163.18, 16.94) * mm, "end": v(161.2, 16.27) * mm});
            skLineSegment(sketch, "E1471", {"start": v(161.2, 16.27) * mm, "end": v(159.2, 15.76) * mm});
            skLineSegment(sketch, "E1472", {"start": v(159.2, 15.76) * mm, "end": v(157.06, 15.46) * mm});
            skLineSegment(sketch, "E1473", {"start": v(157.06, 15.46) * mm, "end": v(154.85, 15.39) * mm});
            skLineSegment(sketch, "E1474", {"start": v(154.85, 15.39) * mm, "end": v(152.71, 15.46) * mm});
            skLineSegment(sketch, "E1475", {"start": v(152.71, 15.46) * mm, "end": v(150.58, 15.83) * mm});
            skLineSegment(sketch, "E1476", {"start": v(150.58, 15.83) * mm, "end": v(148.51, 16.35) * mm});
            skLineSegment(sketch, "E1477", {"start": v(148.51, 16.35) * mm, "end": v(146.6, 17.01) * mm});
            skLineSegment(sketch, "E1478", {"start": v(146.6, 17.01) * mm, "end": v(144.68, 17.97) * mm});
            skLineSegment(sketch, "E1479", {"start": v(144.68, 17.97) * mm, "end": v(142.84, 19.07) * mm});
            skLineSegment(sketch, "E1480", {"start": v(142.84, 19.07) * mm, "end": v(141.14, 20.47) * mm});
            skLineSegment(sketch, "E1481", {"start": v(141.14, 20.47) * mm, "end": v(139.45, 22.02) * mm});
            skLineSegment(sketch, "E1482", {"start": v(139.45, 22.02) * mm, "end": v(139, 22.47) * mm});
            skLineSegment(sketch, "E1483", {"start": v(139, 22.47) * mm, "end": v(138.7, 22.9) * mm});
            skLineSegment(sketch, "E1484", {"start": v(138.7, 22.9) * mm, "end": v(138.41, 23.35) * mm});
            skLineSegment(sketch, "E1485", {"start": v(138.41, 23.35) * mm, "end": v(138.12, 23.87) * mm});
            skLineSegment(sketch, "E1486", {"start": v(138.12, 23.87) * mm, "end": v(137.97, 24.38) * mm});
            skLineSegment(sketch, "E1487", {"start": v(137.97, 24.38) * mm, "end": v(137.82, 24.9) * mm});
            skLineSegment(sketch, "E1488", {"start": v(137.82, 24.9) * mm, "end": v(137.75, 25.49) * mm});
            skLineSegment(sketch, "E1489", {"start": v(192.3, 34.78) * mm, "end": v(192.15, 36.99) * mm});
            skLineSegment(sketch, "E1490", {"start": v(192.15, 36.99) * mm, "end": v(192.15, 57.04) * mm});
            skLineSegment(sketch, "E1491", {"start": v(192.15, 57.04) * mm, "end": v(192.22, 57.55) * mm});
            skLineSegment(sketch, "E1492", {"start": v(192.22, 57.55) * mm, "end": v(192.3, 58.14) * mm});
            skLineSegment(sketch, "E1493", {"start": v(192.3, 58.14) * mm, "end": v(192.44, 58.66) * mm});
            skLineSegment(sketch, "E1494", {"start": v(192.44, 58.66) * mm, "end": v(192.6, 59.17) * mm});
            skLineSegment(sketch, "E1495", {"start": v(192.6, 59.17) * mm, "end": v(192.81, 59.69) * mm});
            skLineSegment(sketch, "E1496", {"start": v(192.81, 59.69) * mm, "end": v(193.1, 60.2) * mm});
            skLineSegment(sketch, "E1497", {"start": v(193.1, 60.2) * mm, "end": v(193.48, 60.65) * mm});
            skLineSegment(sketch, "E1498", {"start": v(193.48, 60.65) * mm, "end": v(193.85, 61.1) * mm});
            skLineSegment(sketch, "E1499", {"start": v(193.85, 61.1) * mm, "end": v(194.29, 61.46) * mm});
            skLineSegment(sketch, "E1500", {"start": v(194.29, 61.46) * mm, "end": v(194.73, 61.83) * mm});
            skLineSegment(sketch, "E1501", {"start": v(194.73, 61.83) * mm, "end": v(195.25, 62.12) * mm});
            skLineSegment(sketch, "E1502", {"start": v(195.25, 62.12) * mm, "end": v(195.76, 62.34) * mm});
            skLineSegment(sketch, "E1503", {"start": v(195.76, 62.34) * mm, "end": v(196.28, 62.5) * mm});
            skLineSegment(sketch, "E1504", {"start": v(196.28, 62.5) * mm, "end": v(196.8, 62.64) * mm});
            skLineSegment(sketch, "E1505", {"start": v(196.8, 62.64) * mm, "end": v(197.38, 62.71) * mm});
            skLineSegment(sketch, "E1506", {"start": v(197.38, 62.71) * mm, "end": v(197.9, 62.79) * mm});
            skLineSegment(sketch, "E1507", {"start": v(197.9, 62.79) * mm, "end": v(198.49, 62.71) * mm});
            skLineSegment(sketch, "E1508", {"start": v(198.49, 62.71) * mm, "end": v(199.08, 62.64) * mm});
            skLineSegment(sketch, "E1509", {"start": v(199.08, 62.64) * mm, "end": v(199.6, 62.5) * mm});
            skLineSegment(sketch, "E1510", {"start": v(199.6, 62.5) * mm, "end": v(200.11, 62.34) * mm});
            skLineSegment(sketch, "E1511", {"start": v(200.11, 62.34) * mm, "end": v(200.63, 62.12) * mm});
            skLineSegment(sketch, "E1512", {"start": v(200.63, 62.12) * mm, "end": v(201.14, 61.83) * mm});
            skLineSegment(sketch, "E1513", {"start": v(201.14, 61.83) * mm, "end": v(201.59, 61.46) * mm});
            skLineSegment(sketch, "E1514", {"start": v(201.59, 61.46) * mm, "end": v(202.03, 61.1) * mm});
            skLineSegment(sketch, "E1515", {"start": v(202.03, 61.1) * mm, "end": v(202.4, 60.65) * mm});
            skLineSegment(sketch, "E1516", {"start": v(202.4, 60.65) * mm, "end": v(202.76, 60.2) * mm});
            skLineSegment(sketch, "E1517", {"start": v(202.76, 60.2) * mm, "end": v(203.06, 59.69) * mm});
            skLineSegment(sketch, "E1518", {"start": v(203.06, 59.69) * mm, "end": v(203.28, 59.17) * mm});
            skLineSegment(sketch, "E1519", {"start": v(203.28, 59.17) * mm, "end": v(203.43, 58.66) * mm});
            skLineSegment(sketch, "E1520", {"start": v(203.43, 58.66) * mm, "end": v(203.58, 58.14) * mm});
            skLineSegment(sketch, "E1521", {"start": v(203.58, 58.14) * mm, "end": v(203.65, 57.55) * mm});
            skLineSegment(sketch, "E1522", {"start": v(203.65, 57.55) * mm, "end": v(203.65, 57.04) * mm});
            skLineSegment(sketch, "E1523", {"start": v(203.65, 57.04) * mm, "end": v(203.65, 36.99) * mm});
            skLineSegment(sketch, "E1524", {"start": v(203.65, 36.99) * mm, "end": v(203.72, 35.95) * mm});
            skLineSegment(sketch, "E1525", {"start": v(203.72, 35.95) * mm, "end": v(203.87, 34.92) * mm});
            skLineSegment(sketch, "E1526", {"start": v(203.87, 34.92) * mm, "end": v(204.1, 33.96) * mm});
            skLineSegment(sketch, "E1527", {"start": v(204.1, 33.96) * mm, "end": v(204.39, 33.08) * mm});
            skLineSegment(sketch, "E1528", {"start": v(204.39, 33.08) * mm, "end": v(204.83, 32.2) * mm});
            skLineSegment(sketch, "E1529", {"start": v(204.83, 32.2) * mm, "end": v(205.34, 31.38) * mm});
            skLineSegment(sketch, "E1530", {"start": v(205.34, 31.38) * mm, "end": v(205.93, 30.57) * mm});
            skLineSegment(sketch, "E1531", {"start": v(205.93, 30.57) * mm, "end": v(206.6, 29.84) * mm});
            skLineSegment(sketch, "E1532", {"start": v(206.6, 29.84) * mm, "end": v(207.4, 29.17) * mm});
            skLineSegment(sketch, "E1533", {"start": v(207.4, 29.17) * mm, "end": v(208.22, 28.5) * mm});
            skLineSegment(sketch, "E1534", {"start": v(208.22, 28.5) * mm, "end": v(209.03, 28.07) * mm});
            skLineSegment(sketch, "E1535", {"start": v(209.03, 28.07) * mm, "end": v(209.91, 27.63) * mm});
            skLineSegment(sketch, "E1536", {"start": v(209.91, 27.63) * mm, "end": v(210.8, 27.33) * mm});
            skLineSegment(sketch, "E1537", {"start": v(210.8, 27.33) * mm, "end": v(211.76, 27.04) * mm});
            skLineSegment(sketch, "E1538", {"start": v(211.76, 27.04) * mm, "end": v(212.72, 26.96) * mm});
            skLineSegment(sketch, "E1539", {"start": v(212.72, 26.96) * mm, "end": v(213.75, 26.89) * mm});
            skLineSegment(sketch, "E1540", {"start": v(213.75, 26.89) * mm, "end": v(214.78, 26.96) * mm});
            skLineSegment(sketch, "E1541", {"start": v(214.78, 26.96) * mm, "end": v(215.74, 27.04) * mm});
            skLineSegment(sketch, "E1542", {"start": v(215.74, 27.04) * mm, "end": v(216.7, 27.33) * mm});
            skLineSegment(sketch, "E1543", {"start": v(216.7, 27.33) * mm, "end": v(217.58, 27.63) * mm});
            skLineSegment(sketch, "E1544", {"start": v(217.58, 27.63) * mm, "end": v(218.47, 28.07) * mm});
            skLineSegment(sketch, "E1545", {"start": v(218.47, 28.07) * mm, "end": v(219.28, 28.5) * mm});
            skLineSegment(sketch, "E1546", {"start": v(219.28, 28.5) * mm, "end": v(220.09, 29.17) * mm});
            skLineSegment(sketch, "E1547", {"start": v(220.09, 29.17) * mm, "end": v(220.9, 29.84) * mm});
            skLineSegment(sketch, "E1548", {"start": v(220.9, 29.84) * mm, "end": v(221.56, 30.57) * mm});
            skLineSegment(sketch, "E1549", {"start": v(221.56, 30.57) * mm, "end": v(222.15, 31.38) * mm});
            skLineSegment(sketch, "E1550", {"start": v(222.15, 31.38) * mm, "end": v(222.67, 32.2) * mm});
            skLineSegment(sketch, "E1551", {"start": v(222.67, 32.2) * mm, "end": v(223.1, 33.08) * mm});
            skLineSegment(sketch, "E1552", {"start": v(223.1, 33.08) * mm, "end": v(223.4, 33.96) * mm});
            skLineSegment(sketch, "E1553", {"start": v(223.4, 33.96) * mm, "end": v(223.63, 34.92) * mm});
            skLineSegment(sketch, "E1554", {"start": v(223.63, 34.92) * mm, "end": v(223.77, 35.95) * mm});
            skLineSegment(sketch, "E1555", {"start": v(223.77, 35.95) * mm, "end": v(223.85, 36.99) * mm});
            skLineSegment(sketch, "E1556", {"start": v(223.85, 36.99) * mm, "end": v(223.85, 57.04) * mm});
            skLineSegment(sketch, "E1557", {"start": v(223.85, 57.04) * mm, "end": v(223.85, 57.55) * mm});
            skLineSegment(sketch, "E1558", {"start": v(223.85, 57.55) * mm, "end": v(223.92, 58.14) * mm});
            skLineSegment(sketch, "E1559", {"start": v(223.92, 58.14) * mm, "end": v(224.07, 58.66) * mm});
            skLineSegment(sketch, "E1560", {"start": v(224.07, 58.66) * mm, "end": v(224.21, 59.17) * mm});
            skLineSegment(sketch, "E1561", {"start": v(224.21, 59.17) * mm, "end": v(224.44, 59.69) * mm});
            skLineSegment(sketch, "E1562", {"start": v(224.44, 59.69) * mm, "end": v(224.73, 60.2) * mm});
            skLineSegment(sketch, "E1563", {"start": v(224.73, 60.2) * mm, "end": v(225.1, 60.65) * mm});
            skLineSegment(sketch, "E1564", {"start": v(225.1, 60.65) * mm, "end": v(225.47, 61.1) * mm});
            skLineSegment(sketch, "E1565", {"start": v(225.47, 61.1) * mm, "end": v(225.91, 61.46) * mm});
            skLineSegment(sketch, "E1566", {"start": v(225.91, 61.46) * mm, "end": v(226.35, 61.83) * mm});
            skLineSegment(sketch, "E1567", {"start": v(226.35, 61.83) * mm, "end": v(226.87, 62.12) * mm});
            skLineSegment(sketch, "E1568", {"start": v(226.87, 62.12) * mm, "end": v(227.38, 62.34) * mm});
            skLineSegment(sketch, "E1569", {"start": v(227.38, 62.34) * mm, "end": v(227.9, 62.5) * mm});
            skLineSegment(sketch, "E1570", {"start": v(227.9, 62.5) * mm, "end": v(228.42, 62.64) * mm});
            skLineSegment(sketch, "E1571", {"start": v(228.42, 62.64) * mm, "end": v(229, 62.71) * mm});
            skLineSegment(sketch, "E1572", {"start": v(229, 62.71) * mm, "end": v(229.6, 62.79) * mm});
            skLineSegment(sketch, "E1573", {"start": v(229.6, 62.79) * mm, "end": v(230.11, 62.71) * mm});
            skLineSegment(sketch, "E1574", {"start": v(230.11, 62.71) * mm, "end": v(230.7, 62.64) * mm});
            skLineSegment(sketch, "E1575", {"start": v(230.7, 62.64) * mm, "end": v(231.22, 62.5) * mm});
            skLineSegment(sketch, "E1576", {"start": v(231.22, 62.5) * mm, "end": v(231.73, 62.34) * mm});
            skLineSegment(sketch, "E1577", {"start": v(231.73, 62.34) * mm, "end": v(232.25, 62.12) * mm});
            skLineSegment(sketch, "E1578", {"start": v(232.25, 62.12) * mm, "end": v(232.77, 61.83) * mm});
            skLineSegment(sketch, "E1579", {"start": v(232.77, 61.83) * mm, "end": v(233.2, 61.46) * mm});
            skLineSegment(sketch, "E1580", {"start": v(233.2, 61.46) * mm, "end": v(233.65, 61.1) * mm});
            skLineSegment(sketch, "E1581", {"start": v(233.65, 61.1) * mm, "end": v(234.02, 60.65) * mm});
            skLineSegment(sketch, "E1582", {"start": v(234.02, 60.65) * mm, "end": v(234.39, 60.2) * mm});
            skLineSegment(sketch, "E1583", {"start": v(234.39, 60.2) * mm, "end": v(234.68, 59.69) * mm});
            skLineSegment(sketch, "E1584", {"start": v(234.68, 59.69) * mm, "end": v(234.9, 59.17) * mm});
            skLineSegment(sketch, "E1585", {"start": v(234.9, 59.17) * mm, "end": v(235.05, 58.66) * mm});
            skLineSegment(sketch, "E1586", {"start": v(235.05, 58.66) * mm, "end": v(235.2, 58.14) * mm});
            skLineSegment(sketch, "E1587", {"start": v(235.2, 58.14) * mm, "end": v(235.27, 57.55) * mm});
            skLineSegment(sketch, "E1588", {"start": v(235.27, 57.55) * mm, "end": v(235.35, 57.04) * mm});
            skLineSegment(sketch, "E1589", {"start": v(235.35, 57.04) * mm, "end": v(235.35, 36.99) * mm});
            skLineSegment(sketch, "E1590", {"start": v(235.35, 36.99) * mm, "end": v(235.2, 34.78) * mm});
            skLineSegment(sketch, "E1591", {"start": v(235.2, 34.78) * mm, "end": v(234.9, 32.64) * mm});
            skLineSegment(sketch, "E1592", {"start": v(234.9, 32.64) * mm, "end": v(234.39, 30.65) * mm});
            skLineSegment(sketch, "E1593", {"start": v(234.39, 30.65) * mm, "end": v(233.72, 28.66) * mm});
            skLineSegment(sketch, "E1594", {"start": v(233.72, 28.66) * mm, "end": v(232.84, 26.81) * mm});
            skLineSegment(sketch, "E1595", {"start": v(232.84, 26.81) * mm, "end": v(231.73, 25.05) * mm});
            skLineSegment(sketch, "E1596", {"start": v(231.73, 25.05) * mm, "end": v(230.48, 23.35) * mm});
            skLineSegment(sketch, "E1597", {"start": v(230.48, 23.35) * mm, "end": v(229, 21.73) * mm});
            skLineSegment(sketch, "E1598", {"start": v(229, 21.73) * mm, "end": v(227.38, 20.25) * mm});
            skLineSegment(sketch, "E1599", {"start": v(227.38, 20.25) * mm, "end": v(225.69, 18.93) * mm});
            skLineSegment(sketch, "E1600", {"start": v(225.69, 18.93) * mm, "end": v(223.85, 17.9) * mm});
            skLineSegment(sketch, "E1601", {"start": v(223.85, 17.9) * mm, "end": v(222, 16.94) * mm});
            skLineSegment(sketch, "E1602", {"start": v(222, 16.94) * mm, "end": v(220.09, 16.27) * mm});
            skLineSegment(sketch, "E1603", {"start": v(220.09, 16.27) * mm, "end": v(218.02, 15.76) * mm});
            skLineSegment(sketch, "E1604", {"start": v(218.02, 15.76) * mm, "end": v(215.96, 15.46) * mm});
            skLineSegment(sketch, "E1605", {"start": v(215.96, 15.46) * mm, "end": v(213.75, 15.39) * mm});
            skLineSegment(sketch, "E1606", {"start": v(213.75, 15.39) * mm, "end": v(211.54, 15.46) * mm});
            skLineSegment(sketch, "E1607", {"start": v(211.54, 15.46) * mm, "end": v(209.47, 15.76) * mm});
            skLineSegment(sketch, "E1608", {"start": v(209.47, 15.76) * mm, "end": v(207.4, 16.27) * mm});
            skLineSegment(sketch, "E1609", {"start": v(207.4, 16.27) * mm, "end": v(205.5, 16.94) * mm});
            skLineSegment(sketch, "E1610", {"start": v(205.5, 16.94) * mm, "end": v(203.65, 17.9) * mm});
            skLineSegment(sketch, "E1611", {"start": v(203.65, 17.9) * mm, "end": v(201.8, 18.93) * mm});
            skLineSegment(sketch, "E1612", {"start": v(201.8, 18.93) * mm, "end": v(200.11, 20.25) * mm});
            skLineSegment(sketch, "E1613", {"start": v(200.11, 20.25) * mm, "end": v(198.49, 21.73) * mm});
            skLineSegment(sketch, "E1614", {"start": v(198.49, 21.73) * mm, "end": v(197.02, 23.35) * mm});
            skLineSegment(sketch, "E1615", {"start": v(197.02, 23.35) * mm, "end": v(195.76, 25.05) * mm});
            skLineSegment(sketch, "E1616", {"start": v(195.76, 25.05) * mm, "end": v(194.66, 26.81) * mm});
            skLineSegment(sketch, "E1617", {"start": v(194.66, 26.81) * mm, "end": v(193.77, 28.66) * mm});
            skLineSegment(sketch, "E1618", {"start": v(193.77, 28.66) * mm, "end": v(193.1, 30.65) * mm});
            skLineSegment(sketch, "E1619", {"start": v(193.1, 30.65) * mm, "end": v(192.6, 32.64) * mm});
            skLineSegment(sketch, "E1620", {"start": v(192.6, 32.64) * mm, "end": v(192.3, 34.78) * mm});
            skLineSegment(sketch, "E1621", {"start": v(192.3, 96.7) * mm, "end": v(192.6, 98.83) * mm});
            skLineSegment(sketch, "E1622", {"start": v(192.6, 98.83) * mm, "end": v(193.1, 100.82) * mm});
            skLineSegment(sketch, "E1623", {"start": v(193.1, 100.82) * mm, "end": v(193.77, 102.81) * mm});
            skLineSegment(sketch, "E1624", {"start": v(193.77, 102.81) * mm, "end": v(194.66, 104.65) * mm});
            skLineSegment(sketch, "E1625", {"start": v(194.66, 104.65) * mm, "end": v(195.76, 106.42) * mm});
            skLineSegment(sketch, "E1626", {"start": v(195.76, 106.42) * mm, "end": v(197.02, 108.12) * mm});
            skLineSegment(sketch, "E1627", {"start": v(197.02, 108.12) * mm, "end": v(198.49, 109.74) * mm});
            skLineSegment(sketch, "E1628", {"start": v(198.49, 109.74) * mm, "end": v(200.11, 111.21) * mm});
            skLineSegment(sketch, "E1629", {"start": v(200.11, 111.21) * mm, "end": v(201.8, 112.54) * mm});
            skLineSegment(sketch, "E1630", {"start": v(201.8, 112.54) * mm, "end": v(203.65, 113.57) * mm});
            skLineSegment(sketch, "E1631", {"start": v(203.65, 113.57) * mm, "end": v(205.5, 114.53) * mm});
            skLineSegment(sketch, "E1632", {"start": v(205.5, 114.53) * mm, "end": v(207.4, 115.2) * mm});
            skLineSegment(sketch, "E1633", {"start": v(207.4, 115.2) * mm, "end": v(209.47, 115.71) * mm});
            skLineSegment(sketch, "E1634", {"start": v(209.47, 115.71) * mm, "end": v(211.54, 116) * mm});
            skLineSegment(sketch, "E1635", {"start": v(211.54, 116) * mm, "end": v(213.75, 116.08) * mm});
            skLineSegment(sketch, "E1636", {"start": v(213.75, 116.08) * mm, "end": v(215.96, 116) * mm});
            skLineSegment(sketch, "E1637", {"start": v(215.96, 116) * mm, "end": v(218.02, 115.71) * mm});
            skLineSegment(sketch, "E1638", {"start": v(218.02, 115.71) * mm, "end": v(220.09, 115.2) * mm});
            skLineSegment(sketch, "E1639", {"start": v(220.09, 115.2) * mm, "end": v(222, 114.53) * mm});
            skLineSegment(sketch, "E1640", {"start": v(222, 114.53) * mm, "end": v(223.85, 113.57) * mm});
            skLineSegment(sketch, "E1641", {"start": v(223.85, 113.57) * mm, "end": v(225.69, 112.54) * mm});
            skLineSegment(sketch, "E1642", {"start": v(225.69, 112.54) * mm, "end": v(227.38, 111.21) * mm});
            skLineSegment(sketch, "E1643", {"start": v(227.38, 111.21) * mm, "end": v(229, 109.74) * mm});
            skLineSegment(sketch, "E1644", {"start": v(229, 109.74) * mm, "end": v(230.48, 108.12) * mm});
            skLineSegment(sketch, "E1645", {"start": v(230.48, 108.12) * mm, "end": v(231.73, 106.42) * mm});
            skLineSegment(sketch, "E1646", {"start": v(231.73, 106.42) * mm, "end": v(232.84, 104.65) * mm});
            skLineSegment(sketch, "E1647", {"start": v(232.84, 104.65) * mm, "end": v(233.72, 102.81) * mm});
            skLineSegment(sketch, "E1648", {"start": v(233.72, 102.81) * mm, "end": v(234.39, 100.82) * mm});
            skLineSegment(sketch, "E1649", {"start": v(234.39, 100.82) * mm, "end": v(234.9, 98.83) * mm});
            skLineSegment(sketch, "E1650", {"start": v(234.9, 98.83) * mm, "end": v(235.2, 96.7) * mm});
            skLineSegment(sketch, "E1651", {"start": v(235.2, 96.7) * mm, "end": v(235.35, 94.48) * mm});
            skLineSegment(sketch, "E1652", {"start": v(235.35, 94.48) * mm, "end": v(235.35, 74.43) * mm});
            skLineSegment(sketch, "E1653", {"start": v(235.35, 74.43) * mm, "end": v(235.27, 73.92) * mm});
            skLineSegment(sketch, "E1654", {"start": v(235.27, 73.92) * mm, "end": v(235.2, 73.33) * mm});
            skLineSegment(sketch, "E1655", {"start": v(235.2, 73.33) * mm, "end": v(235.05, 72.81) * mm});
            skLineSegment(sketch, "E1656", {"start": v(235.05, 72.81) * mm, "end": v(234.9, 72.3) * mm});
            skLineSegment(sketch, "E1657", {"start": v(234.9, 72.3) * mm, "end": v(234.68, 71.78) * mm});
            skLineSegment(sketch, "E1658", {"start": v(234.68, 71.78) * mm, "end": v(234.39, 71.26) * mm});
            skLineSegment(sketch, "E1659", {"start": v(234.39, 71.26) * mm, "end": v(234.02, 70.82) * mm});
            skLineSegment(sketch, "E1660", {"start": v(234.02, 70.82) * mm, "end": v(233.65, 70.38) * mm});
            skLineSegment(sketch, "E1661", {"start": v(233.65, 70.38) * mm, "end": v(233.2, 70) * mm});
            skLineSegment(sketch, "E1662", {"start": v(233.2, 70) * mm, "end": v(232.77, 69.64) * mm});
            skLineSegment(sketch, "E1663", {"start": v(232.77, 69.64) * mm, "end": v(232.25, 69.35) * mm});
            skLineSegment(sketch, "E1664", {"start": v(232.25, 69.35) * mm, "end": v(231.73, 69.13) * mm});
            skLineSegment(sketch, "E1665", {"start": v(231.73, 69.13) * mm, "end": v(231.22, 68.98) * mm});
            skLineSegment(sketch, "E1666", {"start": v(231.22, 68.98) * mm, "end": v(230.7, 68.83) * mm});
            skLineSegment(sketch, "E1667", {"start": v(230.7, 68.83) * mm, "end": v(230.11, 68.76) * mm});
            skLineSegment(sketch, "E1668", {"start": v(230.11, 68.76) * mm, "end": v(229.6, 68.68) * mm});
            skLineSegment(sketch, "E1669", {"start": v(229.6, 68.68) * mm, "end": v(229, 68.76) * mm});
            skLineSegment(sketch, "E1670", {"start": v(229, 68.76) * mm, "end": v(228.42, 68.83) * mm});
            skLineSegment(sketch, "E1671", {"start": v(228.42, 68.83) * mm, "end": v(227.9, 68.98) * mm});
            skLineSegment(sketch, "E1672", {"start": v(227.9, 68.98) * mm, "end": v(227.38, 69.13) * mm});
            skLineSegment(sketch, "E1673", {"start": v(227.38, 69.13) * mm, "end": v(226.87, 69.35) * mm});
            skLineSegment(sketch, "E1674", {"start": v(226.87, 69.35) * mm, "end": v(226.35, 69.64) * mm});
            skLineSegment(sketch, "E1675", {"start": v(226.35, 69.64) * mm, "end": v(225.91, 70) * mm});
            skLineSegment(sketch, "E1676", {"start": v(225.91, 70) * mm, "end": v(225.47, 70.38) * mm});
            skLineSegment(sketch, "E1677", {"start": v(225.47, 70.38) * mm, "end": v(225.1, 70.82) * mm});
            skLineSegment(sketch, "E1678", {"start": v(225.1, 70.82) * mm, "end": v(224.73, 71.26) * mm});
            skLineSegment(sketch, "E1679", {"start": v(224.73, 71.26) * mm, "end": v(224.44, 71.78) * mm});
            skLineSegment(sketch, "E1680", {"start": v(224.44, 71.78) * mm, "end": v(224.21, 72.3) * mm});
            skLineSegment(sketch, "E1681", {"start": v(224.21, 72.3) * mm, "end": v(224.07, 72.81) * mm});
            skLineSegment(sketch, "E1682", {"start": v(224.07, 72.81) * mm, "end": v(223.92, 73.33) * mm});
            skLineSegment(sketch, "E1683", {"start": v(223.92, 73.33) * mm, "end": v(223.85, 73.92) * mm});
            skLineSegment(sketch, "E1684", {"start": v(223.85, 73.92) * mm, "end": v(223.85, 74.43) * mm});
            skLineSegment(sketch, "E1685", {"start": v(223.85, 74.43) * mm, "end": v(223.85, 94.48) * mm});
            skLineSegment(sketch, "E1686", {"start": v(223.85, 94.48) * mm, "end": v(223.77, 95.51) * mm});
            skLineSegment(sketch, "E1687", {"start": v(223.77, 95.51) * mm, "end": v(223.63, 96.55) * mm});
            skLineSegment(sketch, "E1688", {"start": v(223.63, 96.55) * mm, "end": v(223.4, 97.5) * mm});
            skLineSegment(sketch, "E1689", {"start": v(223.4, 97.5) * mm, "end": v(223.1, 98.39) * mm});
            skLineSegment(sketch, "E1690", {"start": v(223.1, 98.39) * mm, "end": v(222.67, 99.27) * mm});
            skLineSegment(sketch, "E1691", {"start": v(222.67, 99.27) * mm, "end": v(222.15, 100.08) * mm});
            skLineSegment(sketch, "E1692", {"start": v(222.15, 100.08) * mm, "end": v(221.56, 100.9) * mm});
            skLineSegment(sketch, "E1693", {"start": v(221.56, 100.9) * mm, "end": v(220.9, 101.63) * mm});
            skLineSegment(sketch, "E1694", {"start": v(220.9, 101.63) * mm, "end": v(220.09, 102.3) * mm});
            skLineSegment(sketch, "E1695", {"start": v(220.09, 102.3) * mm, "end": v(219.28, 102.89) * mm});
            skLineSegment(sketch, "E1696", {"start": v(219.28, 102.89) * mm, "end": v(218.47, 103.4) * mm});
            skLineSegment(sketch, "E1697", {"start": v(218.47, 103.4) * mm, "end": v(217.58, 103.84) * mm});
            skLineSegment(sketch, "E1698", {"start": v(217.58, 103.84) * mm, "end": v(216.7, 104.14) * mm});
            skLineSegment(sketch, "E1699", {"start": v(216.7, 104.14) * mm, "end": v(215.74, 104.36) * mm});
            skLineSegment(sketch, "E1700", {"start": v(215.74, 104.36) * mm, "end": v(214.78, 104.5) * mm});
            skLineSegment(sketch, "E1701", {"start": v(214.78, 104.5) * mm, "end": v(213.75, 104.58) * mm});
            skLineSegment(sketch, "E1702", {"start": v(213.75, 104.58) * mm, "end": v(212.72, 104.5) * mm});
            skLineSegment(sketch, "E1703", {"start": v(212.72, 104.5) * mm, "end": v(211.76, 104.36) * mm});
            skLineSegment(sketch, "E1704", {"start": v(211.76, 104.36) * mm, "end": v(210.8, 104.14) * mm});
            skLineSegment(sketch, "E1705", {"start": v(210.8, 104.14) * mm, "end": v(209.91, 103.84) * mm});
            skLineSegment(sketch, "E1706", {"start": v(209.91, 103.84) * mm, "end": v(209.03, 103.4) * mm});
            skLineSegment(sketch, "E1707", {"start": v(209.03, 103.4) * mm, "end": v(208.22, 102.89) * mm});
            skLineSegment(sketch, "E1708", {"start": v(208.22, 102.89) * mm, "end": v(207.4, 102.3) * mm});
            skLineSegment(sketch, "E1709", {"start": v(207.4, 102.3) * mm, "end": v(206.6, 101.63) * mm});
            skLineSegment(sketch, "E1710", {"start": v(206.6, 101.63) * mm, "end": v(205.93, 100.9) * mm});
            skLineSegment(sketch, "E1711", {"start": v(205.93, 100.9) * mm, "end": v(205.34, 100.08) * mm});
            skLineSegment(sketch, "E1712", {"start": v(205.34, 100.08) * mm, "end": v(204.83, 99.27) * mm});
            skLineSegment(sketch, "E1713", {"start": v(204.83, 99.27) * mm, "end": v(204.39, 98.39) * mm});
            skLineSegment(sketch, "E1714", {"start": v(204.39, 98.39) * mm, "end": v(204.1, 97.5) * mm});
            skLineSegment(sketch, "E1715", {"start": v(204.1, 97.5) * mm, "end": v(203.87, 96.55) * mm});
            skLineSegment(sketch, "E1716", {"start": v(203.87, 96.55) * mm, "end": v(203.72, 95.51) * mm});
            skLineSegment(sketch, "E1717", {"start": v(203.72, 95.51) * mm, "end": v(203.65, 94.48) * mm});
            skLineSegment(sketch, "E1718", {"start": v(203.65, 94.48) * mm, "end": v(203.65, 74.43) * mm});
            skLineSegment(sketch, "E1719", {"start": v(203.65, 74.43) * mm, "end": v(203.65, 73.92) * mm});
            skLineSegment(sketch, "E1720", {"start": v(203.65, 73.92) * mm, "end": v(203.58, 73.33) * mm});
            skLineSegment(sketch, "E1721", {"start": v(203.58, 73.33) * mm, "end": v(203.43, 72.81) * mm});
            skLineSegment(sketch, "E1722", {"start": v(203.43, 72.81) * mm, "end": v(203.28, 72.3) * mm});
            skLineSegment(sketch, "E1723", {"start": v(203.28, 72.3) * mm, "end": v(203.06, 71.78) * mm});
            skLineSegment(sketch, "E1724", {"start": v(203.06, 71.78) * mm, "end": v(202.76, 71.26) * mm});
            skLineSegment(sketch, "E1725", {"start": v(202.76, 71.26) * mm, "end": v(202.4, 70.82) * mm});
            skLineSegment(sketch, "E1726", {"start": v(202.4, 70.82) * mm, "end": v(202.03, 70.38) * mm});
            skLineSegment(sketch, "E1727", {"start": v(202.03, 70.38) * mm, "end": v(201.59, 70) * mm});
            skLineSegment(sketch, "E1728", {"start": v(201.59, 70) * mm, "end": v(201.14, 69.64) * mm});
            skLineSegment(sketch, "E1729", {"start": v(201.14, 69.64) * mm, "end": v(200.63, 69.35) * mm});
            skLineSegment(sketch, "E1730", {"start": v(200.63, 69.35) * mm, "end": v(200.11, 69.13) * mm});
            skLineSegment(sketch, "E1731", {"start": v(200.11, 69.13) * mm, "end": v(199.6, 68.98) * mm});
            skLineSegment(sketch, "E1732", {"start": v(199.6, 68.98) * mm, "end": v(199.08, 68.83) * mm});
            skLineSegment(sketch, "E1733", {"start": v(199.08, 68.83) * mm, "end": v(198.49, 68.76) * mm});
            skLineSegment(sketch, "E1734", {"start": v(198.49, 68.76) * mm, "end": v(197.9, 68.68) * mm});
            skLineSegment(sketch, "E1735", {"start": v(197.9, 68.68) * mm, "end": v(197.38, 68.76) * mm});
            skLineSegment(sketch, "E1736", {"start": v(197.38, 68.76) * mm, "end": v(196.8, 68.83) * mm});
            skLineSegment(sketch, "E1737", {"start": v(196.8, 68.83) * mm, "end": v(196.28, 68.98) * mm});
            skLineSegment(sketch, "E1738", {"start": v(196.28, 68.98) * mm, "end": v(195.76, 69.13) * mm});
            skLineSegment(sketch, "E1739", {"start": v(195.76, 69.13) * mm, "end": v(195.25, 69.35) * mm});
            skLineSegment(sketch, "E1740", {"start": v(195.25, 69.35) * mm, "end": v(194.73, 69.64) * mm});
            skLineSegment(sketch, "E1741", {"start": v(194.73, 69.64) * mm, "end": v(194.29, 70) * mm});
            skLineSegment(sketch, "E1742", {"start": v(194.29, 70) * mm, "end": v(193.85, 70.38) * mm});
            skLineSegment(sketch, "E1743", {"start": v(193.85, 70.38) * mm, "end": v(193.48, 70.82) * mm});
            skLineSegment(sketch, "E1744", {"start": v(193.48, 70.82) * mm, "end": v(193.1, 71.26) * mm});
            skLineSegment(sketch, "E1745", {"start": v(193.1, 71.26) * mm, "end": v(192.81, 71.78) * mm});
            skLineSegment(sketch, "E1746", {"start": v(192.81, 71.78) * mm, "end": v(192.6, 72.3) * mm});
            skLineSegment(sketch, "E1747", {"start": v(192.6, 72.3) * mm, "end": v(192.44, 72.81) * mm});
            skLineSegment(sketch, "E1748", {"start": v(192.44, 72.81) * mm, "end": v(192.3, 73.33) * mm});
            skLineSegment(sketch, "E1749", {"start": v(192.3, 73.33) * mm, "end": v(192.22, 73.92) * mm});
            skLineSegment(sketch, "E1750", {"start": v(192.22, 73.92) * mm, "end": v(192.15, 74.43) * mm});
            skLineSegment(sketch, "E1751", {"start": v(192.15, 74.43) * mm, "end": v(192.15, 94.48) * mm});
            skLineSegment(sketch, "E1752", {"start": v(192.15, 94.48) * mm, "end": v(192.3, 96.7) * mm});
            skLineSegment(sketch, "E1753", {"start": v(246.92, 47.23) * mm, "end": v(246.84, 47.82) * mm});
            skLineSegment(sketch, "E1754", {"start": v(246.84, 47.82) * mm, "end": v(246.84, 48.41) * mm});
            skLineSegment(sketch, "E1755", {"start": v(246.84, 48.41) * mm, "end": v(246.84, 48.63) * mm});
            skLineSegment(sketch, "E1756", {"start": v(246.84, 48.63) * mm, "end": v(246.84, 48.85) * mm});
            skLineSegment(sketch, "E1757", {"start": v(246.84, 48.85) * mm, "end": v(246.84, 49.08) * mm});
            skLineSegment(sketch, "E1758", {"start": v(246.84, 49.08) * mm, "end": v(246.84, 49.3) * mm});
            skLineSegment(sketch, "E1759", {"start": v(246.84, 49.3) * mm, "end": v(246.92, 49.52) * mm});
            skLineSegment(sketch, "E1760", {"start": v(246.92, 49.52) * mm, "end": v(247, 49.67) * mm});
            skLineSegment(sketch, "E1761", {"start": v(247, 49.67) * mm, "end": v(247, 49.89) * mm});
            skLineSegment(sketch, "E1762", {"start": v(247, 49.89) * mm, "end": v(247.07, 50.03) * mm});
            skLineSegment(sketch, "E1763", {"start": v(247.07, 50.03) * mm, "end": v(258.34, 108.86) * mm});
            skLineSegment(sketch, "E1764", {"start": v(258.34, 108.86) * mm, "end": v(258.42, 109.45) * mm});
            skLineSegment(sketch, "E1765", {"start": v(258.42, 109.45) * mm, "end": v(258.56, 110.04) * mm});
            skLineSegment(sketch, "E1766", {"start": v(258.56, 110.04) * mm, "end": v(258.71, 110.55) * mm});
            skLineSegment(sketch, "E1767", {"start": v(258.71, 110.55) * mm, "end": v(258.93, 111.07) * mm});
            skLineSegment(sketch, "E1768", {"start": v(258.93, 111.07) * mm, "end": v(259.15, 111.58) * mm});
            skLineSegment(sketch, "E1769", {"start": v(259.15, 111.58) * mm, "end": v(259.45, 112.03) * mm});
            skLineSegment(sketch, "E1770", {"start": v(259.45, 112.03) * mm, "end": v(259.74, 112.47) * mm});
            skLineSegment(sketch, "E1771", {"start": v(259.74, 112.47) * mm, "end": v(260.11, 112.91) * mm});
            skLineSegment(sketch, "E1772", {"start": v(260.11, 112.91) * mm, "end": v(260.56, 113.28) * mm});
            skLineSegment(sketch, "E1773", {"start": v(260.56, 113.28) * mm, "end": v(261, 113.65) * mm});
            skLineSegment(sketch, "E1774", {"start": v(261, 113.65) * mm, "end": v(261.44, 113.94) * mm});
            skLineSegment(sketch, "E1775", {"start": v(261.44, 113.94) * mm, "end": v(261.88, 114.16) * mm});
            skLineSegment(sketch, "E1776", {"start": v(261.88, 114.16) * mm, "end": v(262.4, 114.31) * mm});
            skLineSegment(sketch, "E1777", {"start": v(262.4, 114.31) * mm, "end": v(262.91, 114.46) * mm});
            skLineSegment(sketch, "E1778", {"start": v(262.91, 114.46) * mm, "end": v(263.5, 114.53) * mm});
            skLineSegment(sketch, "E1779", {"start": v(263.5, 114.53) * mm, "end": v(264.1, 114.53) * mm});
            skLineSegment(sketch, "E1780", {"start": v(264.1, 114.53) * mm, "end": v(264.6, 114.53) * mm});
            skLineSegment(sketch, "E1781", {"start": v(264.6, 114.53) * mm, "end": v(265.2, 114.46) * mm});
            skLineSegment(sketch, "E1782", {"start": v(265.2, 114.46) * mm, "end": v(265.71, 114.31) * mm});
            skLineSegment(sketch, "E1783", {"start": v(265.71, 114.31) * mm, "end": v(266.23, 114.16) * mm});
            skLineSegment(sketch, "E1784", {"start": v(266.23, 114.16) * mm, "end": v(266.75, 113.94) * mm});
            skLineSegment(sketch, "E1785", {"start": v(266.75, 113.94) * mm, "end": v(267.26, 113.65) * mm});
            skLineSegment(sketch, "E1786", {"start": v(267.26, 113.65) * mm, "end": v(267.7, 113.28) * mm});
            skLineSegment(sketch, "E1787", {"start": v(267.7, 113.28) * mm, "end": v(268.15, 112.91) * mm});
            skLineSegment(sketch, "E1788", {"start": v(268.15, 112.91) * mm, "end": v(268.52, 112.47) * mm});
            skLineSegment(sketch, "E1789", {"start": v(268.52, 112.47) * mm, "end": v(268.88, 112.03) * mm});
            skLineSegment(sketch, "E1790", {"start": v(268.88, 112.03) * mm, "end": v(269.18, 111.5) * mm});
            skLineSegment(sketch, "E1791", {"start": v(269.18, 111.5) * mm, "end": v(269.4, 111) * mm});
            skLineSegment(sketch, "E1792", {"start": v(269.4, 111) * mm, "end": v(269.55, 110.48) * mm});
            skLineSegment(sketch, "E1793", {"start": v(269.55, 110.48) * mm, "end": v(269.7, 109.96) * mm});
            skLineSegment(sketch, "E1794", {"start": v(269.7, 109.96) * mm, "end": v(269.77, 109.37) * mm});
            skLineSegment(sketch, "E1795", {"start": v(269.77, 109.37) * mm, "end": v(269.84, 108.78) * mm});
            skLineSegment(sketch, "E1796", {"start": v(269.84, 108.78) * mm, "end": v(269.77, 108.63) * mm});
            skLineSegment(sketch, "E1797", {"start": v(269.77, 108.63) * mm, "end": v(269.77, 108.41) * mm});
            skLineSegment(sketch, "E1798", {"start": v(269.77, 108.41) * mm, "end": v(269.77, 108.2) * mm});
            skLineSegment(sketch, "E1799", {"start": v(269.77, 108.2) * mm, "end": v(269.77, 107.97) * mm});
            skLineSegment(sketch, "E1800", {"start": v(269.77, 107.97) * mm, "end": v(269.77, 107.75) * mm});
            skLineSegment(sketch, "E1801", {"start": v(269.77, 107.75) * mm, "end": v(269.7, 107.53) * mm});
            skLineSegment(sketch, "E1802", {"start": v(269.7, 107.53) * mm, "end": v(269.7, 107.38) * mm});
            skLineSegment(sketch, "E1803", {"start": v(269.7, 107.38) * mm, "end": v(269.7, 107.16) * mm});
            skLineSegment(sketch, "E1804", {"start": v(269.7, 107.16) * mm, "end": v(259.52, 54.16) * mm});
            skLineSegment(sketch, "E1805", {"start": v(259.52, 54.16) * mm, "end": v(279.87, 54.16) * mm});
            skLineSegment(sketch, "E1806", {"start": v(279.87, 54.16) * mm, "end": v(279.87, 91.53) * mm});
            skLineSegment(sketch, "E1807", {"start": v(279.87, 91.53) * mm, "end": v(279.87, 92.05) * mm});
            skLineSegment(sketch, "E1808", {"start": v(279.87, 92.05) * mm, "end": v(279.94, 92.64) * mm});
            skLineSegment(sketch, "E1809", {"start": v(279.94, 92.64) * mm, "end": v(280.09, 93.16) * mm});
            skLineSegment(sketch, "E1810", {"start": v(280.09, 93.16) * mm, "end": v(280.3, 93.67) * mm});
            skLineSegment(sketch, "E1811", {"start": v(280.3, 93.67) * mm, "end": v(280.53, 94.19) * mm});
            skLineSegment(sketch, "E1812", {"start": v(280.53, 94.19) * mm, "end": v(280.83, 94.7) * mm});
            skLineSegment(sketch, "E1813", {"start": v(280.83, 94.7) * mm, "end": v(281.2, 95.15) * mm});
            skLineSegment(sketch, "E1814", {"start": v(281.2, 95.15) * mm, "end": v(281.56, 95.59) * mm});
            skLineSegment(sketch, "E1815", {"start": v(281.56, 95.59) * mm, "end": v(282, 95.96) * mm});
            skLineSegment(sketch, "E1816", {"start": v(282, 95.96) * mm, "end": v(282.45, 96.32) * mm});
            skLineSegment(sketch, "E1817", {"start": v(282.45, 96.32) * mm, "end": v(282.89, 96.62) * mm});
            skLineSegment(sketch, "E1818", {"start": v(282.89, 96.62) * mm, "end": v(283.4, 96.84) * mm});
            skLineSegment(sketch, "E1819", {"start": v(283.4, 96.84) * mm, "end": v(283.92, 96.99) * mm});
            skLineSegment(sketch, "E1820", {"start": v(283.92, 96.99) * mm, "end": v(284.44, 97.14) * mm});
            skLineSegment(sketch, "E1821", {"start": v(284.44, 97.14) * mm, "end": v(285.03, 97.2) * mm});
            skLineSegment(sketch, "E1822", {"start": v(285.03, 97.2) * mm, "end": v(285.62, 97.28) * mm});
            skLineSegment(sketch, "E1823", {"start": v(285.62, 97.28) * mm, "end": v(286.2, 97.2) * mm});
            skLineSegment(sketch, "E1824", {"start": v(286.2, 97.2) * mm, "end": v(286.8, 97.14) * mm});
            skLineSegment(sketch, "E1825", {"start": v(286.8, 97.14) * mm, "end": v(287.31, 96.99) * mm});
            skLineSegment(sketch, "E1826", {"start": v(287.31, 96.99) * mm, "end": v(287.83, 96.84) * mm});
            skLineSegment(sketch, "E1827", {"start": v(287.83, 96.84) * mm, "end": v(288.34, 96.62) * mm});
            skLineSegment(sketch, "E1828", {"start": v(288.34, 96.62) * mm, "end": v(288.79, 96.32) * mm});
            skLineSegment(sketch, "E1829", {"start": v(288.79, 96.32) * mm, "end": v(289.23, 95.96) * mm});
            skLineSegment(sketch, "E1830", {"start": v(289.23, 95.96) * mm, "end": v(289.67, 95.59) * mm});
            skLineSegment(sketch, "E1831", {"start": v(289.67, 95.59) * mm, "end": v(290.04, 95.15) * mm});
            skLineSegment(sketch, "E1832", {"start": v(290.04, 95.15) * mm, "end": v(290.4, 94.7) * mm});
            skLineSegment(sketch, "E1833", {"start": v(290.4, 94.7) * mm, "end": v(290.7, 94.19) * mm});
            skLineSegment(sketch, "E1834", {"start": v(290.7, 94.19) * mm, "end": v(290.92, 93.67) * mm});
            skLineSegment(sketch, "E1835", {"start": v(290.92, 93.67) * mm, "end": v(291.15, 93.16) * mm});
            skLineSegment(sketch, "E1836", {"start": v(291.15, 93.16) * mm, "end": v(291.3, 92.64) * mm});
            skLineSegment(sketch, "E1837", {"start": v(291.3, 92.64) * mm, "end": v(291.37, 92.05) * mm});
            skLineSegment(sketch, "E1838", {"start": v(291.37, 92.05) * mm, "end": v(291.37, 91.53) * mm});
            skLineSegment(sketch, "E1839", {"start": v(291.37, 91.53) * mm, "end": v(291.37, 22.54) * mm});
            skLineSegment(sketch, "E1840", {"start": v(291.37, 22.54) * mm, "end": v(291.37, 21.95) * mm});
            skLineSegment(sketch, "E1841", {"start": v(291.37, 21.95) * mm, "end": v(291.3, 21.36) * mm});
            skLineSegment(sketch, "E1842", {"start": v(291.3, 21.36) * mm, "end": v(291.15, 20.84) * mm});
            skLineSegment(sketch, "E1843", {"start": v(291.15, 20.84) * mm, "end": v(290.92, 20.33) * mm});
            skLineSegment(sketch, "E1844", {"start": v(290.92, 20.33) * mm, "end": v(290.7, 19.81) * mm});
            skLineSegment(sketch, "E1845", {"start": v(290.7, 19.81) * mm, "end": v(290.4, 19.3) * mm});
            skLineSegment(sketch, "E1846", {"start": v(290.4, 19.3) * mm, "end": v(290.04, 18.85) * mm});
            skLineSegment(sketch, "E1847", {"start": v(290.04, 18.85) * mm, "end": v(289.67, 18.41) * mm});
            skLineSegment(sketch, "E1848", {"start": v(289.67, 18.41) * mm, "end": v(289.23, 18.04) * mm});
            skLineSegment(sketch, "E1849", {"start": v(289.23, 18.04) * mm, "end": v(288.79, 17.67) * mm});
            skLineSegment(sketch, "E1850", {"start": v(288.79, 17.67) * mm, "end": v(288.34, 17.38) * mm});
            skLineSegment(sketch, "E1851", {"start": v(288.34, 17.38) * mm, "end": v(287.83, 17.16) * mm});
            skLineSegment(sketch, "E1852", {"start": v(287.83, 17.16) * mm, "end": v(287.31, 17.01) * mm});
            skLineSegment(sketch, "E1853", {"start": v(287.31, 17.01) * mm, "end": v(286.8, 16.86) * mm});
            skLineSegment(sketch, "E1854", {"start": v(286.8, 16.86) * mm, "end": v(286.2, 16.79) * mm});
            skLineSegment(sketch, "E1855", {"start": v(286.2, 16.79) * mm, "end": v(285.62, 16.79) * mm});
            skLineSegment(sketch, "E1856", {"start": v(285.62, 16.79) * mm, "end": v(285.03, 16.79) * mm});
            skLineSegment(sketch, "E1857", {"start": v(285.03, 16.79) * mm, "end": v(284.44, 16.86) * mm});
            skLineSegment(sketch, "E1858", {"start": v(284.44, 16.86) * mm, "end": v(283.92, 17.01) * mm});
            skLineSegment(sketch, "E1859", {"start": v(283.92, 17.01) * mm, "end": v(283.4, 17.16) * mm});
            skLineSegment(sketch, "E1860", {"start": v(283.4, 17.16) * mm, "end": v(282.89, 17.38) * mm});
            skLineSegment(sketch, "E1861", {"start": v(282.89, 17.38) * mm, "end": v(282.45, 17.67) * mm});
            skLineSegment(sketch, "E1862", {"start": v(282.45, 17.67) * mm, "end": v(282, 18.04) * mm});
            skLineSegment(sketch, "E1863", {"start": v(282, 18.04) * mm, "end": v(281.56, 18.41) * mm});
            skLineSegment(sketch, "E1864", {"start": v(281.56, 18.41) * mm, "end": v(281.2, 18.85) * mm});
            skLineSegment(sketch, "E1865", {"start": v(281.2, 18.85) * mm, "end": v(280.83, 19.3) * mm});
            skLineSegment(sketch, "E1866", {"start": v(280.83, 19.3) * mm, "end": v(280.53, 19.81) * mm});
            skLineSegment(sketch, "E1867", {"start": v(280.53, 19.81) * mm, "end": v(280.3, 20.33) * mm});
            skLineSegment(sketch, "E1868", {"start": v(280.3, 20.33) * mm, "end": v(280.09, 20.84) * mm});
            skLineSegment(sketch, "E1869", {"start": v(280.09, 20.84) * mm, "end": v(279.94, 21.36) * mm});
            skLineSegment(sketch, "E1870", {"start": v(279.94, 21.36) * mm, "end": v(279.87, 21.95) * mm});
            skLineSegment(sketch, "E1871", {"start": v(279.87, 21.95) * mm, "end": v(279.87, 22.54) * mm});
            skLineSegment(sketch, "E1872", {"start": v(279.87, 22.54) * mm, "end": v(279.87, 42.66) * mm});
            skLineSegment(sketch, "E1873", {"start": v(279.87, 42.66) * mm, "end": v(252.6, 42.66) * mm});
            skLineSegment(sketch, "E1874", {"start": v(252.6, 42.66) * mm, "end": v(252, 42.66) * mm});
            skLineSegment(sketch, "E1875", {"start": v(252, 42.66) * mm, "end": v(251.41, 42.74) * mm});
            skLineSegment(sketch, "E1876", {"start": v(251.41, 42.74) * mm, "end": v(250.9, 42.88) * mm});
            skLineSegment(sketch, "E1877", {"start": v(250.9, 42.88) * mm, "end": v(250.38, 43.03) * mm});
            skLineSegment(sketch, "E1878", {"start": v(250.38, 43.03) * mm, "end": v(249.87, 43.33) * mm});
            skLineSegment(sketch, "E1879", {"start": v(249.87, 43.33) * mm, "end": v(249.35, 43.62) * mm});
            skLineSegment(sketch, "E1880", {"start": v(249.35, 43.62) * mm, "end": v(248.9, 43.92) * mm});
            skLineSegment(sketch, "E1881", {"start": v(248.9, 43.92) * mm, "end": v(248.47, 44.36) * mm});
            skLineSegment(sketch, "E1882", {"start": v(248.47, 44.36) * mm, "end": v(248.1, 44.8) * mm});
            skLineSegment(sketch, "E1883", {"start": v(248.1, 44.8) * mm, "end": v(247.73, 45.24) * mm});
            skLineSegment(sketch, "E1884", {"start": v(247.73, 45.24) * mm, "end": v(247.43, 45.76) * mm});
            skLineSegment(sketch, "E1885", {"start": v(247.43, 45.76) * mm, "end": v(247.21, 46.2) * mm});
            skLineSegment(sketch, "E1886", {"start": v(247.21, 46.2) * mm, "end": v(247.07, 46.72) * mm});
            skLineSegment(sketch, "E1887", {"start": v(247.07, 46.72) * mm, "end": v(246.92, 47.23) * mm});
            skCircle(sketch, "E1888", {"center": v(170.33, 123.42) * mm, "radius": 1.59 * mm});
            skCircle(sketch, "E1889.MirrorC", {"center": v(170.33, -1.43) * mm, "radius": 1.59 * mm});
            skLineSegment(sketch, "E1890", {"start": v(147.11, 101.04) * mm, "end": v(147.55, 101.41) * mm});
            skSolve(sketch);
        }
        {
            var Q0;
            Q0=makeQuery(id+"F0.imprint","IMPRINT",FACE,{"disambiguationData":[TD([[makeQuery(id+"F0.imprint","IMPRINT",EDGE,{"derivedFrom":sQuery(id+"F0.wireOp",EDGE,"E0.bottom")}),-1.0]])]});
            extrude(context, id + "F1", {"entities" : qUnion([Q0]), "depth" : 1.27 * mm, "offsetDistance" : 25.4 * mm});
        }
    });
